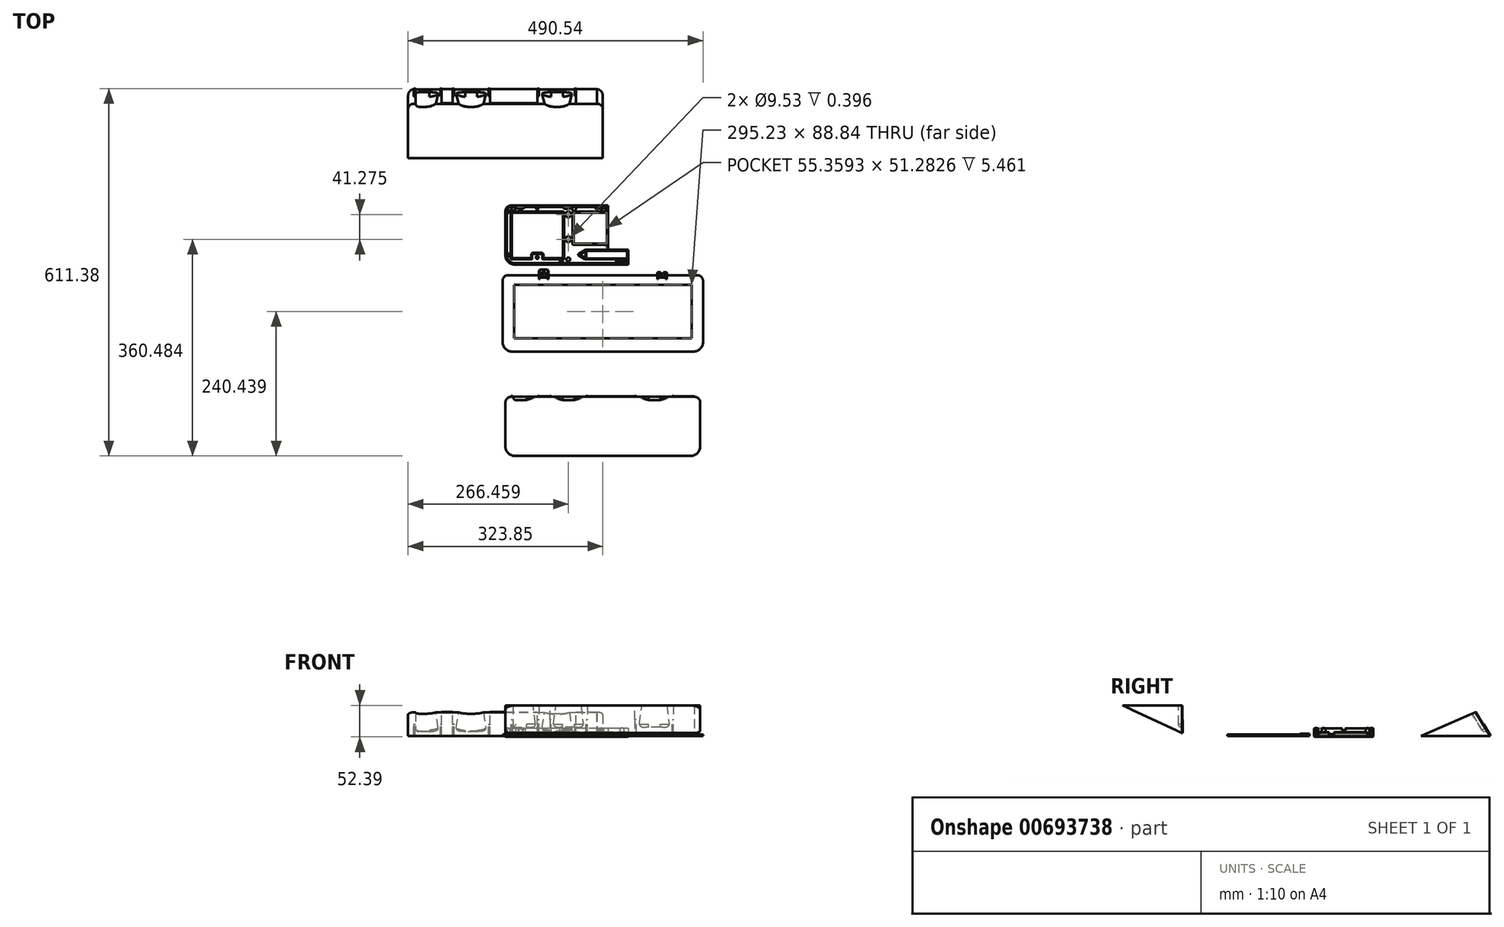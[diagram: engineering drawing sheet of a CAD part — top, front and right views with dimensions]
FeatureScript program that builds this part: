
annotation { "Feature Type Name" : "Feature", "Feature Type Description" : "" }
export const myFeature = defineFeature(function(context is Context, id is Id, definition is map)
    precondition{}
    {
        {
            var Q0;
            Q0=qCreatedBy(makeId("Top.planeOp"),FACE);
            var sketch = newSketch(context, id + "F0", { "sketchPlane" : qUnion([Q0])});
            skLineSegment(sketch, "E0.bottom", {"start": v(161.93, -49.21) * mm, "end": v(-161.93, -49.21) * mm});
            skLineSegment(sketch, "E0.top", {"start": v(161.93, 49.21) * mm, "end": v(-161.93, 49.21) * mm});
            skLineSegment(sketch, "E0.left", {"start": v(161.93, -49.21) * mm, "end": v(161.93, 49.21) * mm});
            skLineSegment(sketch, "E0.right", {"start": v(-161.93, -49.21) * mm, "end": v(-161.93, 49.21) * mm});
            skPoint(sketch, "E0.middle", {"position": v(0, 0) * mm});
            skSolve(sketch);
        }
        {
            var Q0;
            Q0=makeQuery(id+"F0.imprint","IMPRINT",FACE,{"disambiguationData":[TD([[makeQuery(id+"F0.imprint","IMPRINT",EDGE,{"derivedFrom":sQuery(id+"F0.wireOp",EDGE,"E0.bottom")}),-1.0]])]});
            extrude(context, id + "F1", {"entities" : qUnion([Q0]), "depth" : 3.17 * mm, "offsetDistance" : 25.4 * mm});
        }
        {
            var Q0;
            Q0=makeQuery(id+"F1.opExtrude","SWEPT_EDGE",EDGE,{"disambiguationData":[OSD([sQuery(id+"F0.wireOp",EDGE,"E0.bottom"),sQuery(id+"F0.wireOp",EDGE,"E0.right")])]});
            var Q1;
            Q1=makeQuery(id+"F1.opExtrude","SWEPT_EDGE",EDGE,{"disambiguationData":[OSD([sQuery(id+"F0.wireOp",EDGE,"E0.bottom"),sQuery(id+"F0.wireOp",EDGE,"E0.left")])]});
            fillet(context, id + "F2", {"entities" : qUnion([Q0, Q1]), "radius" : 15.88 * mm, "tangentPropagation" : true, "allowEdgeOverflow" : false});
        }
        {
            var Q0;
            Q0=makeQuery(id+"F1.opExtrude","SWEPT_EDGE",EDGE,{"disambiguationData":[OSD([sQuery(id+"F0.wireOp",EDGE,"E0.top"),sQuery(id+"F0.wireOp",EDGE,"E0.right")])]});
            var Q1;
            Q1=makeQuery(id+"F1.opExtrude","SWEPT_EDGE",EDGE,{"disambiguationData":[OSD([sQuery(id+"F0.wireOp",EDGE,"E0.top"),sQuery(id+"F0.wireOp",EDGE,"E0.left")])]});
            fillet(context, id + "F3", {"entities" : qUnion([Q0, Q1]), "radius" : 9.52 * mm, "tangentPropagation" : true, "allowEdgeOverflow" : false});
        }
        {
            var Q0;
            Q0=makeQuery(id+"F1.opExtrude","CAP_FACE",FACE,{"disambiguationData":[OSD([sQuery(id+"F0.wireOp",EDGE,"E0.bottom"),sQuery(id+"F0.wireOp",EDGE,"E0.top"),sQuery(id+"F0.wireOp",EDGE,"E0.left"),sQuery(id+"F0.wireOp",EDGE,"E0.right")])],"isStart":false});
            var sketch = newSketch(context, id + "F4", { "sketchPlane" : qUnion([Q0])});
            skArc(sketch, "E1.0", {"start": v(-152.4, 46.93) * mm, "mid": v(-157.52, 44.8) * mm, "end": v(-159.64, 39.69) * mm});
            skArc(sketch, "E2.0", {"start": v(-159.64, -33.34) * mm, "mid": v(-155.66, -42.95) * mm, "end": v(-146.05, -46.93) * mm});
            skLineSegment(sketch, "E3.0", {"start": v(-159.64, -33.34) * mm, "end": v(-159.64, 39.69) * mm});
            skArc(sketch, "E4.0", {"start": v(146.05, -46.93) * mm, "mid": v(155.66, -42.95) * mm, "end": v(159.64, -33.34) * mm});
            skArc(sketch, "E5.0", {"start": v(159.64, 39.69) * mm, "mid": v(157.52, 44.8) * mm, "end": v(152.4, 46.93) * mm});
            skLineSegment(sketch, "E6.0", {"start": v(159.64, -33.34) * mm, "end": v(159.64, 39.69) * mm});
            skLineSegment(sketch, "E7.0", {"start": v(152.4, 46.93) * mm, "end": v(-152.4, 46.93) * mm});
            skLineSegment(sketch, "E8.0", {"start": v(146.05, -46.93) * mm, "end": v(-146.05, -46.93) * mm});
            skSolve(sketch);
        }
        {
            var Q0;
            Q0=makeQuery(id+"F4.imprint","IMPRINT",FACE,{"disambiguationData":[TD([[makeQuery(id+"F4.imprint","IMPRINT",EDGE,{"derivedFrom":sQuery(id+"F4.wireOp",EDGE,"E1.0")}),-1.0]])]});
            extrude(context, id + "F5", {"entities" : qUnion([Q0]), "operationType" : NewBodyOperationType.ADD, "depth" : 9.52 * mm, "offsetDistance" : 25.4 * mm});
        }
        {
            var Q0;
            Q0=makeQuery(id+"F1.opExtrude","CAP_FACE",FACE,{"disambiguationData":[OSD([sQuery(id+"F0.wireOp",EDGE,"E0.bottom"),sQuery(id+"F0.wireOp",EDGE,"E0.top"),sQuery(id+"F0.wireOp",EDGE,"E0.left"),sQuery(id+"F0.wireOp",EDGE,"E0.right")])],"isStart":false});
            var sketch = newSketch(context, id + "F6", { "sketchPlane" : qUnion([Q0])});
            skCircle(sketch, "E9", {"center": v(-158.52, -33.34) * mm, "radius": 3.18 * mm});
            skLineSegment(sketch, "E10", {"start": v(-158.52, -33.34) * mm, "end": v(-158.52, 39.69) * mm, "construction": true});
            skCircle(sketch, "E11", {"center": v(-158.52, 39.69) * mm, "radius": 3.18 * mm});
            skCircle(sketch, "E12", {"center": v(158.23, 39.4) * mm, "radius": 3.18 * mm});
            skCircle(sketch, "E13", {"center": v(157.67, -33.34) * mm, "radius": 3.18 * mm});
            skCircle(sketch, "E14", {"center": v(70.74, 45.8) * mm, "radius": 3.18 * mm});
            skCircle(sketch, "E15", {"center": v(-2.29, 45.8) * mm, "radius": 3.29 * mm});
            skCircle(sketch, "E16", {"center": v(31.57, -45.8) * mm, "radius": 3.18 * mm});
            skCircle(sketch, "E17", {"center": v(-68.96, -45.8) * mm, "radius": 3.18 * mm});
            skSolve(sketch);
        }
        {
            var Q0;
            {var subQ0=sQuery(id+"F6.wireOp",EDGE,"E9");var subQ1=makeQuery(id+"F5.opExtrude","CAP_EDGE",EDGE,{"disambiguationData":[OSD([sQuery(id+"F4.wireOp",EDGE,"E2.0")])],"isStart":true});var subQ2=makeQuery(id+"F6.imprint","INTERSECT",VERTEX,{"derivedFrom":[subQ1,subQ0]});Q0=makeQuery(id+"F6.imprint","IMPRINT",FACE,{"disambiguationData":[TD([[makeQuery(id+"F6.imprint","IMPRINT",EDGE,{"disambiguationData":[TD([[subQ2,-1.0]])],"derivedFrom":subQ0}),1.0]])]});}
            var Q1;
            {var subQ0=sQuery(id+"F6.wireOp",EDGE,"E11");var subQ1=makeQuery(id+"F5.opExtrude","CAP_EDGE",EDGE,{"disambiguationData":[OSD([sQuery(id+"F4.wireOp",EDGE,"E1.0")])],"isStart":true});var subQ2=makeQuery(id+"F6.imprint","INTERSECT",VERTEX,{"derivedFrom":[subQ1,subQ0]});Q1=makeQuery(id+"F6.imprint","IMPRINT",FACE,{"disambiguationData":[TD([[makeQuery(id+"F6.imprint","IMPRINT",EDGE,{"disambiguationData":[TD([[subQ2,1.0]])],"derivedFrom":subQ0}),1.0]])]});}
            var Q2;
            {var subQ0=sQuery(id+"F6.wireOp",EDGE,"E15");var subQ1=makeQuery(id+"F5.opExtrude","CAP_EDGE",EDGE,{"disambiguationData":[OSD([sQuery(id+"F4.wireOp",EDGE,"E7.0")])],"isStart":true});var subQ2=makeQuery(id+"F6.imprint","INTERSECT",VERTEX,{"disambiguationData":[OD(0.0)],"derivedFrom":[subQ1,subQ0]});Q2=makeQuery(id+"F6.imprint","IMPRINT",FACE,{"disambiguationData":[TD([[makeQuery(id+"F6.imprint","IMPRINT",EDGE,{"disambiguationData":[TD([[subQ2,-1.0]])],"derivedFrom":subQ0}),1.0]])]});}
            var Q3;
            {var subQ0=sQuery(id+"F6.wireOp",EDGE,"E14");var subQ1=makeQuery(id+"F5.opExtrude","CAP_EDGE",EDGE,{"disambiguationData":[OSD([sQuery(id+"F4.wireOp",EDGE,"E7.0")])],"isStart":true});var subQ2=makeQuery(id+"F6.imprint","INTERSECT",VERTEX,{"disambiguationData":[OD(0.0)],"derivedFrom":[subQ1,subQ0]});Q3=makeQuery(id+"F6.imprint","IMPRINT",FACE,{"disambiguationData":[TD([[makeQuery(id+"F6.imprint","IMPRINT",EDGE,{"disambiguationData":[TD([[subQ2,1.0]])],"derivedFrom":subQ0}),1.0]])]});}
            var Q4;
            {var subQ0=sQuery(id+"F6.wireOp",EDGE,"E17");var subQ1=makeQuery(id+"F5.opExtrude","CAP_EDGE",EDGE,{"disambiguationData":[OSD([sQuery(id+"F4.wireOp",EDGE,"E8.0")])],"isStart":true});var subQ2=makeQuery(id+"F6.imprint","INTERSECT",VERTEX,{"disambiguationData":[OD(0.0)],"derivedFrom":[subQ1,subQ0]});Q4=makeQuery(id+"F6.imprint","IMPRINT",FACE,{"disambiguationData":[TD([[makeQuery(id+"F6.imprint","IMPRINT",EDGE,{"disambiguationData":[TD([[subQ2,1.0]])],"derivedFrom":subQ0}),1.0]])]});}
            var Q5;
            {var subQ0=sQuery(id+"F6.wireOp",EDGE,"E16");var subQ1=makeQuery(id+"F5.opExtrude","CAP_EDGE",EDGE,{"disambiguationData":[OSD([sQuery(id+"F4.wireOp",EDGE,"E8.0")])],"isStart":true});var subQ2=makeQuery(id+"F6.imprint","INTERSECT",VERTEX,{"disambiguationData":[OD(0.0)],"derivedFrom":[subQ1,subQ0]});Q5=makeQuery(id+"F6.imprint","IMPRINT",FACE,{"disambiguationData":[TD([[makeQuery(id+"F6.imprint","IMPRINT",EDGE,{"disambiguationData":[TD([[subQ2,-1.0]])],"derivedFrom":subQ0}),1.0]])]});}
            var Q6;
            {var subQ0=sQuery(id+"F6.wireOp",EDGE,"E13");var subQ1=makeQuery(id+"F5.opExtrude","CAP_EDGE",EDGE,{"disambiguationData":[OSD([sQuery(id+"F4.wireOp",EDGE,"E4.0")])],"isStart":true});var subQ2=makeQuery(id+"F6.imprint","INTERSECT",VERTEX,{"derivedFrom":[subQ1,subQ0]});Q6=makeQuery(id+"F6.imprint","IMPRINT",FACE,{"disambiguationData":[TD([[makeQuery(id+"F6.imprint","IMPRINT",EDGE,{"disambiguationData":[TD([[subQ2,1.0]])],"derivedFrom":subQ0}),1.0]])]});}
            var Q7;
            {var subQ0=sQuery(id+"F6.wireOp",EDGE,"E12");var subQ1=makeQuery(id+"F5.opExtrude","CAP_EDGE",EDGE,{"disambiguationData":[OSD([sQuery(id+"F4.wireOp",EDGE,"E5.0")])],"isStart":true});var subQ2=makeQuery(id+"F6.imprint","INTERSECT",VERTEX,{"derivedFrom":[subQ1,subQ0]});Q7=makeQuery(id+"F6.imprint","IMPRINT",FACE,{"disambiguationData":[TD([[makeQuery(id+"F6.imprint","IMPRINT",EDGE,{"disambiguationData":[TD([[subQ2,-1.0]])],"derivedFrom":subQ0}),1.0]])]});}
            extrude(context, id + "F7", {"entities" : qUnion([Q0, Q1, Q2, Q3, Q4, Q5, Q6, Q7]), "operationType" : NewBodyOperationType.ADD, "depth" : 9.52 * mm, "offsetDistance" : 25.4 * mm});
        }
        {
            var Q0;
            {var subQ0=sQuery(id+"F4.wireOp",EDGE,"E8.0");var subQ1=sQuery(id+"F4.wireOp",EDGE,"E7.0");var subQ2=sQuery(id+"F4.wireOp",EDGE,"E6.0");var subQ3=sQuery(id+"F4.wireOp",EDGE,"E4.0");var subQ4=sQuery(id+"F4.wireOp",EDGE,"E5.0");var subQ5=sQuery(id+"F4.wireOp",EDGE,"E3.0");var subQ6=sQuery(id+"F4.wireOp",EDGE,"E1.0");var subQ7=sQuery(id+"F4.wireOp",EDGE,"E2.0");Q0=makeQuery(id+"F7.boolean.opBoolean","MERGE",FACE,{"derivedFrom":[makeQuery(id+"F5.opExtrude","CAP_FACE",FACE,{"disambiguationData":[OSD([sQuery(id+"F0.wireOp",EDGE,"E0.bottom"),sQuery(id+"F0.wireOp",EDGE,"E0.top"),sQuery(id+"F0.wireOp",EDGE,"E0.left"),sQuery(id+"F0.wireOp",EDGE,"E0.right"),subQ6,subQ7,subQ5,subQ3,subQ4,subQ2,subQ1,subQ0])],"isStart":false}),makeQuery(id+"F7.opExtrude","CAP_FACE",FACE,{"disambiguationData":[OSD([subQ7,subQ5,sQuery(id+"F6.wireOp",EDGE,"E9")])],"isStart":false}),makeQuery(id+"F7.opExtrude","CAP_FACE",FACE,{"disambiguationData":[OSD([subQ6,subQ5,sQuery(id+"F6.wireOp",EDGE,"E11")])],"isStart":false}),makeQuery(id+"F7.opExtrude","CAP_FACE",FACE,{"disambiguationData":[OSD([subQ4,subQ2,sQuery(id+"F6.wireOp",EDGE,"E12")])],"isStart":false}),makeQuery(id+"F7.opExtrude","CAP_FACE",FACE,{"disambiguationData":[OSD([subQ3,subQ2,sQuery(id+"F6.wireOp",EDGE,"E13")])],"isStart":false}),makeQuery(id+"F7.opExtrude","CAP_FACE",FACE,{"disambiguationData":[OSD([subQ1,sQuery(id+"F6.wireOp",EDGE,"E14")])],"isStart":false}),makeQuery(id+"F7.opExtrude","CAP_FACE",FACE,{"disambiguationData":[OSD([subQ1,sQuery(id+"F6.wireOp",EDGE,"E15")])],"isStart":false}),makeQuery(id+"F7.opExtrude","CAP_FACE",FACE,{"disambiguationData":[OSD([subQ0,sQuery(id+"F6.wireOp",EDGE,"E16")])],"isStart":false}),makeQuery(id+"F7.opExtrude","CAP_FACE",FACE,{"disambiguationData":[OSD([subQ0,sQuery(id+"F6.wireOp",EDGE,"E17")])],"isStart":false})]});}
            var sketch = newSketch(context, id + "F8", { "sketchPlane" : qUnion([Q0])});
            skCircle(sketch, "E18", {"center": v(-2.29, 45.8) * mm, "radius": 1.03 * mm});
            skCircle(sketch, "E19", {"center": v(70.74, 45.8) * mm, "radius": 1.03 * mm});
            skCircle(sketch, "E20", {"center": v(158.23, 39.4) * mm, "radius": 1.03 * mm});
            skCircle(sketch, "E21", {"center": v(157.67, -33.34) * mm, "radius": 1.03 * mm});
            skCircle(sketch, "E22", {"center": v(31.57, -45.8) * mm, "radius": 1.03 * mm});
            skCircle(sketch, "E23", {"center": v(-68.96, -45.8) * mm, "radius": 1.03 * mm});
            skCircle(sketch, "E24", {"center": v(-158.52, -33.34) * mm, "radius": 1.03 * mm});
            skCircle(sketch, "E25", {"center": v(-158.52, 39.69) * mm, "radius": 1.03 * mm});
            skSolve(sketch);
        }
        {
            var Q0;
            Q0=makeQuery(id+"F8.imprint","IMPRINT",FACE,{"disambiguationData":[TD([[makeQuery(id+"F8.imprint","IMPRINT",EDGE,{"derivedFrom":sQuery(id+"F8.wireOp",EDGE,"E24")}),1.0]])]});
            var Q1;
            Q1=makeQuery(id+"F8.imprint","IMPRINT",FACE,{"disambiguationData":[TD([[makeQuery(id+"F8.imprint","IMPRINT",EDGE,{"derivedFrom":sQuery(id+"F8.wireOp",EDGE,"E23")}),1.0]])]});
            var Q2;
            Q2=makeQuery(id+"F8.imprint","IMPRINT",FACE,{"disambiguationData":[TD([[makeQuery(id+"F8.imprint","IMPRINT",EDGE,{"derivedFrom":sQuery(id+"F8.wireOp",EDGE,"E22")}),1.0]])]});
            var Q3;
            Q3=makeQuery(id+"F8.imprint","IMPRINT",FACE,{"disambiguationData":[TD([[makeQuery(id+"F8.imprint","IMPRINT",EDGE,{"derivedFrom":sQuery(id+"F8.wireOp",EDGE,"E21")}),1.0]])]});
            var Q4;
            Q4=makeQuery(id+"F8.imprint","IMPRINT",FACE,{"disambiguationData":[TD([[makeQuery(id+"F8.imprint","IMPRINT",EDGE,{"derivedFrom":sQuery(id+"F8.wireOp",EDGE,"E20")}),1.0]])]});
            var Q5;
            Q5=makeQuery(id+"F8.imprint","IMPRINT",FACE,{"disambiguationData":[TD([[makeQuery(id+"F8.imprint","IMPRINT",EDGE,{"derivedFrom":sQuery(id+"F8.wireOp",EDGE,"E19")}),1.0]])]});
            var Q6;
            Q6=makeQuery(id+"F8.imprint","IMPRINT",FACE,{"disambiguationData":[TD([[makeQuery(id+"F8.imprint","IMPRINT",EDGE,{"derivedFrom":sQuery(id+"F8.wireOp",EDGE,"E18")}),1.0]])]});
            var Q7;
            Q7=makeQuery(id+"F8.imprint","IMPRINT",FACE,{"disambiguationData":[TD([[makeQuery(id+"F8.imprint","IMPRINT",EDGE,{"derivedFrom":sQuery(id+"F8.wireOp",EDGE,"E25")}),1.0]])]});
            extrude(context, id + "F9", {"entities" : qUnion([Q0, Q1, Q2, Q3, Q4, Q5, Q6, Q7]), "operationType" : NewBodyOperationType.ADD, "depth" : 0.79 * mm, "offsetDistance" : 25.4 * mm});
        }
        {
            var Q0;
            Q0=makeQuery(id+"F1.opExtrude","CAP_FACE",FACE,{"disambiguationData":[OSD([sQuery(id+"F0.wireOp",EDGE,"E0.bottom"),sQuery(id+"F0.wireOp",EDGE,"E0.top"),sQuery(id+"F0.wireOp",EDGE,"E0.left"),sQuery(id+"F0.wireOp",EDGE,"E0.right")])],"isStart":false});
            var sketch = newSketch(context, id + "F10", { "sketchPlane" : qUnion([Q0])});
            skLineSegment(sketch, "E26", {"start": v(80.06, 46.93) * mm, "end": v(83.88, 43.75) * mm});
            skLineSegment(sketch, "E27", {"start": v(83.88, 43.75) * mm, "end": v(92.11, 43.75) * mm});
            skLineSegment(sketch, "E28", {"start": v(92.11, 43.75) * mm, "end": v(95.94, 46.93) * mm});
            skLineSegment(sketch, "E29", {"start": v(95.94, 46.93) * mm, "end": v(80.06, 46.93) * mm});
            skLineSegment(sketch, "E30", {"start": v(88, 46.93) * mm, "end": v(88, 43.23) * mm, "construction": true});
            skLineSegment(sketch, "E31", {"start": v(88, 43.75) * mm, "end": v(88, 44.46) * mm, "construction": true});
            skLineSegment(sketch, "E32", {"start": v(83.88, 45.62) * mm, "end": v(83.88, 43.16) * mm, "construction": true});
            skLineSegment(sketch, "E33", {"start": v(92.11, 45.79) * mm, "end": v(92.11, 43.52) * mm, "construction": true});
            skLineSegment(sketch, "E34", {"start": v(102.29, 46.93) * mm, "end": v(106.04, 43.75) * mm});
            skLineSegment(sketch, "E35", {"start": v(106.04, 43.75) * mm, "end": v(114.27, 43.75) * mm});
            skLineSegment(sketch, "E36", {"start": v(114.27, 43.75) * mm, "end": v(118.03, 46.93) * mm});
            skLineSegment(sketch, "E37", {"start": v(118.03, 46.93) * mm, "end": v(102.29, 46.93) * mm});
            skLineSegment(sketch, "E38", {"start": v(110.16, 46.93) * mm, "end": v(110.16, 43.75) * mm, "construction": true});
            skLineSegment(sketch, "E39", {"start": v(106.04, 45.04) * mm, "end": v(106.04, 42.78) * mm, "construction": true});
            skLineSegment(sketch, "E40", {"start": v(114.27, 44.82) * mm, "end": v(114.27, 43.03) * mm, "construction": true});
            skLineSegment(sketch, "E41", {"start": v(102.29, 47.44) * mm, "end": v(102.29, 46.4) * mm, "construction": true});
            skLineSegment(sketch, "E42", {"start": v(-67.48, 46.93) * mm, "end": v(-63.72, 43.75) * mm});
            skLineSegment(sketch, "E43", {"start": v(-63.72, 43.75) * mm, "end": v(-55.5, 43.75) * mm});
            skLineSegment(sketch, "E44", {"start": v(-55.5, 43.75) * mm, "end": v(-51.73, 46.93) * mm});
            skLineSegment(sketch, "E45", {"start": v(-51.73, 46.93) * mm, "end": v(-67.48, 46.93) * mm});
            skLineSegment(sketch, "E46", {"start": v(-59.6, 46.93) * mm, "end": v(-59.6, 41.87) * mm, "construction": true});
            skPoint(sketch, "E46.startSnap0", {"position": v(-59.6, 43.75) * mm});
            skLineSegment(sketch, "E47", {"start": v(-144.62, 46.93) * mm, "end": v(-140.86, 43.75) * mm});
            skLineSegment(sketch, "E48", {"start": v(-140.86, 43.75) * mm, "end": v(-132.63, 43.75) * mm});
            skLineSegment(sketch, "E49", {"start": v(-132.63, 43.75) * mm, "end": v(-128.87, 46.93) * mm});
            skLineSegment(sketch, "E50", {"start": v(-128.87, 46.93) * mm, "end": v(-144.62, 46.93) * mm});
            skLineSegment(sketch, "E51", {"start": v(-136.74, 46.93) * mm, "end": v(-136.74, 41.02) * mm, "construction": true});
            skSolve(sketch);
        }
        {
            var Q0;
            Q0=makeQuery(id+"F10.imprint","IMPRINT",FACE,{"disambiguationData":[TD([[makeQuery(id+"F10.imprint","IMPRINT",EDGE,{"derivedFrom":sQuery(id+"F10.wireOp",EDGE,"E47")}),1.0]])]});
            var Q1;
            Q1=makeQuery(id+"F10.imprint","IMPRINT",FACE,{"disambiguationData":[TD([[makeQuery(id+"F10.imprint","IMPRINT",EDGE,{"derivedFrom":sQuery(id+"F10.wireOp",EDGE,"E42")}),1.0]])]});
            var Q2;
            Q2=makeQuery(id+"F10.imprint","IMPRINT",FACE,{"disambiguationData":[TD([[makeQuery(id+"F10.imprint","IMPRINT",EDGE,{"derivedFrom":sQuery(id+"F10.wireOp",EDGE,"E26")}),1.0]])]});
            var Q3;
            Q3=makeQuery(id+"F10.imprint","IMPRINT",FACE,{"disambiguationData":[TD([[makeQuery(id+"F10.imprint","IMPRINT",EDGE,{"derivedFrom":sQuery(id+"F10.wireOp",EDGE,"E34")}),1.0]])]});
            extrude(context, id + "F11", {"entities" : qUnion([Q0, Q1, Q2, Q3]), "operationType" : NewBodyOperationType.ADD, "depth" : 9.52 * mm, "offsetDistance" : 25.4 * mm});
        }
        {
            var Q0;
            {var subQ0=sQuery(id+"F4.wireOp",EDGE,"E8.0");var subQ1=makeQuery(id+"F7.opExtrude","CAP_FACE",FACE,{"disambiguationData":[OSD([subQ0,sQuery(id+"F6.wireOp",EDGE,"E17")])],"isStart":false});var subQ2=makeQuery(id+"F7.opExtrude","CAP_FACE",FACE,{"disambiguationData":[OSD([subQ0,sQuery(id+"F6.wireOp",EDGE,"E16")])],"isStart":false});var subQ3=sQuery(id+"F4.wireOp",EDGE,"E7.0");var subQ4=makeQuery(id+"F7.opExtrude","CAP_FACE",FACE,{"disambiguationData":[OSD([subQ3,sQuery(id+"F6.wireOp",EDGE,"E15")])],"isStart":false});var subQ5=sQuery(id+"F6.wireOp",EDGE,"E14");var subQ6=makeQuery(id+"F7.opExtrude","CAP_FACE",FACE,{"disambiguationData":[OSD([subQ3,subQ5])],"isStart":false});var subQ7=sQuery(id+"F4.wireOp",EDGE,"E6.0");var subQ8=sQuery(id+"F4.wireOp",EDGE,"E4.0");var subQ9=makeQuery(id+"F7.opExtrude","CAP_FACE",FACE,{"disambiguationData":[OSD([subQ8,subQ7,sQuery(id+"F6.wireOp",EDGE,"E13")])],"isStart":false});var subQ11=sQuery(id+"F0.wireOp",EDGE,"E0.right");var subQ12=sQuery(id+"F0.wireOp",EDGE,"E0.left");var subQ13=sQuery(id+"F0.wireOp",EDGE,"E0.top");var subQ14=sQuery(id+"F0.wireOp",EDGE,"E0.bottom");var subQ15=makeQuery(id+"F1.opExtrude","CAP_FACE",FACE,{"disambiguationData":[OSD([subQ14,subQ13,subQ12,subQ11])],"isStart":false});var subQ16=sQuery(id+"F4.wireOp",EDGE,"E5.0");var subQ17=makeQuery(id+"F7.opExtrude","CAP_FACE",FACE,{"disambiguationData":[OSD([subQ16,subQ7,sQuery(id+"F6.wireOp",EDGE,"E12")])],"isStart":false});var subQ18=sQuery(id+"F4.wireOp",EDGE,"E3.0");var subQ19=sQuery(id+"F4.wireOp",EDGE,"E2.0");var subQ20=sQuery(id+"F4.wireOp",EDGE,"E1.0");var subQ21=makeQuery(id+"F5.opExtrude","CAP_FACE",FACE,{"disambiguationData":[OSD([subQ14,subQ13,subQ12,subQ11,subQ20,subQ19,subQ18,subQ8,subQ16,subQ7,subQ3,subQ0])],"isStart":false});var subQ22=makeQuery(id+"F7.opExtrude","CAP_FACE",FACE,{"disambiguationData":[OSD([subQ19,subQ18,sQuery(id+"F6.wireOp",EDGE,"E9")])],"isStart":false});var subQ23=makeQuery(id+"F7.opExtrude","CAP_FACE",FACE,{"disambiguationData":[OSD([subQ20,subQ18,sQuery(id+"F6.wireOp",EDGE,"E11")])],"isStart":false});var subQ24=sQuery(id+"F10.wireOp",EDGE,"E28");Q0=makeQuery(id+"F11.boolean.opBoolean","SPLIT",FACE,{"disambiguationData":[TD([makeQuery(id+"F11.opExtrude","SWEPT_FACE",FACE,{"disambiguationData":[OSD([subQ24])]})])],"derivedFrom":makeQuery(id+"F7.boolean.opBoolean","SPLIT",FACE,{"disambiguationData":[TD([subQ15,subQ21,makeQuery(id+"F5.opExtrude","SWEPT_FACE",FACE,{"disambiguationData":[OSD([subQ16])]}),subQ22,subQ23,subQ17,subQ9,makeQuery(id+"F7.opExtrude","SWEPT_FACE",FACE,{"disambiguationData":[OSD([subQ5])]}),subQ6,subQ4,subQ2,subQ1])],"derivedFrom":makeQuery(id+"F5.opExtrude","SWEPT_FACE",FACE,{"disambiguationData":[OSD([subQ3])]})})});}
            var sketch = newSketch(context, id + "F12", { "sketchPlane" : qUnion([Q0])});
            skCircle(sketch, "E52", {"center": v(-148.66, 3.04) * mm, "radius": 3.18 * mm});
            skCircle(sketch, "E53", {"center": v(99.9, 3.18) * mm, "radius": 3.18 * mm});
            skSolve(sketch);
        }
        {
            var Q0;
            Q0=makeQuery(id+"F12.imprint","IMPRINT",FACE,{"disambiguationData":[TD([[makeQuery(id+"F12.imprint","IMPRINT",EDGE,{"derivedFrom":sQuery(id+"F12.wireOp",EDGE,"E52")}),1.0]])]});
            extrude(context, id + "F13", {"entities" : qUnion([Q0]), "operationType" : NewBodyOperationType.ADD, "depth" : 6.35 * mm, "offsetDistance" : 25.4 * mm});
        }
        {
            var Q0;
            {var subQ0=sQuery(id+"F12.wireOp",EDGE,"E52");Q0=makeQuery(id+"F13.boolean.opBoolean","SPLIT",EDGE,{"disambiguationData":[TD([makeQuery(id+"F1.opExtrude","CAP_FACE",FACE,{"disambiguationData":[OSD([sQuery(id+"F0.wireOp",EDGE,"E0.bottom"),sQuery(id+"F0.wireOp",EDGE,"E0.top"),sQuery(id+"F0.wireOp",EDGE,"E0.left"),sQuery(id+"F0.wireOp",EDGE,"E0.right")])],"isStart":false})])],"derivedFrom":makeQuery(id+"F13.opExtrude","CAP_EDGE",EDGE,{"disambiguationData":[OSD([subQ0])],"isStart":false})});}
            fillet(context, id + "F14", {"entities" : qUnion([Q0]), "radius" : 2.54 * mm, "tangentPropagation" : true, "allowEdgeOverflow" : false});
        }
        {
            var Q0;
            {var subQ0=sQuery(id+"F4.wireOp",EDGE,"E8.0");var subQ1=makeQuery(id+"F7.opExtrude","CAP_FACE",FACE,{"disambiguationData":[OSD([subQ0,sQuery(id+"F6.wireOp",EDGE,"E17")])],"isStart":false});var subQ2=makeQuery(id+"F7.opExtrude","CAP_FACE",FACE,{"disambiguationData":[OSD([subQ0,sQuery(id+"F6.wireOp",EDGE,"E16")])],"isStart":false});var subQ3=sQuery(id+"F4.wireOp",EDGE,"E7.0");var subQ4=makeQuery(id+"F7.opExtrude","CAP_FACE",FACE,{"disambiguationData":[OSD([subQ3,sQuery(id+"F6.wireOp",EDGE,"E15")])],"isStart":false});var subQ5=sQuery(id+"F6.wireOp",EDGE,"E14");var subQ6=makeQuery(id+"F7.opExtrude","CAP_FACE",FACE,{"disambiguationData":[OSD([subQ3,subQ5])],"isStart":false});var subQ7=sQuery(id+"F4.wireOp",EDGE,"E6.0");var subQ8=sQuery(id+"F4.wireOp",EDGE,"E4.0");var subQ9=makeQuery(id+"F7.opExtrude","CAP_FACE",FACE,{"disambiguationData":[OSD([subQ8,subQ7,sQuery(id+"F6.wireOp",EDGE,"E13")])],"isStart":false});var subQ11=sQuery(id+"F0.wireOp",EDGE,"E0.right");var subQ12=sQuery(id+"F0.wireOp",EDGE,"E0.left");var subQ13=sQuery(id+"F0.wireOp",EDGE,"E0.top");var subQ14=sQuery(id+"F0.wireOp",EDGE,"E0.bottom");var subQ15=makeQuery(id+"F1.opExtrude","CAP_FACE",FACE,{"disambiguationData":[OSD([subQ14,subQ13,subQ12,subQ11])],"isStart":false});var subQ16=sQuery(id+"F4.wireOp",EDGE,"E5.0");var subQ17=makeQuery(id+"F7.opExtrude","CAP_FACE",FACE,{"disambiguationData":[OSD([subQ16,subQ7,sQuery(id+"F6.wireOp",EDGE,"E12")])],"isStart":false});var subQ18=sQuery(id+"F4.wireOp",EDGE,"E3.0");var subQ19=sQuery(id+"F4.wireOp",EDGE,"E2.0");var subQ20=sQuery(id+"F4.wireOp",EDGE,"E1.0");var subQ21=makeQuery(id+"F5.opExtrude","CAP_FACE",FACE,{"disambiguationData":[OSD([subQ14,subQ13,subQ12,subQ11,subQ20,subQ19,subQ18,subQ8,subQ16,subQ7,subQ3,subQ0])],"isStart":false});var subQ22=makeQuery(id+"F7.opExtrude","CAP_FACE",FACE,{"disambiguationData":[OSD([subQ19,subQ18,sQuery(id+"F6.wireOp",EDGE,"E9")])],"isStart":false});var subQ23=makeQuery(id+"F7.opExtrude","CAP_FACE",FACE,{"disambiguationData":[OSD([subQ20,subQ18,sQuery(id+"F6.wireOp",EDGE,"E11")])],"isStart":false});var subQ24=sQuery(id+"F10.wireOp",EDGE,"E28");Q0=makeQuery(id+"F11.boolean.opBoolean","SPLIT",FACE,{"disambiguationData":[TD([makeQuery(id+"F11.opExtrude","SWEPT_FACE",FACE,{"disambiguationData":[OSD([subQ24])]})])],"derivedFrom":makeQuery(id+"F7.boolean.opBoolean","SPLIT",FACE,{"disambiguationData":[TD([subQ15,subQ21,makeQuery(id+"F5.opExtrude","SWEPT_FACE",FACE,{"disambiguationData":[OSD([subQ16])]}),subQ22,subQ23,subQ17,subQ9,makeQuery(id+"F7.opExtrude","SWEPT_FACE",FACE,{"disambiguationData":[OSD([subQ5])]}),subQ6,subQ4,subQ2,subQ1])],"derivedFrom":makeQuery(id+"F5.opExtrude","SWEPT_FACE",FACE,{"disambiguationData":[OSD([subQ3])]})})});}
            var sketch = newSketch(context, id + "F15", { "sketchPlane" : qUnion([Q0])});
            skCircle(sketch, "E54", {"center": v(99.11, 3.18) * mm, "radius": 2.92 * mm});
            skSolve(sketch);
        }
        {
            var Q0;
            {var subQ0=sQuery(id+"F15.wireOp",EDGE,"E54");var subQ1=makeQuery(id+"F1.opExtrude","CAP_FACE",FACE,{"disambiguationData":[OSD([sQuery(id+"F0.wireOp",EDGE,"E0.bottom"),sQuery(id+"F0.wireOp",EDGE,"E0.top"),sQuery(id+"F0.wireOp",EDGE,"E0.left"),sQuery(id+"F0.wireOp",EDGE,"E0.right")])],"isStart":false});var subQ2=sQuery(id+"F4.wireOp",EDGE,"E7.0");var subQ3=makeQuery(id+"F5.opExtrude","SWEPT_FACE",FACE,{"disambiguationData":[OSD([subQ2])]});var subQ4=makeQuery(id+"F11.boolean.opBoolean","SPLIT",EDGE,{"disambiguationData":[TD([makeQuery(id+"F11.opExtrude","SWEPT_FACE",FACE,{"disambiguationData":[OSD([sQuery(id+"F10.wireOp",EDGE,"E28")])]})])],"derivedFrom":makeQuery(id+"F7.boolean.opBoolean","SPLIT",EDGE,{"disambiguationData":[TD([subQ1,makeQuery(id+"F5.opExtrude","SWEPT_FACE",FACE,{"disambiguationData":[OSD([sQuery(id+"F4.wireOp",EDGE,"E5.0")])]}),subQ3,makeQuery(id+"F7.opExtrude","SWEPT_FACE",FACE,{"disambiguationData":[OSD([sQuery(id+"F6.wireOp",EDGE,"E14")])]})])],"derivedFrom":makeQuery(id+"F5.opExtrude","CAP_EDGE",EDGE,{"disambiguationData":[OSD([subQ2])],"isStart":true})})});var subQ5=makeQuery(id+"F15.imprint","INTERSECT",VERTEX,{"disambiguationData":[OD(0.0)],"derivedFrom":[subQ4,subQ0]});Q0=makeQuery(id+"F15.imprint","IMPRINT",FACE,{"disambiguationData":[TD([[makeQuery(id+"F15.imprint","IMPRINT",EDGE,{"disambiguationData":[TD([[subQ5,1.0]])],"derivedFrom":subQ0}),1.0]])]});}
            var Q1;
            Q1=sQuery(id+"F15.wireOp",EDGE,"E54");
            extrude(context, id + "F16", {"entities" : qUnion([Q0]), "operationType" : NewBodyOperationType.ADD, "surfaceEntities" : qUnion([Q1]), "depth" : 6.35 * mm, "offsetDistance" : 25.4 * mm});
        }
        {
            var Q0;
            Q0=makeQuery(id+"F16.opExtrude","CAP_EDGE",EDGE,{"disambiguationData":[OSD([sQuery(id+"F15.wireOp",EDGE,"E54")])],"isStart":false});
            fillet(context, id + "F17", {"entities" : qUnion([Q0]), "radius" : 2.54 * mm, "tangentPropagation" : true, "allowEdgeOverflow" : false});
        }
        {
            var Q0;
            {var subQ0=sQuery(id+"F4.wireOp",EDGE,"E8.0");var subQ1=makeQuery(id+"F7.opExtrude","CAP_FACE",FACE,{"disambiguationData":[OSD([subQ0,sQuery(id+"F6.wireOp",EDGE,"E16")])],"isStart":false});var subQ2=sQuery(id+"F6.wireOp",EDGE,"E15");var subQ3=sQuery(id+"F4.wireOp",EDGE,"E7.0");var subQ4=makeQuery(id+"F7.opExtrude","CAP_FACE",FACE,{"disambiguationData":[OSD([subQ3,subQ2])],"isStart":false});var subQ6=makeQuery(id+"F7.opExtrude","SWEPT_FACE",FACE,{"disambiguationData":[OSD([subQ2])]});var subQ7=makeQuery(id+"F7.opExtrude","CAP_FACE",FACE,{"disambiguationData":[OSD([subQ3,sQuery(id+"F6.wireOp",EDGE,"E14")])],"isStart":false});var subQ8=sQuery(id+"F4.wireOp",EDGE,"E6.0");var subQ9=sQuery(id+"F4.wireOp",EDGE,"E4.0");var subQ10=makeQuery(id+"F7.opExtrude","CAP_FACE",FACE,{"disambiguationData":[OSD([subQ9,subQ8,sQuery(id+"F6.wireOp",EDGE,"E13")])],"isStart":false});var subQ11=sQuery(id+"F0.wireOp",EDGE,"E0.right");var subQ12=sQuery(id+"F0.wireOp",EDGE,"E0.left");var subQ13=sQuery(id+"F0.wireOp",EDGE,"E0.top");var subQ14=sQuery(id+"F0.wireOp",EDGE,"E0.bottom");var subQ15=makeQuery(id+"F1.opExtrude","CAP_FACE",FACE,{"disambiguationData":[OSD([subQ14,subQ13,subQ12,subQ11])],"isStart":false});var subQ16=sQuery(id+"F4.wireOp",EDGE,"E5.0");var subQ17=makeQuery(id+"F7.opExtrude","CAP_FACE",FACE,{"disambiguationData":[OSD([subQ16,subQ8,sQuery(id+"F6.wireOp",EDGE,"E12")])],"isStart":false});var subQ18=sQuery(id+"F4.wireOp",EDGE,"E3.0");var subQ19=sQuery(id+"F4.wireOp",EDGE,"E2.0");var subQ20=sQuery(id+"F4.wireOp",EDGE,"E1.0");var subQ21=makeQuery(id+"F5.opExtrude","CAP_FACE",FACE,{"disambiguationData":[OSD([subQ14,subQ13,subQ12,subQ11,subQ20,subQ19,subQ18,subQ9,subQ16,subQ8,subQ3,subQ0])],"isStart":false});var subQ22=makeQuery(id+"F7.opExtrude","CAP_FACE",FACE,{"disambiguationData":[OSD([subQ19,subQ18,sQuery(id+"F6.wireOp",EDGE,"E9")])],"isStart":false});var subQ23=makeQuery(id+"F7.opExtrude","CAP_FACE",FACE,{"disambiguationData":[OSD([subQ20,subQ18,sQuery(id+"F6.wireOp",EDGE,"E11")])],"isStart":false});var subQ24=makeQuery(id+"F7.opExtrude","CAP_FACE",FACE,{"disambiguationData":[OSD([subQ0,sQuery(id+"F6.wireOp",EDGE,"E17")])],"isStart":false});Q0=makeQuery(id+"F11.boolean.opBoolean","SPLIT",FACE,{"disambiguationData":[TD([subQ6])],"derivedFrom":makeQuery(id+"F7.boolean.opBoolean","SPLIT",FACE,{"disambiguationData":[TD([subQ15,makeQuery(id+"F5.opExtrude","SWEPT_FACE",FACE,{"disambiguationData":[OSD([subQ20])]}),subQ21,subQ22,subQ23,subQ17,subQ10,subQ7,subQ6,subQ4,subQ1,subQ24])],"derivedFrom":makeQuery(id+"F5.opExtrude","SWEPT_FACE",FACE,{"disambiguationData":[OSD([subQ3])]})})});}
            var sketch = newSketch(context, id + "F18", { "sketchPlane" : qUnion([Q0])});
            skCircle(sketch, "E55", {"center": v(-47.86, 3.18) * mm, "radius": 3.18 * mm});
            skSolve(sketch);
        }
        {
            var Q0;
            {var subQ0=sQuery(id+"F18.wireOp",EDGE,"E55");var subQ1=makeQuery(id+"F1.opExtrude","CAP_FACE",FACE,{"disambiguationData":[OSD([sQuery(id+"F0.wireOp",EDGE,"E0.bottom"),sQuery(id+"F0.wireOp",EDGE,"E0.top"),sQuery(id+"F0.wireOp",EDGE,"E0.left"),sQuery(id+"F0.wireOp",EDGE,"E0.right")])],"isStart":false});var subQ2=sQuery(id+"F4.wireOp",EDGE,"E7.0");var subQ3=makeQuery(id+"F5.opExtrude","SWEPT_FACE",FACE,{"disambiguationData":[OSD([subQ2])]});var subQ4=makeQuery(id+"F7.opExtrude","SWEPT_FACE",FACE,{"disambiguationData":[OSD([sQuery(id+"F6.wireOp",EDGE,"E15")])]});var subQ5=makeQuery(id+"F11.boolean.opBoolean","SPLIT",EDGE,{"disambiguationData":[TD([subQ4])],"derivedFrom":makeQuery(id+"F7.boolean.opBoolean","SPLIT",EDGE,{"disambiguationData":[TD([subQ1,makeQuery(id+"F5.opExtrude","SWEPT_FACE",FACE,{"disambiguationData":[OSD([sQuery(id+"F4.wireOp",EDGE,"E1.0")])]}),subQ3,subQ4])],"derivedFrom":makeQuery(id+"F5.opExtrude","CAP_EDGE",EDGE,{"disambiguationData":[OSD([subQ2])],"isStart":true})})});var subQ6=makeQuery(id+"F18.imprint","INTERSECT",VERTEX,{"disambiguationData":[OD(0.0)],"derivedFrom":[subQ5,subQ0]});Q0=makeQuery(id+"F18.imprint","IMPRINT",FACE,{"disambiguationData":[TD([[makeQuery(id+"F18.imprint","IMPRINT",EDGE,{"disambiguationData":[TD([[subQ6,-1.0]])],"derivedFrom":subQ0}),1.0]])]});}
            extrude(context, id + "F19", {"entities" : qUnion([Q0]), "operationType" : NewBodyOperationType.ADD, "depth" : 6.35 * mm, "offsetDistance" : 25.4 * mm});
        }
        {
            var Q0;
            Q0=makeQuery(id+"F19.opExtrude","CAP_EDGE",EDGE,{"disambiguationData":[OSD([sQuery(id+"F18.wireOp",EDGE,"E55")])],"isStart":false});
            fillet(context, id + "F20", {"entities" : qUnion([Q0]), "radius" : 2.54 * mm, "tangentPropagation" : true, "allowEdgeOverflow" : false});
        }
        {
            var Q0;
            Q0=makeQuery(id+"F1.opExtrude","CAP_FACE",FACE,{"disambiguationData":[OSD([sQuery(id+"F0.wireOp",EDGE,"E0.bottom"),sQuery(id+"F0.wireOp",EDGE,"E0.top"),sQuery(id+"F0.wireOp",EDGE,"E0.left"),sQuery(id+"F0.wireOp",EDGE,"E0.right")])],"isStart":false});
            var sketch = newSketch(context, id + "F21", { "sketchPlane" : qUnion([Q0])});
            skLineSegment(sketch, "E56.bottom", {"start": v(154.86, 38.99) * mm, "end": v(95.94, 38.99) * mm});
            skLineSegment(sketch, "E56.top", {"start": v(154.86, 1.83) * mm, "end": v(95.94, 1.83) * mm});
            skLineSegment(sketch, "E56.left", {"start": v(154.86, 38.99) * mm, "end": v(154.86, 1.83) * mm});
            skLineSegment(sketch, "E56.right", {"start": v(95.94, 38.99) * mm, "end": v(95.94, 1.83) * mm});
            skPoint(sketch, "E57.MirrorCS.start.orphan", {"position": v(95.94, 38.99) * mm});
            skPoint(sketch, "E58.MirrorCS.start.orphan", {"position": v(154.86, 38.99) * mm});
            skSolve(sketch);
        }
        {
            var Q0;
            Q0=makeQuery(id+"F21.imprint","IMPRINT",FACE,{"disambiguationData":[TD([[makeQuery(id+"F21.imprint","IMPRINT",EDGE,{"derivedFrom":sQuery(id+"F21.wireOp",EDGE,"E56.bottom")}),1.0]])]});
            extrude(context, id + "F22", {"entities" : qUnion([Q0]), "operationType" : NewBodyOperationType.ADD, "depth" : 2.83 * mm, "offsetDistance" : 25.4 * mm});
        }
        {
            var Q0;
            Q0=makeQuery(id+"F22.opExtrude","SWEPT_EDGE",EDGE,{"disambiguationData":[OSD([sQuery(id+"F21.wireOp",EDGE,"E56.top"),sQuery(id+"F21.wireOp",EDGE,"E56.right")])]});
            var Q1;
            Q1=makeQuery(id+"F22.opExtrude","SWEPT_EDGE",EDGE,{"disambiguationData":[OSD([sQuery(id+"F21.wireOp",EDGE,"E56.bottom"),sQuery(id+"F21.wireOp",EDGE,"E56.right")])]});
            var Q2;
            Q2=makeQuery(id+"F22.opExtrude","SWEPT_EDGE",EDGE,{"disambiguationData":[OSD([sQuery(id+"F21.wireOp",EDGE,"E56.bottom"),sQuery(id+"F21.wireOp",EDGE,"E56.left")])]});
            var Q3;
            Q3=makeQuery(id+"F22.opExtrude","SWEPT_EDGE",EDGE,{"disambiguationData":[OSD([sQuery(id+"F21.wireOp",EDGE,"E56.top"),sQuery(id+"F21.wireOp",EDGE,"E56.left")])]});
            fillet(context, id + "F23", {"entities" : qUnion([Q0, Q1, Q2, Q3]), "radius" : 1.27 * mm, "tangentPropagation" : true, "allowEdgeOverflow" : false});
        }
        {
            var Q0;
            Q0=makeQuery(id+"F22.opExtrude","CAP_FACE",FACE,{"disambiguationData":[OSD([sQuery(id+"F21.wireOp",EDGE,"E56.bottom"),sQuery(id+"F21.wireOp",EDGE,"E56.top"),sQuery(id+"F21.wireOp",EDGE,"E56.left"),sQuery(id+"F21.wireOp",EDGE,"E56.right")])],"isStart":false});
            var sketch = newSketch(context, id + "F24", { "sketchPlane" : qUnion([Q0])});
            skLineSegment(sketch, "E59.0", {"start": v(97.79, 3.68) * mm, "end": v(153, 3.68) * mm});
            skLineSegment(sketch, "E59.1", {"start": v(97.79, 37.13) * mm, "end": v(97.79, 3.68) * mm});
            skLineSegment(sketch, "E59.2", {"start": v(153, 37.13) * mm, "end": v(97.79, 37.13) * mm});
            skLineSegment(sketch, "E59.3", {"start": v(153, 3.68) * mm, "end": v(153, 37.13) * mm});
            skSolve(sketch);
        }
        {
            var Q0;
            Q0=makeQuery(id+"F24.imprint","IMPRINT",FACE,{"disambiguationData":[TD([[makeQuery(id+"F24.imprint","IMPRINT",EDGE,{"derivedFrom":sQuery(id+"F24.wireOp",EDGE,"E59.0")}),1.0]])]});
            extrude(context, id + "F25", {"entities" : qUnion([Q0]), "operationType" : NewBodyOperationType.REMOVE, "oppositeDirection" : true, "depth" : 5.7 * mm, "offsetDistance" : 25.4 * mm});
        }
        {
            var Q0;
            Q0=makeQuery(id+"F1.opExtrude","CAP_FACE",FACE,{"disambiguationData":[OSD([sQuery(id+"F0.wireOp",EDGE,"E0.bottom"),sQuery(id+"F0.wireOp",EDGE,"E0.top"),sQuery(id+"F0.wireOp",EDGE,"E0.left"),sQuery(id+"F0.wireOp",EDGE,"E0.right")])],"isStart":false});
            var sketch = newSketch(context, id + "F26", { "sketchPlane" : qUnion([Q0])});
            skLineSegment(sketch, "E60.bottom", {"start": v(81.65, 38.98) * mm, "end": v(22.72, 38.98) * mm});
            skLineSegment(sketch, "E60.top", {"start": v(81.65, 1.82) * mm, "end": v(22.72, 1.82) * mm});
            skLineSegment(sketch, "E60.left", {"start": v(81.65, 38.98) * mm, "end": v(81.65, 1.82) * mm});
            skLineSegment(sketch, "E60.right", {"start": v(22.72, 38.98) * mm, "end": v(22.72, 1.82) * mm});
            skSolve(sketch);
        }
        {
            var Q0;
            Q0=makeQuery(id+"F26.imprint","IMPRINT",FACE,{"disambiguationData":[TD([[makeQuery(id+"F26.imprint","IMPRINT",EDGE,{"derivedFrom":sQuery(id+"F26.wireOp",EDGE,"E60.bottom")}),1.0]])]});
            extrude(context, id + "F27", {"entities" : qUnion([Q0]), "operationType" : NewBodyOperationType.ADD, "depth" : 2.84 * mm, "offsetDistance" : 25.4 * mm});
        }
        {
            var Q0;
            Q0=makeQuery(id+"F27.opExtrude","SWEPT_EDGE",EDGE,{"disambiguationData":[OSD([sQuery(id+"F26.wireOp",EDGE,"E60.top"),sQuery(id+"F26.wireOp",EDGE,"E60.right")])]});
            var Q1;
            Q1=makeQuery(id+"F27.opExtrude","SWEPT_EDGE",EDGE,{"disambiguationData":[OSD([sQuery(id+"F26.wireOp",EDGE,"E60.top"),sQuery(id+"F26.wireOp",EDGE,"E60.left")])]});
            var Q2;
            Q2=makeQuery(id+"F27.opExtrude","SWEPT_EDGE",EDGE,{"disambiguationData":[OSD([sQuery(id+"F26.wireOp",EDGE,"E60.bottom"),sQuery(id+"F26.wireOp",EDGE,"E60.left")])]});
            var Q3;
            Q3=makeQuery(id+"F27.opExtrude","SWEPT_EDGE",EDGE,{"disambiguationData":[OSD([sQuery(id+"F26.wireOp",EDGE,"E60.bottom"),sQuery(id+"F26.wireOp",EDGE,"E60.right")])]});
            fillet(context, id + "F28", {"entities" : qUnion([Q0, Q1, Q2, Q3]), "radius" : 1.27 * mm, "tangentPropagation" : true, "allowEdgeOverflow" : false});
        }
        {
            var Q0;
            Q0=makeQuery(id+"F27.opExtrude","CAP_FACE",FACE,{"disambiguationData":[OSD([sQuery(id+"F26.wireOp",EDGE,"E60.bottom"),sQuery(id+"F26.wireOp",EDGE,"E60.top"),sQuery(id+"F26.wireOp",EDGE,"E60.left"),sQuery(id+"F26.wireOp",EDGE,"E60.right")])],"isStart":false});
            var sketch = newSketch(context, id + "F29", { "sketchPlane" : qUnion([Q0])});
            skLineSegment(sketch, "E61.0", {"start": v(24.57, 3.67) * mm, "end": v(79.8, 3.67) * mm});
            skLineSegment(sketch, "E61.1", {"start": v(24.57, 37.12) * mm, "end": v(24.57, 3.67) * mm});
            skLineSegment(sketch, "E61.2", {"start": v(79.8, 37.12) * mm, "end": v(24.57, 37.12) * mm});
            skLineSegment(sketch, "E61.3", {"start": v(79.8, 3.67) * mm, "end": v(79.8, 37.12) * mm});
            skSolve(sketch);
        }
        {
            var Q0;
            Q0=makeQuery(id+"F29.imprint","IMPRINT",FACE,{"disambiguationData":[TD([[makeQuery(id+"F29.imprint","IMPRINT",EDGE,{"derivedFrom":sQuery(id+"F29.wireOp",EDGE,"E61.0")}),1.0]])]});
            extrude(context, id + "F30", {"entities" : qUnion([Q0]), "operationType" : NewBodyOperationType.REMOVE, "oppositeDirection" : true, "depth" : 5.7 * mm, "offsetDistance" : 25.4 * mm});
        }
        {
            var Q0;
            Q0=makeQuery(id+"F22.opExtrude","SWEPT_FACE",FACE,{"disambiguationData":[OSD([sQuery(id+"F21.wireOp",EDGE,"E56.top")])]});
            var sketch = newSketch(context, id + "F31", { "sketchPlane" : qUnion([Q0])});
            skLineSegment(sketch, "E62.bottom", {"start": v(103.17, 3.18) * mm, "end": v(147.62, 3.18) * mm});
            skLineSegment(sketch, "E62.top", {"start": v(103.17, 17.48) * mm, "end": v(147.62, 17.48) * mm});
            skLineSegment(sketch, "E62.left", {"start": v(103.17, 3.17) * mm, "end": v(103.17, 17.48) * mm});
            skLineSegment(sketch, "E62.right", {"start": v(147.62, 3.18) * mm, "end": v(147.62, 17.48) * mm});
            skLineSegment(sketch, "E63", {"start": v(125.4, 6) * mm, "end": v(124.34, 16.54) * mm, "construction": true});
            skLineSegment(sketch, "E64", {"start": v(125.4, 17.48) * mm, "end": v(125.4, 3.18) * mm, "construction": true});
            skSolve(sketch);
        }
        {
            var Q0;
            Q0=makeQuery(id+"F27.opExtrude","SWEPT_FACE",FACE,{"disambiguationData":[OSD([sQuery(id+"F26.wireOp",EDGE,"E60.top")])]});
            var sketch = newSketch(context, id + "F32", { "sketchPlane" : qUnion([Q0])});
            skLineSegment(sketch, "E65.bottom", {"start": v(29.96, 3.18) * mm, "end": v(74.4, 3.18) * mm});
            skLineSegment(sketch, "E65.top", {"start": v(29.96, 17.48) * mm, "end": v(74.4, 17.48) * mm});
            skLineSegment(sketch, "E65.left", {"start": v(29.96, 3.17) * mm, "end": v(29.96, 17.48) * mm});
            skLineSegment(sketch, "E65.right", {"start": v(74.4, 3.18) * mm, "end": v(74.4, 17.48) * mm});
            skPoint(sketch, "E66.orphan", {"position": v(52.18, 17.48) * mm});
            skPoint(sketch, "E67.start.orphan", {"position": v(52.18, 3.18) * mm});
            skSolve(sketch);
        }
        {
            var Q0;
            {var subQ0=sQuery(id+"F31.wireOp",EDGE,"E62.top");Q0=makeQuery(id+"F31.imprint","IMPRINT",FACE,{"disambiguationData":[TD([[makeQuery(id+"F31.imprint","IMPRINT",EDGE,{"derivedFrom":subQ0}),-1.0]])]});}
            var Q1;
            {var subQ0=sQuery(id+"F32.wireOp",EDGE,"E65.top");Q1=makeQuery(id+"F32.imprint","IMPRINT",FACE,{"disambiguationData":[TD([[makeQuery(id+"F32.imprint","IMPRINT",EDGE,{"derivedFrom":subQ0}),-1.0]])]});}
            extrude(context, id + "F33", {"entities" : qUnion([Q0, Q1]), "operationType" : NewBodyOperationType.ADD, "oppositeDirection" : true, "depth" : 2.3 * mm, "offsetDistance" : 25.4 * mm});
        }
        {
            var Q0;
            {var subQ0=sQuery(id+"F21.wireOp",EDGE,"E56.top");Q0=makeQuery(id+"F33.boolean.opBoolean","MERGE",FACE,{"derivedFrom":[makeQuery(id+"F22.opExtrude","SWEPT_FACE",FACE,{"disambiguationData":[OSD([subQ0])]}),makeQuery(id+"F33.opExtrude","CAP_FACE",FACE,{"disambiguationData":[OSD([subQ0,sQuery(id+"F31.wireOp",EDGE,"E62.top"),sQuery(id+"F31.wireOp",EDGE,"E62.left"),sQuery(id+"F31.wireOp",EDGE,"E62.right")])],"isStart":true})]});}
            var sketch = newSketch(context, id + "F34", { "sketchPlane" : qUnion([Q0])});
            skArc(sketch, "E68", {"start": v(103.17, 6) * mm, "mid": v(105.54, 3.9) * mm, "end": v(108.64, 3.17) * mm});
            skArc(sketch, "E69", {"start": v(142.16, 3.18) * mm, "mid": v(145.26, 3.9) * mm, "end": v(147.62, 6) * mm});
            skLineSegment(sketch, "E70", {"start": v(108.64, 3.17) * mm, "end": v(142.16, 3.18) * mm});
            skLineSegment(sketch, "E71", {"start": v(147.62, 6) * mm, "end": v(147.62, 17.48) * mm});
            skLineSegment(sketch, "E72", {"start": v(147.62, 17.48) * mm, "end": v(103.17, 17.48) * mm});
            skLineSegment(sketch, "E73", {"start": v(103.17, 17.48) * mm, "end": v(103.17, 6) * mm});
            skSolve(sketch);
        }
        {
            var Q0;
            {var subQ0=sQuery(id+"F26.wireOp",EDGE,"E60.top");Q0=makeQuery(id+"F33.boolean.opBoolean","MERGE",FACE,{"derivedFrom":[makeQuery(id+"F27.opExtrude","SWEPT_FACE",FACE,{"disambiguationData":[OSD([subQ0])]}),makeQuery(id+"F33.opExtrude","CAP_FACE",FACE,{"disambiguationData":[OSD([subQ0,sQuery(id+"F32.wireOp",EDGE,"E65.top"),sQuery(id+"F32.wireOp",EDGE,"E65.left"),sQuery(id+"F32.wireOp",EDGE,"E65.right")])],"isStart":true})]});}
            var sketch = newSketch(context, id + "F35", { "sketchPlane" : qUnion([Q0])});
            skPoint(sketch, "E74.end.orphan", {"position": v(35.42, 3.18) * mm});
            skArc(sketch, "E75", {"start": v(29.96, 6.02) * mm, "mid": v(32.33, 3.9) * mm, "end": v(35.42, 3.17) * mm});
            skPoint(sketch, "E76.start.orphan", {"position": v(68.95, 3.18) * mm});
            skArc(sketch, "E77", {"start": v(68.95, 3.18) * mm, "mid": v(72.04, 3.9) * mm, "end": v(74.4, 6.02) * mm});
            skLineSegment(sketch, "E78", {"start": v(35.42, 3.18) * mm, "end": v(68.95, 3.18) * mm});
            skLineSegment(sketch, "E79", {"start": v(74.4, 6.02) * mm, "end": v(74.4, 17.48) * mm});
            skLineSegment(sketch, "E80", {"start": v(74.4, 17.48) * mm, "end": v(29.96, 17.48) * mm});
            skLineSegment(sketch, "E81", {"start": v(29.96, 17.48) * mm, "end": v(29.96, 6.02) * mm});
            skSolve(sketch);
        }
        {
            var Q0;
            {var subQ0=sQuery(id+"F35.wireOp",EDGE,"E78");Q0=makeQuery(id+"F35.imprint","IMPRINT",FACE,{"disambiguationData":[TD([[makeQuery(id+"F35.imprint","IMPRINT",EDGE,{"derivedFrom":subQ0}),-1.0]])]});}
            extrude(context, id + "F36", {"entities" : qUnion([Q0]), "operationType" : NewBodyOperationType.REMOVE, "oppositeDirection" : true, "depth" : 2.54 * mm, "offsetDistance" : 25.4 * mm});
        }
        {
            var Q0;
            {var subQ0=sQuery(id+"F34.wireOp",EDGE,"E70");Q0=makeQuery(id+"F34.imprint","IMPRINT",FACE,{"disambiguationData":[TD([[makeQuery(id+"F34.imprint","IMPRINT",EDGE,{"derivedFrom":subQ0}),-1.0]])]});}
            extrude(context, id + "F37", {"entities" : qUnion([Q0]), "operationType" : NewBodyOperationType.REMOVE, "oppositeDirection" : true, "depth" : 2.54 * mm, "offsetDistance" : 25.4 * mm});
        }
        {
            var Q0;
            Q0=makeQuery(id+"F37.boolean.opBoolean","MERGE",FACE,{"derivedFrom":[makeQuery(id+"F36.boolean.opBoolean","MERGE",FACE,{"derivedFrom":[makeQuery(id+"F1.opExtrude","CAP_FACE",FACE,{"disambiguationData":[OSD([sQuery(id+"F0.wireOp",EDGE,"E0.bottom"),sQuery(id+"F0.wireOp",EDGE,"E0.top"),sQuery(id+"F0.wireOp",EDGE,"E0.left"),sQuery(id+"F0.wireOp",EDGE,"E0.right")])],"isStart":false}),makeQuery(id+"F36.opExtrude","SWEPT_FACE",FACE,{"disambiguationData":[OSD([sQuery(id+"F26.wireOp",EDGE,"E60.top"),sQuery(id+"F35.wireOp",EDGE,"E78")])]})]}),makeQuery(id+"F37.opExtrude","SWEPT_FACE",FACE,{"disambiguationData":[OSD([sQuery(id+"F21.wireOp",EDGE,"E56.top"),sQuery(id+"F34.wireOp",EDGE,"E70")])]})]});
            var sketch = newSketch(context, id + "F38", { "sketchPlane" : qUnion([Q0])});
            skLineSegment(sketch, "E82.bottom", {"start": v(8.62, 38.98) * mm, "end": v(-50.44, 38.98) * mm});
            skLineSegment(sketch, "E82.top", {"start": v(8.62, -16.01) * mm, "end": v(-50.44, -16.01) * mm});
            skLineSegment(sketch, "E82.left", {"start": v(8.62, 38.98) * mm, "end": v(8.62, -16.01) * mm});
            skLineSegment(sketch, "E82.right", {"start": v(-50.44, 38.98) * mm, "end": v(-50.44, -16.01) * mm});
            skSolve(sketch);
        }
        {
            var Q0;
            Q0=makeQuery(id+"F38.imprint","IMPRINT",FACE,{"disambiguationData":[TD([[makeQuery(id+"F38.imprint","IMPRINT",EDGE,{"derivedFrom":sQuery(id+"F38.wireOp",EDGE,"E82.bottom")}),1.0]])]});
            extrude(context, id + "F39", {"entities" : qUnion([Q0]), "operationType" : NewBodyOperationType.ADD, "depth" : 2.84 * mm, "offsetDistance" : 25.4 * mm});
        }
        {
            var Q0;
            Q0=makeQuery(id+"F39.opExtrude","SWEPT_EDGE",EDGE,{"disambiguationData":[OSD([sQuery(id+"F38.wireOp",EDGE,"E82.top"),sQuery(id+"F38.wireOp",EDGE,"E82.left")])]});
            var Q1;
            Q1=makeQuery(id+"F39.opExtrude","SWEPT_EDGE",EDGE,{"disambiguationData":[OSD([sQuery(id+"F38.wireOp",EDGE,"E82.top"),sQuery(id+"F38.wireOp",EDGE,"E82.right")])]});
            var Q2;
            Q2=makeQuery(id+"F39.opExtrude","SWEPT_EDGE",EDGE,{"disambiguationData":[OSD([sQuery(id+"F38.wireOp",EDGE,"E82.bottom"),sQuery(id+"F38.wireOp",EDGE,"E82.left")])]});
            var Q3;
            Q3=makeQuery(id+"F39.opExtrude","SWEPT_EDGE",EDGE,{"disambiguationData":[OSD([sQuery(id+"F38.wireOp",EDGE,"E82.bottom"),sQuery(id+"F38.wireOp",EDGE,"E82.right")])]});
            fillet(context, id + "F40", {"entities" : qUnion([Q0, Q1, Q2, Q3]), "radius" : 1.27 * mm, "tangentPropagation" : true, "allowEdgeOverflow" : false});
        }
        {
            var Q0;
            Q0=makeQuery(id+"F39.opExtrude","CAP_FACE",FACE,{"disambiguationData":[OSD([sQuery(id+"F38.wireOp",EDGE,"E82.bottom"),sQuery(id+"F38.wireOp",EDGE,"E82.top"),sQuery(id+"F38.wireOp",EDGE,"E82.left"),sQuery(id+"F38.wireOp",EDGE,"E82.right")])],"isStart":false});
            var sketch = newSketch(context, id + "F41", { "sketchPlane" : qUnion([Q0])});
            skLineSegment(sketch, "E83.bottom", {"start": v(-48.6, 37.12) * mm, "end": v(6.77, 37.12) * mm});
            skLineSegment(sketch, "E83.top", {"start": v(-48.6, -14.16) * mm, "end": v(6.77, -14.16) * mm});
            skLineSegment(sketch, "E83.left", {"start": v(-48.6, 37.12) * mm, "end": v(-48.6, -14.16) * mm});
            skLineSegment(sketch, "E83.right", {"start": v(6.77, 37.12) * mm, "end": v(6.77, -14.16) * mm});
            skSolve(sketch);
        }
        {
            var Q0;
            Q0=makeQuery(id+"F41.imprint","IMPRINT",FACE,{"disambiguationData":[TD([[makeQuery(id+"F41.imprint","IMPRINT",EDGE,{"derivedFrom":sQuery(id+"F41.wireOp",EDGE,"E83.bottom")}),-1.0]])]});
            extrude(context, id + "F42", {"entities" : qUnion([Q0]), "operationType" : NewBodyOperationType.REMOVE, "oppositeDirection" : true, "depth" : 5.7 * mm, "offsetDistance" : 25.4 * mm});
        }
        {
            var Q0;
            Q0=makeQuery(id+"F37.boolean.opBoolean","MERGE",FACE,{"derivedFrom":[makeQuery(id+"F36.boolean.opBoolean","MERGE",FACE,{"derivedFrom":[makeQuery(id+"F1.opExtrude","CAP_FACE",FACE,{"disambiguationData":[OSD([sQuery(id+"F0.wireOp",EDGE,"E0.bottom"),sQuery(id+"F0.wireOp",EDGE,"E0.top"),sQuery(id+"F0.wireOp",EDGE,"E0.left"),sQuery(id+"F0.wireOp",EDGE,"E0.right")])],"isStart":false}),makeQuery(id+"F36.opExtrude","SWEPT_FACE",FACE,{"disambiguationData":[OSD([sQuery(id+"F26.wireOp",EDGE,"E60.top"),sQuery(id+"F35.wireOp",EDGE,"E78")])]})]}),makeQuery(id+"F37.opExtrude","SWEPT_FACE",FACE,{"disambiguationData":[OSD([sQuery(id+"F21.wireOp",EDGE,"E56.top"),sQuery(id+"F34.wireOp",EDGE,"E70")])]})]});
            var sketch = newSketch(context, id + "F43", { "sketchPlane" : qUnion([Q0])});
            skLineSegment(sketch, "E84.bottom", {"start": v(-64.54, 38.98) * mm, "end": v(-153.44, 38.98) * mm});
            skLineSegment(sketch, "E84.top", {"start": v(-64.54, -40.4) * mm, "end": v(-100.58, -40.4) * mm});
            skLineSegment(sketch, "E84.left", {"start": v(-64.54, 38.98) * mm, "end": v(-64.54, -40.4) * mm});
            skLineSegment(sketch, "E84.right", {"start": v(-153.44, 38.98) * mm, "end": v(-153.44, -40.4) * mm});
            skLineSegment(sketch, "E85.top", {"start": v(-117.37, -31.61) * mm, "end": v(-100.58, -31.61) * mm});
            skLineSegment(sketch, "E85.left", {"start": v(-117.37, -40.4) * mm, "end": v(-117.37, -31.61) * mm});
            skLineSegment(sketch, "E85.right", {"start": v(-100.58, -40.4) * mm, "end": v(-100.58, -31.61) * mm});
            skLineSegment(sketch, "E86.trimOffspring", {"start": v(-117.37, -40.4) * mm, "end": v(-153.44, -40.4) * mm});
            skSolve(sketch);
        }
        {
            var Q0;
            Q0=makeQuery(id+"F43.imprint","IMPRINT",FACE,{"disambiguationData":[TD([[makeQuery(id+"F43.imprint","IMPRINT",EDGE,{"derivedFrom":sQuery(id+"F43.wireOp",EDGE,"E84.bottom")}),1.0]])]});
            extrude(context, id + "F44", {"entities" : qUnion([Q0]), "operationType" : NewBodyOperationType.ADD, "depth" : 2.84 * mm, "offsetDistance" : 25.4 * mm});
        }
        {
            var Q0;
            Q0=makeQuery(id+"F44.opExtrude","SWEPT_EDGE",EDGE,{"disambiguationData":[OSD([sQuery(id+"F43.wireOp",EDGE,"E84.top"),sQuery(id+"F43.wireOp",EDGE,"E84.left")])]});
            var Q1;
            Q1=makeQuery(id+"F44.opExtrude","SWEPT_EDGE",EDGE,{"disambiguationData":[OSD([sQuery(id+"F43.wireOp",EDGE,"E84.top"),sQuery(id+"F43.wireOp",EDGE,"E85.right")])]});
            var Q2;
            Q2=makeQuery(id+"F44.opExtrude","SWEPT_EDGE",EDGE,{"disambiguationData":[OSD([sQuery(id+"F43.wireOp",EDGE,"E85.top"),sQuery(id+"F43.wireOp",EDGE,"E85.right")])]});
            var Q3;
            Q3=makeQuery(id+"F44.opExtrude","SWEPT_EDGE",EDGE,{"disambiguationData":[OSD([sQuery(id+"F43.wireOp",EDGE,"E85.top"),sQuery(id+"F43.wireOp",EDGE,"E85.left")])]});
            var Q4;
            Q4=makeQuery(id+"F44.opExtrude","SWEPT_EDGE",EDGE,{"disambiguationData":[OSD([sQuery(id+"F43.wireOp",EDGE,"E85.left"),sQuery(id+"F43.wireOp",EDGE,"E86.trimOffspring")])]});
            var Q5;
            Q5=makeQuery(id+"F44.opExtrude","SWEPT_EDGE",EDGE,{"disambiguationData":[OSD([sQuery(id+"F43.wireOp",EDGE,"E84.right"),sQuery(id+"F43.wireOp",EDGE,"E86.trimOffspring")])]});
            var Q6;
            Q6=makeQuery(id+"F44.opExtrude","SWEPT_EDGE",EDGE,{"disambiguationData":[OSD([sQuery(id+"F43.wireOp",EDGE,"E84.bottom"),sQuery(id+"F43.wireOp",EDGE,"E84.left")])]});
            var Q7;
            Q7=makeQuery(id+"F44.opExtrude","SWEPT_EDGE",EDGE,{"disambiguationData":[OSD([sQuery(id+"F43.wireOp",EDGE,"E84.bottom"),sQuery(id+"F43.wireOp",EDGE,"E84.right")])]});
            fillet(context, id + "F45", {"entities" : qUnion([Q0, Q1, Q2, Q3, Q4, Q5, Q6, Q7]), "radius" : 1.27 * mm, "tangentPropagation" : true, "allowEdgeOverflow" : false});
        }
        {
            var Q0;
            Q0=makeQuery(id+"F44.opExtrude","CAP_FACE",FACE,{"disambiguationData":[OSD([sQuery(id+"F43.wireOp",EDGE,"E84.bottom"),sQuery(id+"F43.wireOp",EDGE,"E84.top"),sQuery(id+"F43.wireOp",EDGE,"E84.left"),sQuery(id+"F43.wireOp",EDGE,"E84.right"),sQuery(id+"F43.wireOp",EDGE,"E85.top"),sQuery(id+"F43.wireOp",EDGE,"E85.left"),sQuery(id+"F43.wireOp",EDGE,"E85.right"),sQuery(id+"F43.wireOp",EDGE,"E86.trimOffspring")])],"isStart":false});
            var sketch = newSketch(context, id + "F46", { "sketchPlane" : qUnion([Q0])});
            skArc(sketch, "E87.0", {"start": v(-101.85, -29.76) * mm, "mid": v(-99.64, -30.67) * mm, "end": v(-98.73, -32.88) * mm});
            skLineSegment(sketch, "E87.1", {"start": v(-116.1, -29.76) * mm, "end": v(-101.85, -29.76) * mm});
            skLineSegment(sketch, "E87.2", {"start": v(-98.73, -32.88) * mm, "end": v(-98.73, -38.54) * mm});
            skArc(sketch, "E87.3", {"start": v(-119.23, -32.88) * mm, "mid": v(-118.31, -30.67) * mm, "end": v(-116.1, -29.76) * mm});
            skLineSegment(sketch, "E87.4", {"start": v(-119.23, -38.54) * mm, "end": v(-119.23, -32.88) * mm});
            skLineSegment(sketch, "E87.5", {"start": v(-151.59, -38.54) * mm, "end": v(-119.23, -38.54) * mm});
            skLineSegment(sketch, "E87.6", {"start": v(-98.73, -38.54) * mm, "end": v(-66.4, -38.54) * mm});
            skLineSegment(sketch, "E87.7", {"start": v(-66.4, -38.54) * mm, "end": v(-66.4, 37.12) * mm});
            skLineSegment(sketch, "E87.8", {"start": v(-66.4, 37.12) * mm, "end": v(-151.59, 37.12) * mm});
            skLineSegment(sketch, "E87.9", {"start": v(-151.59, 37.12) * mm, "end": v(-151.59, -38.54) * mm});
            skSolve(sketch);
        }
        {
            var Q0;
            Q0=makeQuery(id+"F46.imprint","IMPRINT",FACE,{"disambiguationData":[TD([[makeQuery(id+"F46.imprint","IMPRINT",EDGE,{"derivedFrom":sQuery(id+"F46.wireOp",EDGE,"E87.0")}),1.0]])]});
            extrude(context, id + "F47", {"entities" : qUnion([Q0]), "operationType" : NewBodyOperationType.REMOVE, "oppositeDirection" : true, "depth" : 5.7 * mm, "offsetDistance" : 25.4 * mm});
        }
        {
            var Q0;
            Q0=makeQuery(id+"F37.boolean.opBoolean","MERGE",FACE,{"derivedFrom":[makeQuery(id+"F36.boolean.opBoolean","MERGE",FACE,{"derivedFrom":[makeQuery(id+"F1.opExtrude","CAP_FACE",FACE,{"disambiguationData":[OSD([sQuery(id+"F0.wireOp",EDGE,"E0.bottom"),sQuery(id+"F0.wireOp",EDGE,"E0.top"),sQuery(id+"F0.wireOp",EDGE,"E0.left"),sQuery(id+"F0.wireOp",EDGE,"E0.right")])],"isStart":false}),makeQuery(id+"F36.opExtrude","SWEPT_FACE",FACE,{"disambiguationData":[OSD([sQuery(id+"F26.wireOp",EDGE,"E60.top"),sQuery(id+"F35.wireOp",EDGE,"E78")])]})]}),makeQuery(id+"F37.opExtrude","SWEPT_FACE",FACE,{"disambiguationData":[OSD([sQuery(id+"F21.wireOp",EDGE,"E56.top"),sQuery(id+"F34.wireOp",EDGE,"E70")])]})]});
            var sketch = newSketch(context, id + "F48", { "sketchPlane" : qUnion([Q0])});
            skLineSegment(sketch, "E88", {"start": v(63.1, 3.67) * mm, "end": v(52.18, -9.03) * mm});
            skPoint(sketch, "E88.endSnap0", {"position": v(52.18, 3.67) * mm});
            skLineSegment(sketch, "E89", {"start": v(52.18, -9.03) * mm, "end": v(41.26, 3.67) * mm});
            skLineSegment(sketch, "E90", {"start": v(41.26, 3.67) * mm, "end": v(63.1, 3.67) * mm});
            skLineSegment(sketch, "E91", {"start": v(136.33, 3.68) * mm, "end": v(125.4, -9.02) * mm});
            skLineSegment(sketch, "E92", {"start": v(125.4, -9.02) * mm, "end": v(114.48, 3.68) * mm});
            skSolve(sketch);
        }
        {
            var Q0;
            Q0=makeQuery(id+"F48.imprint","IMPRINT",FACE,{"disambiguationData":[TD([[makeQuery(id+"F48.imprint","IMPRINT",EDGE,{"derivedFrom":sQuery(id+"F48.wireOp",EDGE,"E88")}),-1.0]])]});
            var Q1;
            {var subQ0=sQuery(id+"F48.wireOp",EDGE,"E91");Q1=makeQuery(id+"F48.imprint","IMPRINT",FACE,{"disambiguationData":[TD([[makeQuery(id+"F48.imprint","IMPRINT",EDGE,{"derivedFrom":subQ0}),-1.0]])]});}
            extrude(context, id + "F49", {"entities" : qUnion([Q0, Q1]), "operationType" : NewBodyOperationType.REMOVE, "oppositeDirection" : true, "depth" : 0.4 * mm, "offsetDistance" : 25.4 * mm});
        }
        {
            var Q0;
            Q0=makeQuery(id+"F49.boolean.opBoolean","COPY",EDGE,{"derivedFrom":makeQuery(id+"F49.opExtrude","SWEPT_EDGE",EDGE,{"disambiguationData":[OSD([sQuery(id+"F48.wireOp",EDGE,"E91"),sQuery(id+"F48.wireOp",EDGE,"E92")])]})});
            var Q1;
            Q1=makeQuery(id+"F49.boolean.opBoolean","COPY",EDGE,{"derivedFrom":makeQuery(id+"F49.opExtrude","SWEPT_EDGE",EDGE,{"disambiguationData":[OSD([sQuery(id+"F48.wireOp",EDGE,"E88"),sQuery(id+"F48.wireOp",EDGE,"E89")])]})});
            fillet(context, id + "F50", {"entities" : qUnion([Q0, Q1]), "radius" : 6.35 * mm, "tangentPropagation" : true, "allowEdgeOverflow" : false});
        }
        {
            var Q0;
            Q0=makeQuery(id+"F37.boolean.opBoolean","MERGE",FACE,{"derivedFrom":[makeQuery(id+"F36.boolean.opBoolean","MERGE",FACE,{"derivedFrom":[makeQuery(id+"F1.opExtrude","CAP_FACE",FACE,{"disambiguationData":[OSD([sQuery(id+"F0.wireOp",EDGE,"E0.bottom"),sQuery(id+"F0.wireOp",EDGE,"E0.top"),sQuery(id+"F0.wireOp",EDGE,"E0.left"),sQuery(id+"F0.wireOp",EDGE,"E0.right")])],"isStart":false}),makeQuery(id+"F36.opExtrude","SWEPT_FACE",FACE,{"disambiguationData":[OSD([sQuery(id+"F26.wireOp",EDGE,"E60.top"),sQuery(id+"F35.wireOp",EDGE,"E78")])]})]}),makeQuery(id+"F37.opExtrude","SWEPT_FACE",FACE,{"disambiguationData":[OSD([sQuery(id+"F21.wireOp",EDGE,"E56.top"),sQuery(id+"F34.wireOp",EDGE,"E70")])]})]});
            var sketch = newSketch(context, id + "F51", { "sketchPlane" : qUnion([Q0])});
            skCircle(sketch, "E93", {"center": v(-57.4, 34.24) * mm, "radius": 4.76 * mm});
            skCircle(sketch, "E94", {"center": v(-57.4, -7.04) * mm, "radius": 4.76 * mm});
            skCircle(sketch, "E95", {"center": v(15.77, -7.05) * mm, "radius": 4.76 * mm});
            skCircle(sketch, "E96", {"center": v(15.77, 34.23) * mm, "radius": 4.76 * mm});
            skCircle(sketch, "E97", {"center": v(88.8, 34.24) * mm, "radius": 4.76 * mm});
            skCircle(sketch, "E98", {"center": v(88.8, -7.04) * mm, "radius": 4.76 * mm});
            skCircle(sketch, "E99", {"center": v(147.71, -7.13) * mm, "radius": 4.76 * mm});
            skLineSegment(sketch, "E100", {"start": v(16.63, -2.36) * mm, "end": v(152.77, -2.36) * mm, "construction": true});
            skSolve(sketch);
        }
        {
            var Q0;
            Q0=makeQuery(id+"F51.imprint","IMPRINT",FACE,{"disambiguationData":[TD([[makeQuery(id+"F51.imprint","IMPRINT",EDGE,{"derivedFrom":sQuery(id+"F51.wireOp",EDGE,"E93")}),1.0]])]});
            var Q1;
            Q1=makeQuery(id+"F51.imprint","IMPRINT",FACE,{"disambiguationData":[TD([[makeQuery(id+"F51.imprint","IMPRINT",EDGE,{"derivedFrom":sQuery(id+"F51.wireOp",EDGE,"E94")}),1.0]])]});
            var Q2;
            Q2=makeQuery(id+"F51.imprint","IMPRINT",FACE,{"disambiguationData":[TD([[makeQuery(id+"F51.imprint","IMPRINT",EDGE,{"derivedFrom":sQuery(id+"F51.wireOp",EDGE,"E96")}),1.0]])]});
            var Q3;
            Q3=makeQuery(id+"F51.imprint","IMPRINT",FACE,{"disambiguationData":[TD([[makeQuery(id+"F51.imprint","IMPRINT",EDGE,{"derivedFrom":sQuery(id+"F51.wireOp",EDGE,"E95")}),1.0]])]});
            var Q4;
            Q4=makeQuery(id+"F51.imprint","IMPRINT",FACE,{"disambiguationData":[TD([[makeQuery(id+"F51.imprint","IMPRINT",EDGE,{"derivedFrom":sQuery(id+"F51.wireOp",EDGE,"E98")}),1.0]])]});
            var Q5;
            Q5=makeQuery(id+"F51.imprint","IMPRINT",FACE,{"disambiguationData":[TD([[makeQuery(id+"F51.imprint","IMPRINT",EDGE,{"derivedFrom":sQuery(id+"F51.wireOp",EDGE,"E97")}),1.0]])]});
            var Q6;
            Q6=makeQuery(id+"F51.imprint","IMPRINT",FACE,{"disambiguationData":[TD([[makeQuery(id+"F51.imprint","IMPRINT",EDGE,{"derivedFrom":sQuery(id+"F51.wireOp",EDGE,"E99")}),1.0]])]});
            extrude(context, id + "F52", {"entities" : qUnion([Q0, Q1, Q2, Q3, Q4, Q5, Q6]), "operationType" : NewBodyOperationType.REMOVE, "oppositeDirection" : true, "depth" : 0.4 * mm, "offsetDistance" : 25.4 * mm});
        }
        {
            var Q0;
            Q0=makeQuery(id+"F37.boolean.opBoolean","MERGE",FACE,{"derivedFrom":[makeQuery(id+"F36.boolean.opBoolean","MERGE",FACE,{"derivedFrom":[makeQuery(id+"F1.opExtrude","CAP_FACE",FACE,{"disambiguationData":[OSD([sQuery(id+"F0.wireOp",EDGE,"E0.bottom"),sQuery(id+"F0.wireOp",EDGE,"E0.top"),sQuery(id+"F0.wireOp",EDGE,"E0.left"),sQuery(id+"F0.wireOp",EDGE,"E0.right")])],"isStart":false}),makeQuery(id+"F36.opExtrude","SWEPT_FACE",FACE,{"disambiguationData":[OSD([sQuery(id+"F26.wireOp",EDGE,"E60.top"),sQuery(id+"F35.wireOp",EDGE,"E78")])]})]}),makeQuery(id+"F37.opExtrude","SWEPT_FACE",FACE,{"disambiguationData":[OSD([sQuery(id+"F21.wireOp",EDGE,"E56.top"),sQuery(id+"F34.wireOp",EDGE,"E70")])]})]});
            var sketch = newSketch(context, id + "F53", { "sketchPlane" : qUnion([Q0])});
            skCircle(sketch, "E101", {"center": v(-108.98, -37.17) * mm, "radius": 2.39 * mm});
            skPoint(sketch, "E101.centerSnap0", {"position": v(-108.98, -31.61) * mm});
            skSolve(sketch);
        }
        {
            var Q0;
            Q0=makeQuery(id+"F53.imprint","IMPRINT",FACE,{"disambiguationData":[TD([[makeQuery(id+"F53.imprint","IMPRINT",EDGE,{"derivedFrom":sQuery(id+"F53.wireOp",EDGE,"E101")}),1.0]])]});
            extrude(context, id + "F54", {"entities" : qUnion([Q0]), "operationType" : NewBodyOperationType.REMOVE, "oppositeDirection" : true, "depth" : 2.54 * mm, "offsetDistance" : 25.4 * mm});
        }
        {
            var Q0;
            Q0=makeQuery(id+"F37.boolean.opBoolean","MERGE",FACE,{"derivedFrom":[makeQuery(id+"F36.boolean.opBoolean","MERGE",FACE,{"derivedFrom":[makeQuery(id+"F1.opExtrude","CAP_FACE",FACE,{"disambiguationData":[OSD([sQuery(id+"F0.wireOp",EDGE,"E0.bottom"),sQuery(id+"F0.wireOp",EDGE,"E0.top"),sQuery(id+"F0.wireOp",EDGE,"E0.left"),sQuery(id+"F0.wireOp",EDGE,"E0.right")])],"isStart":false}),makeQuery(id+"F36.opExtrude","SWEPT_FACE",FACE,{"disambiguationData":[OSD([sQuery(id+"F26.wireOp",EDGE,"E60.top"),sQuery(id+"F35.wireOp",EDGE,"E78")])]})]}),makeQuery(id+"F37.opExtrude","SWEPT_FACE",FACE,{"disambiguationData":[OSD([sQuery(id+"F21.wireOp",EDGE,"E56.top"),sQuery(id+"F34.wireOp",EDGE,"E70")])]})]});
            var sketch = newSketch(context, id + "F55", { "sketchPlane" : qUnion([Q0])});
            skLineSegment(sketch, "E102.bottom", {"start": v(-29.34, -24.7) * mm, "end": v(138.93, -24.7) * mm});
            skLineSegment(sketch, "E102.top", {"start": v(-29.34, -40.58) * mm, "end": v(138.93, -40.58) * mm});
            skLineSegment(sketch, "E103", {"start": v(-29.34, -40.58) * mm, "end": v(-42.04, -32.64) * mm});
            skPoint(sketch, "E103.endSnap0", {"position": v(-29.34, -32.64) * mm});
            skLineSegment(sketch, "E104", {"start": v(-42.04, -32.64) * mm, "end": v(-29.34, -24.7) * mm});
            skLineSegment(sketch, "E105", {"start": v(138.93, -40.58) * mm, "end": v(151.63, -32.64) * mm});
            skPoint(sketch, "E105.endSnap0", {"position": v(138.93, -32.64) * mm});
            skLineSegment(sketch, "E106", {"start": v(151.63, -32.64) * mm, "end": v(138.93, -24.7) * mm});
            skSolve(sketch);
        }
        {
            var Q0;
            Q0=makeQuery(id+"F55.imprint","IMPRINT",FACE,{"disambiguationData":[TD([[makeQuery(id+"F55.imprint","IMPRINT",EDGE,{"derivedFrom":sQuery(id+"F55.wireOp",EDGE,"E102.bottom")}),-1.0]])]});
            extrude(context, id + "F56", {"entities" : qUnion([Q0]), "operationType" : NewBodyOperationType.ADD, "depth" : 2.84 * mm, "offsetDistance" : 25.4 * mm});
        }
        {
            var Q0;
            Q0=makeQuery(id+"F56.opExtrude","SWEPT_EDGE",EDGE,{"disambiguationData":[OSD([sQuery(id+"F55.wireOp",EDGE,"E103"),sQuery(id+"F55.wireOp",EDGE,"E104")])]});
            var Q1;
            Q1=makeQuery(id+"F56.opExtrude","SWEPT_EDGE",EDGE,{"disambiguationData":[OSD([sQuery(id+"F55.wireOp",EDGE,"E102.top"),sQuery(id+"F55.wireOp",EDGE,"E103")])]});
            var Q2;
            Q2=makeQuery(id+"F56.opExtrude","SWEPT_EDGE",EDGE,{"disambiguationData":[OSD([sQuery(id+"F55.wireOp",EDGE,"E102.bottom"),sQuery(id+"F55.wireOp",EDGE,"E104")])]});
            var Q3;
            Q3=makeQuery(id+"F56.opExtrude","SWEPT_EDGE",EDGE,{"disambiguationData":[OSD([sQuery(id+"F55.wireOp",EDGE,"E105"),sQuery(id+"F55.wireOp",EDGE,"E106")])]});
            var Q4;
            Q4=makeQuery(id+"F56.opExtrude","SWEPT_EDGE",EDGE,{"disambiguationData":[OSD([sQuery(id+"F55.wireOp",EDGE,"E102.top"),sQuery(id+"F55.wireOp",EDGE,"E105")])]});
            var Q5;
            Q5=makeQuery(id+"F56.opExtrude","SWEPT_EDGE",EDGE,{"disambiguationData":[OSD([sQuery(id+"F55.wireOp",EDGE,"E102.bottom"),sQuery(id+"F55.wireOp",EDGE,"E106")])]});
            fillet(context, id + "F57", {"entities" : qUnion([Q0, Q1, Q2, Q3, Q4, Q5]), "radius" : 1.27 * mm, "tangentPropagation" : true, "allowEdgeOverflow" : false});
        }
        {
            var Q0;
            Q0=makeQuery(id+"F56.opExtrude","CAP_FACE",FACE,{"disambiguationData":[OSD([sQuery(id+"F55.wireOp",EDGE,"E102.bottom"),sQuery(id+"F55.wireOp",EDGE,"E102.top"),sQuery(id+"F55.wireOp",EDGE,"E103"),sQuery(id+"F55.wireOp",EDGE,"E104"),sQuery(id+"F55.wireOp",EDGE,"E105"),sQuery(id+"F55.wireOp",EDGE,"E106")])],"isStart":false});
            var sketch = newSketch(context, id + "F58", { "sketchPlane" : qUnion([Q0])});
            skLineSegment(sketch, "E107", {"start": v(54.8, -24.7) * mm, "end": v(54.8, -40.58) * mm, "construction": true});
            skLineSegment(sketch, "E108.bottom", {"start": v(67.5, -26.56) * mm, "end": v(42.1, -26.56) * mm});
            skLineSegment(sketch, "E108.top", {"start": v(67.5, -38.72) * mm, "end": v(42.1, -38.72) * mm});
            skLineSegment(sketch, "E108.left", {"start": v(67.5, -26.56) * mm, "end": v(67.5, -38.72) * mm});
            skLineSegment(sketch, "E108.right", {"start": v(42.1, -26.56) * mm, "end": v(42.1, -38.72) * mm});
            skPoint(sketch, "E108.middle", {"position": v(54.8, -32.64) * mm});
            skLineSegment(sketch, "E109.bottom", {"start": v(69.35, -26.56) * mm, "end": v(136.56, -26.56) * mm});
            skLineSegment(sketch, "E109.top", {"start": v(69.35, -38.72) * mm, "end": v(136.56, -38.72) * mm});
            skLineSegment(sketch, "E109.left", {"start": v(69.35, -26.56) * mm, "end": v(69.35, -38.72) * mm});
            skLineSegment(sketch, "E109.right", {"start": v(136.56, -26.56) * mm, "end": v(136.56, -38.72) * mm});
            skLineSegment(sketch, "E110.bottom", {"start": v(40.24, -26.56) * mm, "end": v(-27.12, -26.56) * mm});
            skLineSegment(sketch, "E110.top", {"start": v(40.24, -38.72) * mm, "end": v(-27.12, -38.72) * mm});
            skLineSegment(sketch, "E110.left", {"start": v(40.24, -26.56) * mm, "end": v(40.24, -38.72) * mm});
            skLineSegment(sketch, "E110.right", {"start": v(-27.12, -26.56) * mm, "end": v(-27.12, -38.72) * mm});
            skLineSegment(sketch, "E111", {"start": v(138.42, -38.72) * mm, "end": v(138.42, -26.56) * mm});
            skLineSegment(sketch, "E112", {"start": v(138.42, -26.56) * mm, "end": v(148.12, -32.64) * mm});
            skPoint(sketch, "E112.endSnap0", {"position": v(138.42, -32.64) * mm});
            skLineSegment(sketch, "E113", {"start": v(148.12, -32.64) * mm, "end": v(138.42, -38.72) * mm});
            skLineSegment(sketch, "E114", {"start": v(-28.98, -38.72) * mm, "end": v(-28.98, -26.56) * mm});
            skLineSegment(sketch, "E115", {"start": v(-28.98, -26.56) * mm, "end": v(-38.4, -32.64) * mm});
            skPoint(sketch, "E115.endSnap0", {"position": v(-27.12, -32.64) * mm});
            skLineSegment(sketch, "E116", {"start": v(-38.4, -32.64) * mm, "end": v(-28.98, -38.72) * mm});
            skSolve(sketch);
        }
        {
            var Q0;
            Q0=makeQuery(id+"F58.imprint","IMPRINT",FACE,{"disambiguationData":[TD([[makeQuery(id+"F58.imprint","IMPRINT",EDGE,{"derivedFrom":sQuery(id+"F58.wireOp",EDGE,"E114")}),1.0]])]});
            var Q1;
            Q1=makeQuery(id+"F58.imprint","IMPRINT",FACE,{"disambiguationData":[TD([[makeQuery(id+"F58.imprint","IMPRINT",EDGE,{"derivedFrom":sQuery(id+"F58.wireOp",EDGE,"E110.bottom")}),1.0]])]});
            var Q2;
            Q2=makeQuery(id+"F58.imprint","IMPRINT",FACE,{"disambiguationData":[TD([[makeQuery(id+"F58.imprint","IMPRINT",EDGE,{"derivedFrom":sQuery(id+"F58.wireOp",EDGE,"E108.bottom")}),1.0]])]});
            var Q3;
            Q3=makeQuery(id+"F58.imprint","IMPRINT",FACE,{"disambiguationData":[TD([[makeQuery(id+"F58.imprint","IMPRINT",EDGE,{"derivedFrom":sQuery(id+"F58.wireOp",EDGE,"E109.bottom")}),-1.0]])]});
            var Q4;
            Q4=makeQuery(id+"F58.imprint","IMPRINT",FACE,{"disambiguationData":[TD([[makeQuery(id+"F58.imprint","IMPRINT",EDGE,{"derivedFrom":sQuery(id+"F58.wireOp",EDGE,"E111")}),-1.0]])]});
            extrude(context, id + "F59", {"entities" : qUnion([Q0, Q1, Q2, Q3, Q4]), "operationType" : NewBodyOperationType.REMOVE, "oppositeDirection" : true, "depth" : 5.7 * mm, "offsetDistance" : 25.4 * mm});
        }
        {
            var Q0;
            Q0=makeQuery(id+"F59.boolean.opBoolean","COPY",EDGE,{"derivedFrom":makeQuery(id+"F59.opExtrude","SWEPT_EDGE",EDGE,{"disambiguationData":[OSD([sQuery(id+"F58.wireOp",EDGE,"E115"),sQuery(id+"F58.wireOp",EDGE,"E116")])]})});
            var Q1;
            Q1=makeQuery(id+"F59.boolean.opBoolean","COPY",EDGE,{"derivedFrom":makeQuery(id+"F59.opExtrude","SWEPT_EDGE",EDGE,{"disambiguationData":[OSD([sQuery(id+"F58.wireOp",EDGE,"E114"),sQuery(id+"F58.wireOp",EDGE,"E116")])]})});
            var Q2;
            Q2=makeQuery(id+"F59.boolean.opBoolean","COPY",EDGE,{"derivedFrom":makeQuery(id+"F59.opExtrude","SWEPT_EDGE",EDGE,{"disambiguationData":[OSD([sQuery(id+"F58.wireOp",EDGE,"E114"),sQuery(id+"F58.wireOp",EDGE,"E115")])]})});
            var Q3;
            Q3=makeQuery(id+"F59.boolean.opBoolean","COPY",EDGE,{"derivedFrom":makeQuery(id+"F59.opExtrude","SWEPT_EDGE",EDGE,{"disambiguationData":[OSD([sQuery(id+"F58.wireOp",EDGE,"E110.bottom"),sQuery(id+"F58.wireOp",EDGE,"E110.right")])]})});
            var Q4;
            Q4=makeQuery(id+"F59.boolean.opBoolean","COPY",EDGE,{"derivedFrom":makeQuery(id+"F59.opExtrude","SWEPT_EDGE",EDGE,{"disambiguationData":[OSD([sQuery(id+"F58.wireOp",EDGE,"E110.top"),sQuery(id+"F58.wireOp",EDGE,"E110.right")])]})});
            var Q5;
            Q5=makeQuery(id+"F59.boolean.opBoolean","COPY",EDGE,{"derivedFrom":makeQuery(id+"F59.opExtrude","SWEPT_EDGE",EDGE,{"disambiguationData":[OSD([sQuery(id+"F58.wireOp",EDGE,"E109.top"),sQuery(id+"F58.wireOp",EDGE,"E109.left")])]})});
            var Q6;
            Q6=makeQuery(id+"F59.boolean.opBoolean","COPY",EDGE,{"derivedFrom":makeQuery(id+"F59.opExtrude","SWEPT_EDGE",EDGE,{"disambiguationData":[OSD([sQuery(id+"F58.wireOp",EDGE,"E108.top"),sQuery(id+"F58.wireOp",EDGE,"E108.right")])]})});
            var Q7;
            Q7=makeQuery(id+"F59.boolean.opBoolean","COPY",EDGE,{"derivedFrom":makeQuery(id+"F59.opExtrude","SWEPT_EDGE",EDGE,{"disambiguationData":[OSD([sQuery(id+"F58.wireOp",EDGE,"E108.bottom"),sQuery(id+"F58.wireOp",EDGE,"E108.right")])]})});
            var Q8;
            Q8=makeQuery(id+"F59.boolean.opBoolean","COPY",EDGE,{"derivedFrom":makeQuery(id+"F59.opExtrude","SWEPT_EDGE",EDGE,{"disambiguationData":[OSD([sQuery(id+"F58.wireOp",EDGE,"E109.bottom"),sQuery(id+"F58.wireOp",EDGE,"E109.left")])]})});
            var Q9;
            Q9=makeQuery(id+"F59.boolean.opBoolean","COPY",EDGE,{"derivedFrom":makeQuery(id+"F59.opExtrude","SWEPT_EDGE",EDGE,{"disambiguationData":[OSD([sQuery(id+"F58.wireOp",EDGE,"E108.bottom"),sQuery(id+"F58.wireOp",EDGE,"E108.left")])]})});
            var Q10;
            Q10=makeQuery(id+"F59.boolean.opBoolean","COPY",EDGE,{"derivedFrom":makeQuery(id+"F59.opExtrude","SWEPT_EDGE",EDGE,{"disambiguationData":[OSD([sQuery(id+"F58.wireOp",EDGE,"E110.bottom"),sQuery(id+"F58.wireOp",EDGE,"E110.left")])]})});
            var Q11;
            Q11=makeQuery(id+"F59.boolean.opBoolean","COPY",EDGE,{"derivedFrom":makeQuery(id+"F59.opExtrude","SWEPT_EDGE",EDGE,{"disambiguationData":[OSD([sQuery(id+"F58.wireOp",EDGE,"E110.top"),sQuery(id+"F58.wireOp",EDGE,"E110.left")])]})});
            var Q12;
            Q12=makeQuery(id+"F59.boolean.opBoolean","COPY",EDGE,{"derivedFrom":makeQuery(id+"F59.opExtrude","SWEPT_EDGE",EDGE,{"disambiguationData":[OSD([sQuery(id+"F58.wireOp",EDGE,"E108.top"),sQuery(id+"F58.wireOp",EDGE,"E108.left")])]})});
            var Q13;
            Q13=makeQuery(id+"F59.boolean.opBoolean","COPY",EDGE,{"derivedFrom":makeQuery(id+"F59.opExtrude","SWEPT_EDGE",EDGE,{"disambiguationData":[OSD([sQuery(id+"F58.wireOp",EDGE,"E109.top"),sQuery(id+"F58.wireOp",EDGE,"E109.right")])]})});
            var Q14;
            Q14=makeQuery(id+"F59.boolean.opBoolean","COPY",EDGE,{"derivedFrom":makeQuery(id+"F59.opExtrude","SWEPT_EDGE",EDGE,{"disambiguationData":[OSD([sQuery(id+"F58.wireOp",EDGE,"E109.bottom"),sQuery(id+"F58.wireOp",EDGE,"E109.right")])]})});
            var Q15;
            Q15=makeQuery(id+"F59.boolean.opBoolean","COPY",EDGE,{"derivedFrom":makeQuery(id+"F59.opExtrude","SWEPT_EDGE",EDGE,{"disambiguationData":[OSD([sQuery(id+"F58.wireOp",EDGE,"E112"),sQuery(id+"F58.wireOp",EDGE,"E113")])]})});
            var Q16;
            Q16=makeQuery(id+"F59.boolean.opBoolean","COPY",EDGE,{"derivedFrom":makeQuery(id+"F59.opExtrude","SWEPT_EDGE",EDGE,{"disambiguationData":[OSD([sQuery(id+"F58.wireOp",EDGE,"E111"),sQuery(id+"F58.wireOp",EDGE,"E112")])]})});
            var Q17;
            Q17=makeQuery(id+"F59.boolean.opBoolean","COPY",EDGE,{"derivedFrom":makeQuery(id+"F59.opExtrude","SWEPT_EDGE",EDGE,{"disambiguationData":[OSD([sQuery(id+"F58.wireOp",EDGE,"E111"),sQuery(id+"F58.wireOp",EDGE,"E113")])]})});
            fillet(context, id + "F60", {"entities" : qUnion([Q0, Q1, Q2, Q3, Q4, Q5, Q6, Q7, Q8, Q9, Q10, Q11, Q12, Q13, Q14, Q15, Q16, Q17]), "radius" : 0.25 * mm, "tangentPropagation" : true, "allowEdgeOverflow" : false});
        }
        {
            var Q0;
            Q0=makeQuery(id+"F37.boolean.opBoolean","MERGE",FACE,{"derivedFrom":[makeQuery(id+"F36.boolean.opBoolean","MERGE",FACE,{"derivedFrom":[makeQuery(id+"F1.opExtrude","CAP_FACE",FACE,{"disambiguationData":[OSD([sQuery(id+"F0.wireOp",EDGE,"E0.bottom"),sQuery(id+"F0.wireOp",EDGE,"E0.top"),sQuery(id+"F0.wireOp",EDGE,"E0.left"),sQuery(id+"F0.wireOp",EDGE,"E0.right")])],"isStart":false}),makeQuery(id+"F36.opExtrude","SWEPT_FACE",FACE,{"disambiguationData":[OSD([sQuery(id+"F26.wireOp",EDGE,"E60.top"),sQuery(id+"F35.wireOp",EDGE,"E78")])]})]}),makeQuery(id+"F37.opExtrude","SWEPT_FACE",FACE,{"disambiguationData":[OSD([sQuery(id+"F21.wireOp",EDGE,"E56.top"),sQuery(id+"F34.wireOp",EDGE,"E70")])]})]});
            var sketch = newSketch(context, id + "F61", { "sketchPlane" : qUnion([Q0])});
            skCircle(sketch, "E117", {"center": v(-57.47, -40.58) * mm, "radius": 3.18 * mm});
            skCircle(sketch, "E118", {"center": v(23.9, -43.74) * mm, "radius": 1.59 * mm});
            skCircle(sketch, "E119", {"center": v(39.23, -43.74) * mm, "radius": 1.59 * mm});
            skCircle(sketch, "E120", {"center": v(86.86, -43.74) * mm, "radius": 1.59 * mm});
            skCircle(sketch, "E121", {"center": v(147.88, -38.74) * mm, "radius": 1.59 * mm});
            skCircle(sketch, "E122", {"center": v(-10.07, 43.74) * mm, "radius": 1.59 * mm});
            skCircle(sketch, "E123", {"center": v(5.5, 43.74) * mm, "radius": 1.59 * mm});
            skCircle(sketch, "E124", {"center": v(63.08, 43.74) * mm, "radius": 1.59 * mm});
            skCircle(sketch, "E125", {"center": v(-109, 43.74) * mm, "radius": 1.59 * mm});
            skPoint(sketch, "E125.centerSnap0", {"position": v(-109, 38.98) * mm});
            skSolve(sketch);
        }
        {
            var Q0;
            Q0=makeQuery(id+"F61.imprint","IMPRINT",FACE,{"disambiguationData":[TD([[makeQuery(id+"F61.imprint","IMPRINT",EDGE,{"derivedFrom":sQuery(id+"F61.wireOp",EDGE,"E125")}),1.0]])]});
            var Q1;
            Q1=makeQuery(id+"F61.imprint","IMPRINT",FACE,{"disambiguationData":[TD([[makeQuery(id+"F61.imprint","IMPRINT",EDGE,{"derivedFrom":sQuery(id+"F61.wireOp",EDGE,"E122")}),1.0]])]});
            var Q2;
            Q2=makeQuery(id+"F61.imprint","IMPRINT",FACE,{"disambiguationData":[TD([[makeQuery(id+"F61.imprint","IMPRINT",EDGE,{"derivedFrom":sQuery(id+"F61.wireOp",EDGE,"E123")}),1.0]])]});
            var Q3;
            Q3=makeQuery(id+"F61.imprint","IMPRINT",FACE,{"disambiguationData":[TD([[makeQuery(id+"F61.imprint","IMPRINT",EDGE,{"derivedFrom":sQuery(id+"F61.wireOp",EDGE,"E117")}),1.0]])]});
            var Q4;
            Q4=makeQuery(id+"F61.imprint","IMPRINT",FACE,{"disambiguationData":[TD([[makeQuery(id+"F61.imprint","IMPRINT",EDGE,{"derivedFrom":sQuery(id+"F61.wireOp",EDGE,"E118")}),1.0]])]});
            var Q5;
            Q5=makeQuery(id+"F61.imprint","IMPRINT",FACE,{"disambiguationData":[TD([[makeQuery(id+"F61.imprint","IMPRINT",EDGE,{"derivedFrom":sQuery(id+"F61.wireOp",EDGE,"E119")}),1.0]])]});
            var Q6;
            Q6=makeQuery(id+"F61.imprint","IMPRINT",FACE,{"disambiguationData":[TD([[makeQuery(id+"F61.imprint","IMPRINT",EDGE,{"derivedFrom":sQuery(id+"F61.wireOp",EDGE,"E120")}),1.0]])]});
            var Q7;
            Q7=makeQuery(id+"F61.imprint","IMPRINT",FACE,{"disambiguationData":[TD([[makeQuery(id+"F61.imprint","IMPRINT",EDGE,{"derivedFrom":sQuery(id+"F61.wireOp",EDGE,"E124")}),1.0]])]});
            var Q8;
            Q8=makeQuery(id+"F61.imprint","IMPRINT",FACE,{"disambiguationData":[TD([[makeQuery(id+"F61.imprint","IMPRINT",EDGE,{"derivedFrom":sQuery(id+"F61.wireOp",EDGE,"E121")}),1.0]])]});
            extrude(context, id + "F62", {"entities" : qUnion([Q0, Q1, Q2, Q3, Q4, Q5, Q6, Q7, Q8]), "operationType" : NewBodyOperationType.REMOVE, "oppositeDirection" : true, "depth" : 0.4 * mm, "offsetDistance" : 25.4 * mm});
        }
        {
            var Q0;
            {var subQ0=sQuery(id+"F0.wireOp",EDGE,"E0.bottom");Q0=makeQuery(id+"F5.boolean.opBoolean","MERGE",FACE,{"derivedFrom":[makeQuery(id+"F1.opExtrude","SWEPT_FACE",FACE,{"disambiguationData":[OSD([subQ0])]}),makeQuery(id+"F5.opExtrude","SWEPT_FACE",FACE,{"disambiguationData":[OSD([subQ0])]})]});}
            var sketch = newSketch(context, id + "F63", { "sketchPlane" : qUnion([Q0])});
            skLineSegment(sketch, "E126.bottom", {"start": v(-8.04, 12.7) * mm, "end": v(-1.7, 12.7) * mm});
            skLineSegment(sketch, "E126.top", {"start": v(-8.04, 9.53) * mm, "end": v(-1.7, 9.53) * mm});
            skLineSegment(sketch, "E126.left", {"start": v(-8.04, 12.7) * mm, "end": v(-8.04, 9.53) * mm});
            skLineSegment(sketch, "E126.right", {"start": v(-1.7, 12.7) * mm, "end": v(-1.7, 9.53) * mm});
            skSolve(sketch);
        }
        {
            var Q0;
            Q0=makeQuery(id+"F63.imprint","IMPRINT",FACE,{"disambiguationData":[TD([[makeQuery(id+"F63.imprint","IMPRINT",EDGE,{"derivedFrom":sQuery(id+"F63.wireOp",EDGE,"E126.bottom")}),1.0]])]});
            extrude(context, id + "F64", {"entities" : qUnion([Q0]), "operationType" : NewBodyOperationType.REMOVE, "oppositeDirection" : true, "depth" : 2.54 * mm, "offsetDistance" : 25.4 * mm});
        }
        {
            var Q0;
            {var subQ0=sQuery(id+"F0.wireOp",EDGE,"E0.top");Q0=makeQuery(id+"F5.boolean.opBoolean","MERGE",FACE,{"derivedFrom":[makeQuery(id+"F1.opExtrude","SWEPT_FACE",FACE,{"disambiguationData":[OSD([subQ0])]}),makeQuery(id+"F5.opExtrude","SWEPT_FACE",FACE,{"disambiguationData":[OSD([subQ0])]})]});}
            var sketch = newSketch(context, id + "F65", { "sketchPlane" : qUnion([Q0])});
            skLineSegment(sketch, "E127.bottom", {"start": v(4.01, 12.7) * mm, "end": v(0.84, 12.7) * mm});
            skLineSegment(sketch, "E127.top", {"start": v(4.01, 0) * mm, "end": v(0.84, 0) * mm});
            skLineSegment(sketch, "E127.left", {"start": v(4.01, 12.7) * mm, "end": v(4.01, 0) * mm});
            skLineSegment(sketch, "E127.right", {"start": v(0.84, 12.7) * mm, "end": v(0.84, 0) * mm});
            skSolve(sketch);
        }
        {
            var Q0;
            Q0=makeQuery(id+"F65.imprint","IMPRINT",FACE,{"disambiguationData":[TD([[makeQuery(id+"F65.imprint","IMPRINT",EDGE,{"derivedFrom":sQuery(id+"F65.wireOp",EDGE,"E127.bottom")}),-1.0]])]});
            extrude(context, id + "F66", {"entities" : qUnion([Q0]), "operationType" : NewBodyOperationType.REMOVE, "oppositeDirection" : true, "depth" : 1.27 * mm, "offsetDistance" : 25.4 * mm});
        }
        {
            var Q0;
            {var subQ0=sQuery(id+"F0.wireOp",EDGE,"E0.left");Q0=makeQuery(id+"F5.boolean.opBoolean","MERGE",FACE,{"derivedFrom":[makeQuery(id+"F1.opExtrude","SWEPT_FACE",FACE,{"disambiguationData":[OSD([subQ0])]}),makeQuery(id+"F5.opExtrude","SWEPT_FACE",FACE,{"disambiguationData":[OSD([subQ0])]})]});}
            var sketch = newSketch(context, id + "F67", { "sketchPlane" : qUnion([Q0])});
            skLineSegment(sketch, "E128.top", {"start": v(3.18, 9.53) * mm, "end": v(-3.17, 9.53) * mm});
            skLineSegment(sketch, "E128.left", {"start": v(3.18, 15.88) * mm, "end": v(3.18, 9.53) * mm});
            skLineSegment(sketch, "E128.right", {"start": v(-3.17, 15.88) * mm, "end": v(-3.17, 9.53) * mm});
            skPoint(sketch, "E128.middle", {"position": v(0, 12.7) * mm});
            skSolve(sketch);
        }
        {
            var Q0;
            {var subQ0=sQuery(id+"F67.wireOp",EDGE,"E128.bottom");Q0=makeQuery(id+"F67.imprint","IMPRINT",FACE,{"disambiguationData":[TD([[makeQuery(id+"F67.imprint","IMPRINT",EDGE,{"derivedFrom":subQ0}),1.0]])]});}
            var Q1;
            {var subQ0=sQuery(id+"F67.wireOp",EDGE,"E128.top");Q1=makeQuery(id+"F67.imprint","IMPRINT",FACE,{"disambiguationData":[TD([[makeQuery(id+"F67.imprint","IMPRINT",EDGE,{"derivedFrom":subQ0}),-1.0]])]});}
            extrude(context, id + "F68", {"entities" : qUnion([Q0, Q1]), "operationType" : NewBodyOperationType.REMOVE, "endBound" : BoundingType.THROUGH_ALL, "oppositeDirection" : true, "depth" : 25.4 * mm, "offsetDistance" : 25.4 * mm});
        }
        {
            var Q0;
            {var subQ7=sQuery(id+"F0.wireOp",EDGE,"E0.top");Q0=makeQuery(id+"F66.boolean.opBoolean","SPLIT",FACE,{"disambiguationData":[TD([makeQuery(id+"F66.opExtrude","SWEPT_FACE",FACE,{"disambiguationData":[OSD([sQuery(id+"F65.wireOp",EDGE,"E127.left")])]})])],"derivedFrom":makeQuery(id+"F5.boolean.opBoolean","MERGE",FACE,{"derivedFrom":[makeQuery(id+"F1.opExtrude","SWEPT_FACE",FACE,{"disambiguationData":[OSD([subQ7])]}),makeQuery(id+"F5.opExtrude","SWEPT_FACE",FACE,{"disambiguationData":[OSD([subQ7])]})]})});}
            var sketch = newSketch(context, id + "F69", { "sketchPlane" : qUnion([Q0])});
            skLineSegment(sketch, "E129.bottom", {"start": v(132.57, 11.1) * mm, "end": v(140.5, 11.1) * mm});
            skLineSegment(sketch, "E129.top", {"start": v(132.57, 0) * mm, "end": v(140.5, 0) * mm});
            skLineSegment(sketch, "E129.left", {"start": v(132.57, 11.1) * mm, "end": v(132.57, 0) * mm});
            skLineSegment(sketch, "E129.right", {"start": v(140.5, 11.1) * mm, "end": v(140.5, 0) * mm});
            skLineSegment(sketch, "E130.bottom", {"start": v(55.43, 11.1) * mm, "end": v(63.37, 11.1) * mm});
            skLineSegment(sketch, "E130.top", {"start": v(55.43, 0) * mm, "end": v(63.37, 0) * mm});
            skLineSegment(sketch, "E130.left", {"start": v(55.43, 11.1) * mm, "end": v(55.43, 0) * mm});
            skLineSegment(sketch, "E130.right", {"start": v(63.37, 11.1) * mm, "end": v(63.37, 0) * mm});
            skLineSegment(sketch, "E131.bottom", {"start": v(-91.79, 11.1) * mm, "end": v(-83.85, 11.1) * mm});
            skLineSegment(sketch, "E131.top", {"start": v(-91.79, 0) * mm, "end": v(-83.85, 0) * mm});
            skLineSegment(sketch, "E131.left", {"start": v(-91.79, 11.1) * mm, "end": v(-91.79, 0) * mm});
            skLineSegment(sketch, "E131.right", {"start": v(-83.85, 11.1) * mm, "end": v(-83.85, 0) * mm});
            skLineSegment(sketch, "E132.bottom", {"start": v(-114.17, 11.1) * mm, "end": v(-106.23, 11.1) * mm});
            skLineSegment(sketch, "E132.top", {"start": v(-114.17, 0) * mm, "end": v(-106.23, 0) * mm});
            skLineSegment(sketch, "E132.left", {"start": v(-114.17, 11.1) * mm, "end": v(-114.17, 0) * mm});
            skLineSegment(sketch, "E132.right", {"start": v(-106.23, 11.1) * mm, "end": v(-106.23, 0) * mm});
            skSolve(sketch);
        }
        {
            var Q0;
            Q0=makeQuery(id+"F69.imprint","IMPRINT",FACE,{"disambiguationData":[TD([[makeQuery(id+"F69.imprint","IMPRINT",EDGE,{"derivedFrom":sQuery(id+"F69.wireOp",EDGE,"E132.bottom")}),-1.0]])]});
            var Q1;
            Q1=makeQuery(id+"F69.imprint","IMPRINT",FACE,{"disambiguationData":[TD([[makeQuery(id+"F69.imprint","IMPRINT",EDGE,{"derivedFrom":sQuery(id+"F69.wireOp",EDGE,"E131.bottom")}),-1.0]])]});
            var Q2;
            Q2=makeQuery(id+"F69.imprint","IMPRINT",FACE,{"disambiguationData":[TD([[makeQuery(id+"F69.imprint","IMPRINT",EDGE,{"derivedFrom":sQuery(id+"F69.wireOp",EDGE,"E130.bottom")}),-1.0]])]});
            var Q3;
            Q3=makeQuery(id+"F69.imprint","IMPRINT",FACE,{"disambiguationData":[TD([[makeQuery(id+"F69.imprint","IMPRINT",EDGE,{"derivedFrom":sQuery(id+"F69.wireOp",EDGE,"E129.bottom")}),-1.0]])]});
            extrude(context, id + "F70", {"entities" : qUnion([Q0, Q1, Q2, Q3]), "operationType" : NewBodyOperationType.REMOVE, "oppositeDirection" : true, "depth" : 1.6 * mm, "offsetDistance" : 25.4 * mm});
        }
        {
            var Q0;
            Q0=makeQuery(id+"F70.boolean.opBoolean","COPY",EDGE,{"derivedFrom":makeQuery(id+"F70.opExtrude","CAP_EDGE",EDGE,{"disambiguationData":[OSD([sQuery(id+"F69.wireOp",EDGE,"E132.left")])],"isStart":false})});
            var Q1;
            Q1=makeQuery(id+"F70.boolean.opBoolean","COPY",EDGE,{"derivedFrom":makeQuery(id+"F70.opExtrude","CAP_EDGE",EDGE,{"disambiguationData":[OSD([sQuery(id+"F69.wireOp",EDGE,"E131.left")])],"isStart":false})});
            var Q2;
            Q2=makeQuery(id+"F70.boolean.opBoolean","COPY",EDGE,{"derivedFrom":makeQuery(id+"F70.opExtrude","CAP_EDGE",EDGE,{"disambiguationData":[OSD([sQuery(id+"F69.wireOp",EDGE,"E130.left")])],"isStart":false})});
            var Q3;
            Q3=makeQuery(id+"F70.boolean.opBoolean","COPY",EDGE,{"derivedFrom":makeQuery(id+"F70.opExtrude","CAP_EDGE",EDGE,{"disambiguationData":[OSD([sQuery(id+"F69.wireOp",EDGE,"E129.left")])],"isStart":false})});
            var Q4;
            Q4=makeQuery(id+"F70.boolean.opBoolean","COPY",EDGE,{"derivedFrom":makeQuery(id+"F70.opExtrude","CAP_EDGE",EDGE,{"disambiguationData":[OSD([sQuery(id+"F69.wireOp",EDGE,"E129.right")])],"isStart":false})});
            var Q5;
            Q5=makeQuery(id+"F70.boolean.opBoolean","COPY",EDGE,{"derivedFrom":makeQuery(id+"F70.opExtrude","CAP_EDGE",EDGE,{"disambiguationData":[OSD([sQuery(id+"F69.wireOp",EDGE,"E130.right")])],"isStart":false})});
            var Q6;
            Q6=makeQuery(id+"F70.boolean.opBoolean","COPY",EDGE,{"derivedFrom":makeQuery(id+"F70.opExtrude","CAP_EDGE",EDGE,{"disambiguationData":[OSD([sQuery(id+"F69.wireOp",EDGE,"E131.right")])],"isStart":false})});
            var Q7;
            Q7=makeQuery(id+"F70.boolean.opBoolean","COPY",EDGE,{"derivedFrom":makeQuery(id+"F70.opExtrude","CAP_EDGE",EDGE,{"disambiguationData":[OSD([sQuery(id+"F69.wireOp",EDGE,"E132.right")])],"isStart":false})});
            chamfer(context, id + "F71", {"entities" : qUnion([Q0, Q1, Q2, Q3, Q4, Q5, Q6, Q7]), "width" : 1.6 * mm, "tangentPropagation" : true});
        }
        {
            var Q0;
            {var subQ7=sQuery(id+"F0.wireOp",EDGE,"E0.top");Q0=makeQuery(id+"F66.boolean.opBoolean","SPLIT",FACE,{"disambiguationData":[TD([makeQuery(id+"F66.opExtrude","SWEPT_FACE",FACE,{"disambiguationData":[OSD([sQuery(id+"F65.wireOp",EDGE,"E127.left")])]})])],"derivedFrom":makeQuery(id+"F5.boolean.opBoolean","MERGE",FACE,{"derivedFrom":[makeQuery(id+"F1.opExtrude","SWEPT_FACE",FACE,{"disambiguationData":[OSD([subQ7])]}),makeQuery(id+"F5.opExtrude","SWEPT_FACE",FACE,{"disambiguationData":[OSD([subQ7])]})]})});}
            var sketch = newSketch(context, id + "F72", { "sketchPlane" : qUnion([Q0])});
            skCircle(sketch, "E133", {"center": v(148.63, 3.96) * mm, "radius": 3.3 * mm});
            skCircle(sketch, "E134", {"center": v(47.74, 3.96) * mm, "radius": 3.3 * mm});
            skCircle(sketch, "E135", {"center": v(-99.24, 3.96) * mm, "radius": 3.3 * mm});
            skSolve(sketch);
        }
        {
            var Q0;
            Q0=makeQuery(id+"F72.imprint","IMPRINT",FACE,{"disambiguationData":[TD([[makeQuery(id+"F72.imprint","IMPRINT",EDGE,{"derivedFrom":sQuery(id+"F72.wireOp",EDGE,"E135")}),1.0]])]});
            var Q1;
            Q1=makeQuery(id+"F72.imprint","IMPRINT",FACE,{"disambiguationData":[TD([[makeQuery(id+"F72.imprint","IMPRINT",EDGE,{"derivedFrom":sQuery(id+"F72.wireOp",EDGE,"E134")}),1.0]])]});
            var Q2;
            Q2=makeQuery(id+"F72.imprint","IMPRINT",FACE,{"disambiguationData":[TD([[makeQuery(id+"F72.imprint","IMPRINT",EDGE,{"derivedFrom":sQuery(id+"F72.wireOp",EDGE,"E133")}),1.0]])]});
            extrude(context, id + "F73", {"entities" : qUnion([Q0, Q1, Q2]), "operationType" : NewBodyOperationType.REMOVE, "oppositeDirection" : true, "depth" : 2.03 * mm, "offsetDistance" : 25.4 * mm});
        }
        {
            var Q0;
            Q0=qCreatedBy(makeId("Top.planeOp"),FACE);
            var sketch = newSketch(context, id + "F74", { "sketchPlane" : qUnion([Q0])});
            skLineSegment(sketch, "E136.bottom", {"start": v(166.69, -66.76) * mm, "end": v(-166.69, -66.76) * mm});
            skLineSegment(sketch, "E136.top", {"start": v(166.69, -193.76) * mm, "end": v(-166.69, -193.76) * mm});
            skLineSegment(sketch, "E136.left", {"start": v(166.69, -66.76) * mm, "end": v(166.69, -193.76) * mm});
            skLineSegment(sketch, "E136.right", {"start": v(-166.69, -66.76) * mm, "end": v(-166.69, -193.76) * mm});
            skPoint(sketch, "E136.middle", {"position": v(0, -130.26) * mm});
            skLineSegment(sketch, "E137.bottom", {"start": v(-106.36, -66.76) * mm, "end": v(-90.49, -66.76) * mm});
            skLineSegment(sketch, "E137.top", {"start": v(-106.36, -57.23) * mm, "end": v(-90.49, -57.23) * mm});
            skLineSegment(sketch, "E137.left", {"start": v(-106.36, -66.76) * mm, "end": v(-106.36, -57.23) * mm});
            skLineSegment(sketch, "E137.right", {"start": v(-90.49, -66.76) * mm, "end": v(-90.49, -57.23) * mm});
            skLineSegment(sketch, "E138.bottom", {"start": v(90.49, -66.76) * mm, "end": v(106.36, -66.76) * mm});
            skLineSegment(sketch, "E138.top", {"start": v(90.49, -57.23) * mm, "end": v(106.36, -57.23) * mm});
            skLineSegment(sketch, "E138.left", {"start": v(90.49, -66.76) * mm, "end": v(90.49, -57.23) * mm});
            skLineSegment(sketch, "E138.right", {"start": v(106.36, -66.76) * mm, "end": v(106.36, -57.23) * mm});
            skSolve(sketch);
        }
        {
            var Q0;
            Q0=makeQuery(id+"F74.imprint","IMPRINT",FACE,{"disambiguationData":[TD([[makeQuery(id+"F74.imprint","IMPRINT",EDGE,{"derivedFrom":sQuery(id+"F74.wireOp",EDGE,"E137.top")}),-1.0]])]});
            var Q1;
            Q1=makeQuery(id+"F74.imprint","IMPRINT",FACE,{"disambiguationData":[TD([[makeQuery(id+"F74.imprint","IMPRINT",EDGE,{"derivedFrom":sQuery(id+"F74.wireOp",EDGE,"E138.top")}),-1.0]])]});
            var Q2;
            Q2=makeQuery(id+"F74.imprint","IMPRINT",FACE,{"disambiguationData":[TD([[makeQuery(id+"F74.imprint","IMPRINT",EDGE,{"derivedFrom":sQuery(id+"F74.wireOp",EDGE,"E136.top")}),-1.0]])]});
            extrude(context, id + "F75", {"entities" : qUnion([Q0, Q1, Q2]), "depth" : 2.38 * mm, "offsetDistance" : 25.4 * mm});
        }
        {
            var Q0;
            Q0=makeQuery(id+"F75.opExtrude","CAP_FACE",FACE,{"disambiguationData":[OSD([sQuery(id+"F74.wireOp",EDGE,"E136.bottom"),sQuery(id+"F74.wireOp",EDGE,"E136.top"),sQuery(id+"F74.wireOp",EDGE,"E136.left"),sQuery(id+"F74.wireOp",EDGE,"E136.right"),sQuery(id+"F74.wireOp",EDGE,"E137.top"),sQuery(id+"F74.wireOp",EDGE,"E137.left"),sQuery(id+"F74.wireOp",EDGE,"E137.right"),sQuery(id+"F74.wireOp",EDGE,"E138.top"),sQuery(id+"F74.wireOp",EDGE,"E138.left"),sQuery(id+"F74.wireOp",EDGE,"E138.right")])],"isStart":false});
            var sketch = newSketch(context, id + "F76", { "sketchPlane" : qUnion([Q0])});
            skPoint(sketch, "E139.oppositeSnap0", {"position": v(-90.49, -62) * mm});
            skLineSegment(sketch, "E139.bottom", {"start": v(-106.36, -57.23) * mm, "end": v(-90.49, -57.23) * mm});
            skLineSegment(sketch, "E139.top", {"start": v(-106.36, -73.1) * mm, "end": v(-90.49, -73.1) * mm});
            skLineSegment(sketch, "E139.left", {"start": v(-106.36, -57.23) * mm, "end": v(-106.36, -73.1) * mm});
            skLineSegment(sketch, "E139.right", {"start": v(-90.49, -57.23) * mm, "end": v(-90.49, -73.1) * mm});
            skLineSegment(sketch, "E140.bottom", {"start": v(106.36, -57.23) * mm, "end": v(90.49, -57.23) * mm});
            skLineSegment(sketch, "E140.top", {"start": v(106.36, -73.1) * mm, "end": v(90.49, -73.1) * mm});
            skLineSegment(sketch, "E140.left", {"start": v(106.36, -57.23) * mm, "end": v(106.36, -73.1) * mm});
            skLineSegment(sketch, "E140.right", {"start": v(90.49, -57.23) * mm, "end": v(90.49, -73.1) * mm});
            skLineSegment(sketch, "E141", {"start": v(92.07, -73.1) * mm, "end": v(92.07, -62) * mm});
            skLineSegment(sketch, "E142", {"start": v(92.07, -62) * mm, "end": v(93.66, -62) * mm});
            skLineSegment(sketch, "E143", {"start": v(93.66, -62) * mm, "end": v(93.66, -70.72) * mm});
            skLineSegment(sketch, "E144", {"start": v(93.66, -70.72) * mm, "end": v(103.19, -70.72) * mm});
            skLineSegment(sketch, "E145", {"start": v(103.19, -70.72) * mm, "end": v(103.19, -62) * mm});
            skLineSegment(sketch, "E146", {"start": v(103.19, -62) * mm, "end": v(104.77, -62) * mm});
            skLineSegment(sketch, "E147", {"start": v(104.77, -62) * mm, "end": v(104.77, -73.1) * mm});
            skLineSegment(sketch, "E148", {"start": v(-104.76, -73.1) * mm, "end": v(-104.76, -62) * mm});
            skLineSegment(sketch, "E149", {"start": v(-104.76, -62) * mm, "end": v(-103.16, -62) * mm});
            skLineSegment(sketch, "E150", {"start": v(-103.16, -62) * mm, "end": v(-103.16, -70.72) * mm});
            skLineSegment(sketch, "E151", {"start": v(-103.16, -70.72) * mm, "end": v(-93.69, -70.72) * mm});
            skLineSegment(sketch, "E152", {"start": v(-93.69, -70.72) * mm, "end": v(-93.69, -62) * mm});
            skLineSegment(sketch, "E153", {"start": v(-93.69, -62) * mm, "end": v(-92.09, -62) * mm});
            skLineSegment(sketch, "E154", {"start": v(-92.09, -62) * mm, "end": v(-92.09, -73.1) * mm});
            skSolve(sketch);
        }
        {
            var Q0;
            {var subQ9=sQuery(id+"F76.wireOp",EDGE,"E139.bottom");Q0=makeQuery(id+"F76.imprint","IMPRINT",FACE,{"disambiguationData":[TD([[makeQuery(id+"F76.imprint","IMPRINT",EDGE,{"derivedFrom":subQ9}),-1.0]])]});}
            var Q1;
            {var subQ7=sQuery(id+"F76.wireOp",EDGE,"E140.bottom");Q1=makeQuery(id+"F76.imprint","IMPRINT",FACE,{"disambiguationData":[TD([[makeQuery(id+"F76.imprint","IMPRINT",EDGE,{"derivedFrom":subQ7}),-1.0]])]});}
            extrude(context, id + "F77", {"entities" : qUnion([Q0, Q1]), "operationType" : NewBodyOperationType.ADD, "depth" : 1.59 * mm, "offsetDistance" : 25.4 * mm});
        }
        {
            var Q0;
            Q0=makeQuery(id+"F77.opExtrude","CAP_EDGE",EDGE,{"disambiguationData":[OSD([sQuery(id+"F76.wireOp",EDGE,"E151")])],"isStart":false});
            var Q1;
            Q1=makeQuery(id+"F77.opExtrude","CAP_EDGE",EDGE,{"disambiguationData":[OSD([sQuery(id+"F76.wireOp",EDGE,"E144")])],"isStart":false});
            var Q2;
            Q2=makeQuery(id+"F77.opExtrude","CAP_EDGE",EDGE,{"disambiguationData":[OSD([sQuery(id+"F76.wireOp",EDGE,"E142")])],"isStart":true});
            var Q3;
            Q3=makeQuery(id+"F77.opExtrude","CAP_EDGE",EDGE,{"disambiguationData":[OSD([sQuery(id+"F76.wireOp",EDGE,"E146")])],"isStart":true});
            var Q4;
            Q4=makeQuery(id+"F77.opExtrude","CAP_EDGE",EDGE,{"disambiguationData":[OSD([sQuery(id+"F76.wireOp",EDGE,"E153")])],"isStart":true});
            var Q5;
            Q5=makeQuery(id+"F77.opExtrude","CAP_EDGE",EDGE,{"disambiguationData":[OSD([sQuery(id+"F76.wireOp",EDGE,"E149")])],"isStart":true});
            chamfer(context, id + "F78", {"entities" : qUnion([Q0, Q1, Q2, Q3, Q4, Q5]), "width" : 1.65 * mm, "tangentPropagation" : true});
        }
        {
            var Q0;
            Q0=makeQuery(id+"F77.boolean.opBoolean","MERGE",EDGE,{"derivedFrom":[makeQuery(id+"F75.opExtrude","SWEPT_EDGE",EDGE,{"disambiguationData":[OSD([sQuery(id+"F74.wireOp",EDGE,"E137.top"),sQuery(id+"F74.wireOp",EDGE,"E137.left")])]}),makeQuery(id+"F77.opExtrude","SWEPT_EDGE",EDGE,{"disambiguationData":[OSD([sQuery(id+"F76.wireOp",EDGE,"E139.bottom"),sQuery(id+"F76.wireOp",EDGE,"E139.left")])]})]});
            var Q1;
            Q1=makeQuery(id+"F77.boolean.opBoolean","MERGE",EDGE,{"derivedFrom":[makeQuery(id+"F75.opExtrude","SWEPT_EDGE",EDGE,{"disambiguationData":[OSD([sQuery(id+"F74.wireOp",EDGE,"E137.top"),sQuery(id+"F74.wireOp",EDGE,"E137.right")])]}),makeQuery(id+"F77.opExtrude","SWEPT_EDGE",EDGE,{"disambiguationData":[OSD([sQuery(id+"F76.wireOp",EDGE,"E139.bottom"),sQuery(id+"F76.wireOp",EDGE,"E139.right")])]})]});
            var Q2;
            Q2=makeQuery(id+"F77.boolean.opBoolean","MERGE",EDGE,{"derivedFrom":[makeQuery(id+"F75.opExtrude","SWEPT_EDGE",EDGE,{"disambiguationData":[OSD([sQuery(id+"F74.wireOp",EDGE,"E138.top"),sQuery(id+"F74.wireOp",EDGE,"E138.right")])]}),makeQuery(id+"F77.opExtrude","SWEPT_EDGE",EDGE,{"disambiguationData":[OSD([sQuery(id+"F76.wireOp",EDGE,"E140.bottom"),sQuery(id+"F76.wireOp",EDGE,"E140.left")])]})]});
            var Q3;
            Q3=makeQuery(id+"F77.boolean.opBoolean","MERGE",EDGE,{"derivedFrom":[makeQuery(id+"F75.opExtrude","SWEPT_EDGE",EDGE,{"disambiguationData":[OSD([sQuery(id+"F74.wireOp",EDGE,"E138.top"),sQuery(id+"F74.wireOp",EDGE,"E138.left")])]}),makeQuery(id+"F77.opExtrude","SWEPT_EDGE",EDGE,{"disambiguationData":[OSD([sQuery(id+"F76.wireOp",EDGE,"E140.bottom"),sQuery(id+"F76.wireOp",EDGE,"E140.right")])]})]});
            chamfer(context, id + "F79", {"entities" : qUnion([Q0, Q1, Q2, Q3]), "width" : 1.9 * mm, "tangentPropagation" : true});
        }
        {
            var Q0;
            Q0=makeQuery(id+"F77.opExtrude","CAP_FACE",FACE,{"disambiguationData":[OSD([sQuery(id+"F76.wireOp",EDGE,"E139.bottom"),sQuery(id+"F76.wireOp",EDGE,"E139.top"),sQuery(id+"F76.wireOp",EDGE,"E139.left"),sQuery(id+"F76.wireOp",EDGE,"E139.right"),sQuery(id+"F76.wireOp",EDGE,"E148"),sQuery(id+"F76.wireOp",EDGE,"E149"),sQuery(id+"F76.wireOp",EDGE,"E150"),sQuery(id+"F76.wireOp",EDGE,"E151"),sQuery(id+"F76.wireOp",EDGE,"E152"),sQuery(id+"F76.wireOp",EDGE,"E153"),sQuery(id+"F76.wireOp",EDGE,"E154")])],"isStart":false});
            var sketch = newSketch(context, id + "F80", { "sketchPlane" : qUnion([Q0])});
            skCircle(sketch, "E155", {"center": v(-98.43, -62.8) * mm, "radius": 2.39 * mm});
            skSolve(sketch);
        }
        {
            var Q0;
            Q0=makeQuery(id+"F80.imprint","IMPRINT",FACE,{"disambiguationData":[TD([[makeQuery(id+"F80.imprint","IMPRINT",EDGE,{"derivedFrom":sQuery(id+"F80.wireOp",EDGE,"E155")}),1.0]])]});
            extrude(context, id + "F81", {"entities" : qUnion([Q0]), "operationType" : NewBodyOperationType.REMOVE, "endBound" : BoundingType.THROUGH_ALL, "oppositeDirection" : true, "depth" : 25.4 * mm, "offsetDistance" : 25.4 * mm});
        }
        {
            var Q0;
            Q0=makeQuery(id+"F77.opExtrude","CAP_FACE",FACE,{"disambiguationData":[OSD([sQuery(id+"F76.wireOp",EDGE,"E140.bottom"),sQuery(id+"F76.wireOp",EDGE,"E140.top"),sQuery(id+"F76.wireOp",EDGE,"E140.left"),sQuery(id+"F76.wireOp",EDGE,"E140.right"),sQuery(id+"F76.wireOp",EDGE,"E141"),sQuery(id+"F76.wireOp",EDGE,"E142"),sQuery(id+"F76.wireOp",EDGE,"E143"),sQuery(id+"F76.wireOp",EDGE,"E144"),sQuery(id+"F76.wireOp",EDGE,"E145"),sQuery(id+"F76.wireOp",EDGE,"E146"),sQuery(id+"F76.wireOp",EDGE,"E147")])],"isStart":false});
            var sketch = newSketch(context, id + "F82", { "sketchPlane" : qUnion([Q0])});
            skCircle(sketch, "E156", {"center": v(98.42, -62.8) * mm, "radius": 2.39 * mm});
            skPoint(sketch, "E156.centerSnap0", {"position": v(98.42, -57.23) * mm});
            skSolve(sketch);
        }
        {
            var Q0;
            Q0=makeQuery(id+"F82.imprint","IMPRINT",FACE,{"disambiguationData":[TD([[makeQuery(id+"F82.imprint","IMPRINT",EDGE,{"derivedFrom":sQuery(id+"F82.wireOp",EDGE,"E156")}),1.0]])]});
            extrude(context, id + "F83", {"entities" : qUnion([Q0]), "operationType" : NewBodyOperationType.REMOVE, "endBound" : BoundingType.THROUGH_ALL, "oppositeDirection" : true, "depth" : 25.4 * mm, "offsetDistance" : 25.4 * mm});
        }
        {
            var Q0;
            Q0=makeQuery(id+"F75.opExtrude","SWEPT_EDGE",EDGE,{"disambiguationData":[OSD([sQuery(id+"F74.wireOp",EDGE,"E136.top"),sQuery(id+"F74.wireOp",EDGE,"E136.right")])]});
            var Q1;
            Q1=makeQuery(id+"F75.opExtrude","SWEPT_EDGE",EDGE,{"disambiguationData":[OSD([sQuery(id+"F74.wireOp",EDGE,"E136.top"),sQuery(id+"F74.wireOp",EDGE,"E136.left")])]});
            fillet(context, id + "F84", {"entities" : qUnion([Q0, Q1]), "radius" : 15.88 * mm, "tangentPropagation" : true, "allowEdgeOverflow" : false});
        }
        {
            var Q0;
            Q0=makeQuery(id+"F75.opExtrude","SWEPT_EDGE",EDGE,{"disambiguationData":[OSD([sQuery(id+"F74.wireOp",EDGE,"E136.bottom"),sQuery(id+"F74.wireOp",EDGE,"E136.right")])]});
            var Q1;
            Q1=makeQuery(id+"F75.opExtrude","SWEPT_EDGE",EDGE,{"disambiguationData":[OSD([sQuery(id+"F74.wireOp",EDGE,"E136.bottom"),sQuery(id+"F74.wireOp",EDGE,"E136.left")])]});
            fillet(context, id + "F85", {"entities" : qUnion([Q0, Q1]), "radius" : 9.52 * mm, "tangentPropagation" : true, "allowEdgeOverflow" : false});
        }
        {
            var Q0;
            Q0=qCreatedBy(makeId("Right.planeOp"),FACE);
            var sketch = newSketch(context, id + "F86", { "sketchPlane" : qUnion([Q0])});
            skLineSegment(sketch, "E157", {"start": v(128.21, 0) * mm, "end": v(242.51, 0) * mm});
            skLineSegment(sketch, "E158", {"start": v(242.51, 0) * mm, "end": v(218.47, 39.26) * mm});
            skLineSegment(sketch, "E159", {"start": v(218.47, 39.26) * mm, "end": v(242.51, 0) * mm, "construction": true});
            skLineSegment(sketch, "E160", {"start": v(218.47, 39.26) * mm, "end": v(128.21, 0) * mm});
            skSolve(sketch);
        }
        {
            var Q0;
            Q0=makeQuery(id+"F86.imprint","IMPRINT",FACE,{"disambiguationData":[TD([[makeQuery(id+"F86.imprint","IMPRINT",EDGE,{"derivedFrom":sQuery(id+"F86.wireOp",EDGE,"E157")}),1.0]])]});
            extrude(context, id + "F87", {"entities" : qUnion([Q0]), "oppositeDirection" : true, "depth" : 323.85 * mm, "offsetDistance" : 25.4 * mm});
        }
        {
            var Q0;
            Q0=makeQuery(id+"F87.opExtrude","CAP_EDGE",EDGE,{"disambiguationData":[OSD([sQuery(id+"F86.wireOp",EDGE,"E158")])],"isStart":true});
            var Q1;
            Q1=makeQuery(id+"F87.opExtrude","CAP_EDGE",EDGE,{"disambiguationData":[OSD([sQuery(id+"F86.wireOp",EDGE,"E158")])],"isStart":false});
            fillet(context, id + "F88", {"entities" : qUnion([Q0, Q1]), "radius" : 9.52 * mm, "tangentPropagation" : true, "allowEdgeOverflow" : false});
        }
        {
            var Q0;
            Q0=makeQuery(id+"F87.opExtrude","SWEPT_FACE",FACE,{"disambiguationData":[OSD([sQuery(id+"F86.wireOp",EDGE,"E158")])]});
            var sketch = newSketch(context, id + "F89", { "sketchPlane" : qUnion([Q0])});
            skLineSegment(sketch, "E161", {"start": v(55.56, -80.62) * mm, "end": v(50.8, -117.13) * mm});
            skLineSegment(sketch, "E162", {"start": v(50.8, -117.13) * mm, "end": v(101.6, -117.13) * mm});
            skLineSegment(sketch, "E163", {"start": v(101.6, -117.13) * mm, "end": v(96.84, -80.62) * mm});
            skLineSegment(sketch, "E164", {"start": v(96.84, -80.62) * mm, "end": v(55.56, -80.62) * mm});
            skLineSegment(sketch, "E165", {"start": v(76.2, -117.13) * mm, "end": v(76.2, -80.62) * mm, "construction": true});
            skLineSegment(sketch, "E166", {"start": v(50.8, -117.13) * mm, "end": v(50.8, -84.8) * mm, "construction": true});
            skLineSegment(sketch, "E167", {"start": v(101.6, -117.13) * mm, "end": v(101.6, -56.53) * mm, "construction": true});
            skLineSegment(sketch, "E168", {"start": v(198.45, -80.62) * mm, "end": v(193.67, -117.13) * mm});
            skLineSegment(sketch, "E169", {"start": v(193.67, -117.13) * mm, "end": v(244.47, -117.13) * mm});
            skLineSegment(sketch, "E170", {"start": v(244.48, -117.13) * mm, "end": v(239.7, -80.62) * mm});
            skLineSegment(sketch, "E171", {"start": v(239.7, -80.62) * mm, "end": v(198.45, -80.62) * mm});
            skLineSegment(sketch, "E172", {"start": v(193.67, -117.13) * mm, "end": v(193.67, -89.33) * mm, "construction": true});
            skLineSegment(sketch, "E173", {"start": v(244.48, -117.13) * mm, "end": v(244.48, -53.54) * mm, "construction": true});
            skLineSegment(sketch, "E174", {"start": v(311.15, -80.62) * mm, "end": v(311.15, -117.13) * mm});
            skLineSegment(sketch, "E175", {"start": v(311.15, -117.13) * mm, "end": v(273.05, -117.13) * mm});
            skLineSegment(sketch, "E176", {"start": v(273.05, -117.13) * mm, "end": v(277.83, -80.62) * mm});
            skLineSegment(sketch, "E177", {"start": v(277.83, -80.62) * mm, "end": v(311.15, -80.62) * mm});
            skLineSegment(sketch, "E178", {"start": v(273.05, -117.13) * mm, "end": v(273.05, -50.37) * mm, "construction": true});
            skSolve(sketch);
        }
        {
            var Q0;
            Q0=makeQuery(id+"F89.imprint","IMPRINT",FACE,{"disambiguationData":[TD([[makeQuery(id+"F89.imprint","IMPRINT",EDGE,{"derivedFrom":sQuery(id+"F89.wireOp",EDGE,"E161")}),1.0]])]});
            var Q1;
            Q1=makeQuery(id+"F89.imprint","IMPRINT",FACE,{"disambiguationData":[TD([[makeQuery(id+"F89.imprint","IMPRINT",EDGE,{"derivedFrom":sQuery(id+"F89.wireOp",EDGE,"E168")}),1.0]])]});
            var Q2;
            Q2=makeQuery(id+"F89.imprint","IMPRINT",FACE,{"disambiguationData":[TD([[makeQuery(id+"F89.imprint","IMPRINT",EDGE,{"derivedFrom":sQuery(id+"F89.wireOp",EDGE,"E174")}),-1.0]])]});
            extrude(context, id + "F90", {"entities" : qUnion([Q0, Q1, Q2]), "operationType" : NewBodyOperationType.REMOVE, "oppositeDirection" : true, "depth" : 5.5 * mm, "offsetDistance" : 25.4 * mm});
        }
        {
            var Q0;
            Q0=makeQuery(id+"F90.boolean.opBoolean","COPY",EDGE,{"derivedFrom":makeQuery(id+"F90.opExtrude","CAP_EDGE",EDGE,{"disambiguationData":[OSD([sQuery(id+"F89.wireOp",EDGE,"E161")])],"isStart":false})});
            var Q1;
            Q1=makeQuery(id+"F90.boolean.opBoolean","COPY",EDGE,{"derivedFrom":makeQuery(id+"F90.opExtrude","CAP_EDGE",EDGE,{"disambiguationData":[OSD([sQuery(id+"F89.wireOp",EDGE,"E163")])],"isStart":false})});
            var Q2;
            Q2=makeQuery(id+"F90.boolean.opBoolean","COPY",EDGE,{"derivedFrom":makeQuery(id+"F90.opExtrude","CAP_EDGE",EDGE,{"disambiguationData":[OSD([sQuery(id+"F89.wireOp",EDGE,"E170")])],"isStart":false})});
            var Q3;
            Q3=makeQuery(id+"F90.boolean.opBoolean","COPY",EDGE,{"derivedFrom":makeQuery(id+"F90.opExtrude","CAP_EDGE",EDGE,{"disambiguationData":[OSD([sQuery(id+"F89.wireOp",EDGE,"E168")])],"isStart":false})});
            var Q4;
            Q4=makeQuery(id+"F90.boolean.opBoolean","COPY",EDGE,{"derivedFrom":makeQuery(id+"F90.opExtrude","CAP_EDGE",EDGE,{"disambiguationData":[OSD([sQuery(id+"F89.wireOp",EDGE,"E176")])],"isStart":false})});
            fillet(context, id + "F91", {"entities" : qUnion([Q0, Q1, Q2, Q3, Q4]), "radius" : 22.86 * mm, "tangentPropagation" : true, "allowEdgeOverflow" : false});
        }
        {
            var Q0;
            Q0=makeQuery(id+"F90.boolean.opBoolean","COPY",EDGE,{"derivedFrom":makeQuery(id+"F90.opExtrude","CAP_EDGE",EDGE,{"disambiguationData":[OSD([sQuery(id+"F89.wireOp",EDGE,"E174")])],"isStart":false})});
            fillet(context, id + "F92", {"entities" : qUnion([Q0]), "radius" : 5.08 * mm, "tangentPropagation" : true, "allowEdgeOverflow" : false});
        }
        {
            var Q0;
            Q0=makeQuery(id+"F90.boolean.opBoolean","COPY",EDGE,{"derivedFrom":makeQuery(id+"F90.opExtrude","CAP_EDGE",EDGE,{"disambiguationData":[OSD([sQuery(id+"F89.wireOp",EDGE,"E169")])],"isStart":false})});
            var Q1;
            Q1=makeQuery(id+"F90.boolean.opBoolean","COPY",EDGE,{"derivedFrom":makeQuery(id+"F90.opExtrude","CAP_EDGE",EDGE,{"disambiguationData":[OSD([sQuery(id+"F89.wireOp",EDGE,"E175")])],"isStart":false})});
            var Q2;
            Q2=makeQuery(id+"F90.boolean.opBoolean","COPY",EDGE,{"derivedFrom":makeQuery(id+"F90.opExtrude","CAP_EDGE",EDGE,{"disambiguationData":[OSD([sQuery(id+"F89.wireOp",EDGE,"E162")])],"isStart":false})});
            fillet(context, id + "F93", {"entities" : qUnion([Q0, Q1, Q2]), "radius" : 5.08 * mm, "tangentPropagation" : true, "allowEdgeOverflow" : false});
        }
        {
            var Q0;
            Q0=makeQuery(id+"F90.boolean.opBoolean","COPY",FACE,{"derivedFrom":makeQuery(id+"F90.opExtrude","SWEPT_FACE",FACE,{"disambiguationData":[OSD([sQuery(id+"F89.wireOp",EDGE,"E164")])]})});
            var Q1;
            Q1=makeQuery(id+"F90.boolean.opBoolean","COPY",FACE,{"derivedFrom":makeQuery(id+"F90.opExtrude","SWEPT_FACE",FACE,{"disambiguationData":[OSD([sQuery(id+"F89.wireOp",EDGE,"E171")])]})});
            var Q2;
            Q2=makeQuery(id+"F90.boolean.opBoolean","COPY",FACE,{"derivedFrom":makeQuery(id+"F90.opExtrude","SWEPT_FACE",FACE,{"disambiguationData":[OSD([sQuery(id+"F89.wireOp",EDGE,"E177")])]})});
            extrude(context, id + "F94", {"entities" : qUnion([Q0, Q1, Q2]), "operationType" : NewBodyOperationType.REMOVE, "endBound" : BoundingType.THROUGH_ALL, "oppositeDirection" : true, "depth" : 25.4 * mm, "offsetDistance" : 25.4 * mm});
        }
        {
            var Q0;
            Q0=makeQuery(id+"F87.opExtrude","SWEPT_FACE",FACE,{"disambiguationData":[OSD([sQuery(id+"F86.wireOp",EDGE,"E158")])]});
            var sketch = newSketch(context, id + "F95", { "sketchPlane" : qUnion([Q0])});
            skLineSegment(sketch, "E179.bottom", {"start": v(46.8, -126.66) * mm, "end": v(44.42, -126.66) * mm});
            skLineSegment(sketch, "E179.top", {"start": v(46.8, -104.43) * mm, "end": v(44.42, -104.43) * mm});
            skLineSegment(sketch, "E179.left", {"start": v(46.8, -126.66) * mm, "end": v(46.8, -104.43) * mm});
            skLineSegment(sketch, "E179.right", {"start": v(44.42, -126.66) * mm, "end": v(44.42, -104.43) * mm});
            skLineSegment(sketch, "E180.bottom", {"start": v(106.05, -126.66) * mm, "end": v(108.44, -126.66) * mm});
            skLineSegment(sketch, "E180.top", {"start": v(106.05, -104.43) * mm, "end": v(108.44, -104.43) * mm});
            skLineSegment(sketch, "E180.left", {"start": v(106.05, -126.66) * mm, "end": v(106.05, -104.43) * mm});
            skLineSegment(sketch, "E180.right", {"start": v(108.44, -126.66) * mm, "end": v(108.44, -104.43) * mm});
            skLineSegment(sketch, "E181.bottom", {"start": v(190.06, -126.66) * mm, "end": v(187.68, -126.66) * mm});
            skLineSegment(sketch, "E181.top", {"start": v(190.06, -104.43) * mm, "end": v(187.68, -104.43) * mm});
            skLineSegment(sketch, "E181.left", {"start": v(190.06, -126.66) * mm, "end": v(190.06, -104.43) * mm});
            skLineSegment(sketch, "E181.right", {"start": v(187.68, -126.66) * mm, "end": v(187.68, -104.43) * mm});
            skLineSegment(sketch, "E182.bottom", {"start": v(247.48, -126.66) * mm, "end": v(249.87, -126.66) * mm});
            skLineSegment(sketch, "E182.top", {"start": v(247.48, -104.43) * mm, "end": v(249.87, -104.43) * mm});
            skLineSegment(sketch, "E182.left", {"start": v(247.48, -126.66) * mm, "end": v(247.48, -104.43) * mm});
            skLineSegment(sketch, "E182.right", {"start": v(249.87, -126.66) * mm, "end": v(249.87, -104.43) * mm});
            skLineSegment(sketch, "E183.bottom", {"start": v(270.26, -126.66) * mm, "end": v(267.87, -126.66) * mm});
            skLineSegment(sketch, "E183.top", {"start": v(270.26, -104.43) * mm, "end": v(267.87, -104.43) * mm});
            skLineSegment(sketch, "E183.left", {"start": v(270.26, -126.66) * mm, "end": v(270.26, -104.43) * mm});
            skLineSegment(sketch, "E183.right", {"start": v(267.87, -126.66) * mm, "end": v(267.87, -104.43) * mm});
            skLineSegment(sketch, "E184.bottom", {"start": v(314.33, -126.66) * mm, "end": v(311.94, -126.66) * mm});
            skLineSegment(sketch, "E184.top", {"start": v(314.33, -104.43) * mm, "end": v(311.94, -104.43) * mm});
            skLineSegment(sketch, "E184.left", {"start": v(314.33, -126.66) * mm, "end": v(314.33, -104.43) * mm});
            skLineSegment(sketch, "E184.right", {"start": v(311.94, -126.66) * mm, "end": v(311.94, -104.43) * mm});
            skSolve(sketch);
        }
        {
            var Q0;
            Q0=makeQuery(id+"F95.imprint","IMPRINT",FACE,{"disambiguationData":[TD([[makeQuery(id+"F95.imprint","IMPRINT",EDGE,{"derivedFrom":sQuery(id+"F95.wireOp",EDGE,"E179.bottom")}),-1.0]])]});
            var Q1;
            Q1=makeQuery(id+"F95.imprint","IMPRINT",FACE,{"disambiguationData":[TD([[makeQuery(id+"F95.imprint","IMPRINT",EDGE,{"derivedFrom":sQuery(id+"F95.wireOp",EDGE,"E180.bottom")}),-1.0]])]});
            var Q2;
            Q2=makeQuery(id+"F95.imprint","IMPRINT",FACE,{"disambiguationData":[TD([[makeQuery(id+"F95.imprint","IMPRINT",EDGE,{"derivedFrom":sQuery(id+"F95.wireOp",EDGE,"E181.bottom")}),-1.0]])]});
            var Q3;
            Q3=makeQuery(id+"F95.imprint","IMPRINT",FACE,{"disambiguationData":[TD([[makeQuery(id+"F95.imprint","IMPRINT",EDGE,{"derivedFrom":sQuery(id+"F95.wireOp",EDGE,"E182.bottom")}),-1.0]])]});
            var Q4;
            Q4=makeQuery(id+"F95.imprint","IMPRINT",FACE,{"disambiguationData":[TD([[makeQuery(id+"F95.imprint","IMPRINT",EDGE,{"derivedFrom":sQuery(id+"F95.wireOp",EDGE,"E183.bottom")}),-1.0]])]});
            var Q5;
            Q5=makeQuery(id+"F95.imprint","IMPRINT",FACE,{"disambiguationData":[TD([[makeQuery(id+"F95.imprint","IMPRINT",EDGE,{"derivedFrom":sQuery(id+"F95.wireOp",EDGE,"E184.bottom")}),-1.0]])]});
            extrude(context, id + "F96", {"entities" : qUnion([Q0, Q1, Q2, Q3, Q4, Q5]), "operationType" : NewBodyOperationType.ADD, "depth" : 1.59 * mm, "offsetDistance" : 25.4 * mm});
        }
        {
            var Q0;
            Q0=makeQuery(id+"F87.opExtrude","SWEPT_FACE",FACE,{"disambiguationData":[OSD([sQuery(id+"F86.wireOp",EDGE,"E158")])]});
            var sketch = newSketch(context, id + "F97", { "sketchPlane" : qUnion([Q0])});
            skLineSegment(sketch, "E185.bottom", {"start": v(108.44, -126.66) * mm, "end": v(187.68, -126.66) * mm});
            skLineSegment(sketch, "E185.top", {"start": v(108.44, -80.62) * mm, "end": v(187.68, -80.62) * mm});
            skLineSegment(sketch, "E185.left", {"start": v(108.44, -126.66) * mm, "end": v(108.44, -80.62) * mm});
            skLineSegment(sketch, "E185.right", {"start": v(187.68, -126.66) * mm, "end": v(187.68, -80.62) * mm});
            skLineSegment(sketch, "E186.bottom", {"start": v(249.87, -126.66) * mm, "end": v(267.87, -126.66) * mm});
            skLineSegment(sketch, "E186.top", {"start": v(249.87, -80.62) * mm, "end": v(267.87, -80.62) * mm});
            skLineSegment(sketch, "E186.left", {"start": v(249.87, -126.66) * mm, "end": v(249.87, -80.62) * mm});
            skLineSegment(sketch, "E186.right", {"start": v(267.87, -126.66) * mm, "end": v(267.87, -80.62) * mm});
            skLineSegment(sketch, "E187.bottom", {"start": v(44.42, -126.66) * mm, "end": v(9.53, -126.66) * mm});
            skLineSegment(sketch, "E187.top", {"start": v(44.42, -80.62) * mm, "end": v(9.53, -80.62) * mm});
            skLineSegment(sketch, "E187.left", {"start": v(44.42, -126.66) * mm, "end": v(44.42, -80.62) * mm});
            skLineSegment(sketch, "E187.right", {"start": v(9.53, -126.66) * mm, "end": v(9.53, -80.62) * mm});
            skSolve(sketch);
        }
        {
            var Q0;
            {var subQ5=sQuery(id+"F97.wireOp",EDGE,"E187.bottom");Q0=makeQuery(id+"F97.imprint","IMPRINT",FACE,{"disambiguationData":[TD([[makeQuery(id+"F97.imprint","IMPRINT",EDGE,{"derivedFrom":subQ5}),-1.0]])]});}
            var Q1;
            {var subQ6=sQuery(id+"F97.wireOp",EDGE,"E185.bottom");Q1=makeQuery(id+"F97.imprint","IMPRINT",FACE,{"disambiguationData":[TD([[makeQuery(id+"F97.imprint","IMPRINT",EDGE,{"derivedFrom":subQ6}),-1.0]])]});}
            var Q2;
            {var subQ6=sQuery(id+"F97.wireOp",EDGE,"E186.bottom");Q2=makeQuery(id+"F97.imprint","IMPRINT",FACE,{"disambiguationData":[TD([[makeQuery(id+"F97.imprint","IMPRINT",EDGE,{"derivedFrom":subQ6}),-1.0]])]});}
            extrude(context, id + "F98", {"entities" : qUnion([Q0, Q1, Q2]), "operationType" : NewBodyOperationType.ADD, "depth" : 0.8 * mm, "offsetDistance" : 25.4 * mm});
        }
        {
            var Q0;
            Q0=makeQuery(id+"F96.opExtrude","CAP_EDGE",EDGE,{"disambiguationData":[OSD([sQuery(id+"F95.wireOp",EDGE,"E179.left")])],"isStart":false});
            var Q1;
            Q1=makeQuery(id+"F96.opExtrude","CAP_EDGE",EDGE,{"disambiguationData":[OSD([sQuery(id+"F95.wireOp",EDGE,"E179.left")])],"isStart":true});
            var Q2;
            Q2=makeQuery(id+"F96.opExtrude","CAP_EDGE",EDGE,{"disambiguationData":[OSD([sQuery(id+"F95.wireOp",EDGE,"E179.right")])],"isStart":false});
            var Q3;
            Q3=makeQuery(id+"F98.opExtrude","CAP_EDGE",EDGE,{"disambiguationData":[OSD([sQuery(id+"F97.wireOp",EDGE,"E187.top")])],"isStart":false});
            var Q4;
            Q4=makeQuery(id+"F98.opExtrude","CAP_EDGE",EDGE,{"disambiguationData":[OSD([sQuery(id+"F97.wireOp",EDGE,"E187.right")])],"isStart":false});
            var Q5;
            {var subQ0=sQuery(id+"F86.wireOp",EDGE,"E158");Q5=makeQuery(id+"F98.boolean.opBoolean","MERGE",EDGE,{"derivedFrom":[makeQuery(id+"F88.opFillet","BLEND_EDGE",EDGE,{"blendedFrom":[makeQuery(id+"F87.opExtrude","CAP_EDGE",EDGE,{"disambiguationData":[OSD([subQ0])],"isStart":true}),makeQuery(id+"F87.opExtrude","SWEPT_FACE",FACE,{"disambiguationData":[OSD([subQ0])]})],"blendedInto":[makeQuery(id+"F87.opExtrude","SWEPT_FACE",FACE,{"disambiguationData":[OSD([subQ0])]})]}),makeQuery(id+"F98.opExtrude","CAP_EDGE",EDGE,{"disambiguationData":[OSD([sQuery(id+"F97.wireOp",EDGE,"E187.right")])],"isStart":true})]});}
            var Q6;
            Q6=makeQuery(id+"F98.opExtrude","CAP_EDGE",EDGE,{"disambiguationData":[OSD([sQuery(id+"F97.wireOp",EDGE,"E187.bottom")])],"isStart":false});
            var Q7;
            Q7=makeQuery(id+"F96.opExtrude","CAP_EDGE",EDGE,{"disambiguationData":[OSD([sQuery(id+"F95.wireOp",EDGE,"E180.left")])],"isStart":true});
            var Q8;
            Q8=makeQuery(id+"F96.opExtrude","CAP_EDGE",EDGE,{"disambiguationData":[OSD([sQuery(id+"F95.wireOp",EDGE,"E180.left")])],"isStart":false});
            var Q9;
            Q9=makeQuery(id+"F96.opExtrude","CAP_EDGE",EDGE,{"disambiguationData":[OSD([sQuery(id+"F95.wireOp",EDGE,"E180.right")])],"isStart":false});
            var Q10;
            Q10=makeQuery(id+"F96.opExtrude","CAP_EDGE",EDGE,{"disambiguationData":[OSD([sQuery(id+"F95.wireOp",EDGE,"E181.right")])],"isStart":false});
            var Q11;
            Q11=makeQuery(id+"F96.opExtrude","CAP_EDGE",EDGE,{"disambiguationData":[OSD([sQuery(id+"F95.wireOp",EDGE,"E181.left")])],"isStart":false});
            var Q12;
            Q12=makeQuery(id+"F96.opExtrude","CAP_EDGE",EDGE,{"disambiguationData":[OSD([sQuery(id+"F95.wireOp",EDGE,"E181.left")])],"isStart":true});
            var Q13;
            Q13=makeQuery(id+"F96.opExtrude","CAP_EDGE",EDGE,{"disambiguationData":[OSD([sQuery(id+"F95.wireOp",EDGE,"E183.left")])],"isStart":true});
            var Q14;
            Q14=makeQuery(id+"F96.opExtrude","CAP_EDGE",EDGE,{"disambiguationData":[OSD([sQuery(id+"F95.wireOp",EDGE,"E183.left")])],"isStart":false});
            var Q15;
            {var subQ0=sQuery(id+"F97.wireOp",EDGE,"E186.left");Q15=makeQuery(id+"F98.boolean.opBoolean","SPLIT",EDGE,{"disambiguationData":[topologyDisambiguationEdgeConnected([makeQuery(id+"F96.opExtrude","SWEPT_FACE",FACE,{"disambiguationData":[OSD([sQuery(id+"F95.wireOp",EDGE,"E182.right")])]})])],"derivedFrom":makeQuery(id+"F98.opExtrude","CAP_EDGE",EDGE,{"disambiguationData":[OSD([subQ0])],"isStart":false})});}
            var Q16;
            Q16=makeQuery(id+"F96.opExtrude","CAP_EDGE",EDGE,{"disambiguationData":[OSD([sQuery(id+"F95.wireOp",EDGE,"E182.right")])],"isStart":false});
            var Q17;
            Q17=makeQuery(id+"F96.opExtrude","CAP_EDGE",EDGE,{"disambiguationData":[OSD([sQuery(id+"F95.wireOp",EDGE,"E183.right")])],"isStart":false});
            var Q18;
            Q18=makeQuery(id+"F96.opExtrude","CAP_EDGE",EDGE,{"disambiguationData":[OSD([sQuery(id+"F95.wireOp",EDGE,"E182.left")])],"isStart":true});
            var Q19;
            Q19=makeQuery(id+"F96.opExtrude","CAP_EDGE",EDGE,{"disambiguationData":[OSD([sQuery(id+"F95.wireOp",EDGE,"E182.left")])],"isStart":false});
            var Q20;
            {var subQ0=sQuery(id+"F97.wireOp",EDGE,"E186.right");Q20=makeQuery(id+"F98.boolean.opBoolean","SPLIT",EDGE,{"disambiguationData":[topologyDisambiguationEdgeConnected([makeQuery(id+"F96.opExtrude","SWEPT_FACE",FACE,{"disambiguationData":[OSD([sQuery(id+"F95.wireOp",EDGE,"E183.right")])]})])],"derivedFrom":makeQuery(id+"F98.opExtrude","CAP_EDGE",EDGE,{"disambiguationData":[OSD([subQ0])],"isStart":false})});}
            var Q21;
            Q21=makeQuery(id+"F96.opExtrude","CAP_EDGE",EDGE,{"disambiguationData":[OSD([sQuery(id+"F95.wireOp",EDGE,"E184.right")])],"isStart":true});
            var Q22;
            Q22=makeQuery(id+"F96.opExtrude","CAP_EDGE",EDGE,{"disambiguationData":[OSD([sQuery(id+"F95.wireOp",EDGE,"E184.right")])],"isStart":false});
            var Q23;
            Q23=makeQuery(id+"F96.opExtrude","CAP_EDGE",EDGE,{"disambiguationData":[OSD([sQuery(id+"F95.wireOp",EDGE,"E184.left")])],"isStart":false});
            var Q24;
            {var subQ0=sQuery(id+"F86.wireOp",EDGE,"E158");Q24=makeQuery(id+"F96.boolean.opBoolean","MERGE",EDGE,{"derivedFrom":[makeQuery(id+"F88.opFillet","BLEND_EDGE",EDGE,{"blendedFrom":[makeQuery(id+"F87.opExtrude","CAP_EDGE",EDGE,{"disambiguationData":[OSD([subQ0])],"isStart":false}),makeQuery(id+"F87.opExtrude","SWEPT_FACE",FACE,{"disambiguationData":[OSD([subQ0])]})],"blendedInto":[makeQuery(id+"F87.opExtrude","SWEPT_FACE",FACE,{"disambiguationData":[OSD([subQ0])]})]}),makeQuery(id+"F96.opExtrude","CAP_EDGE",EDGE,{"disambiguationData":[OSD([sQuery(id+"F95.wireOp",EDGE,"E184.left")])],"isStart":true})]});}
            var Q25;
            {var subQ0=sQuery(id+"F97.wireOp",EDGE,"E185.left");Q25=makeQuery(id+"F98.boolean.opBoolean","SPLIT",EDGE,{"disambiguationData":[topologyDisambiguationEdgeConnected([makeQuery(id+"F96.opExtrude","SWEPT_FACE",FACE,{"disambiguationData":[OSD([sQuery(id+"F95.wireOp",EDGE,"E180.right")])]})])],"derivedFrom":makeQuery(id+"F98.opExtrude","CAP_EDGE",EDGE,{"disambiguationData":[OSD([subQ0])],"isStart":false})});}
            var Q26;
            {var subQ0=sQuery(id+"F97.wireOp",EDGE,"E187.left");Q26=makeQuery(id+"F98.boolean.opBoolean","SPLIT",EDGE,{"disambiguationData":[topologyDisambiguationEdgeConnected([makeQuery(id+"F96.opExtrude","SWEPT_FACE",FACE,{"disambiguationData":[OSD([sQuery(id+"F95.wireOp",EDGE,"E179.right")])]})])],"derivedFrom":makeQuery(id+"F98.opExtrude","CAP_EDGE",EDGE,{"disambiguationData":[OSD([subQ0])],"isStart":false})});}
            fillet(context, id + "F99", {"entities" : qUnion([Q0, Q1, Q2, Q3, Q4, Q5, Q6, Q7, Q8, Q9, Q10, Q11, Q12, Q13, Q14, Q15, Q16, Q17, Q18, Q19, Q20, Q21, Q22, Q23, Q24, Q25, Q26]), "radius" : 0.25 * mm, "tangentPropagation" : true, "allowEdgeOverflow" : false});
        }
        {
            var Q0;
            {var subQ0=sQuery(id+"F6.wireOp",EDGE,"E9");var subQ1=sQuery(id+"F0.wireOp",EDGE,"E0.right");var subQ2=sQuery(id+"F0.wireOp",EDGE,"E0.bottom");var subQ3=sQuery(id+"F0.wireOp",EDGE,"E0.left");var subQ4=sQuery(id+"F0.wireOp",EDGE,"E0.top");var subQ5=sQuery(id+"F6.wireOp",EDGE,"E17");var subQ6=sQuery(id+"F4.wireOp",EDGE,"E8.0");var subQ7=sQuery(id+"F4.wireOp",EDGE,"E3.0");var subQ8=sQuery(id+"F4.wireOp",EDGE,"E2.0");var subQ9=sQuery(id+"F4.wireOp",EDGE,"E7.0");var subQ10=sQuery(id+"F4.wireOp",EDGE,"E6.0");var subQ11=sQuery(id+"F4.wireOp",EDGE,"E4.0");var subQ12=sQuery(id+"F4.wireOp",EDGE,"E5.0");var subQ13=sQuery(id+"F4.wireOp",EDGE,"E1.0");Q0=makeQuery(id+"F68.boolean.opBoolean","SPLIT",FACE,{"disambiguationData":[TD([makeQuery(id+"F5.opExtrude","SWEPT_FACE",FACE,{"disambiguationData":[OSD([subQ8])]})])],"derivedFrom":makeQuery(id+"F11.boolean.opBoolean","MERGE",FACE,{"derivedFrom":[makeQuery(id+"F7.boolean.opBoolean","MERGE",FACE,{"derivedFrom":[makeQuery(id+"F5.opExtrude","CAP_FACE",FACE,{"disambiguationData":[OSD([subQ2,subQ4,subQ3,subQ1,subQ13,subQ8,subQ7,subQ11,subQ12,subQ10,subQ9,subQ6])],"isStart":false}),makeQuery(id+"F7.opExtrude","CAP_FACE",FACE,{"disambiguationData":[OSD([subQ8,subQ7,subQ0])],"isStart":false}),makeQuery(id+"F7.opExtrude","CAP_FACE",FACE,{"disambiguationData":[OSD([subQ13,subQ7,sQuery(id+"F6.wireOp",EDGE,"E11")])],"isStart":false}),makeQuery(id+"F7.opExtrude","CAP_FACE",FACE,{"disambiguationData":[OSD([subQ12,subQ10,sQuery(id+"F6.wireOp",EDGE,"E12")])],"isStart":false}),makeQuery(id+"F7.opExtrude","CAP_FACE",FACE,{"disambiguationData":[OSD([subQ11,subQ10,sQuery(id+"F6.wireOp",EDGE,"E13")])],"isStart":false}),makeQuery(id+"F7.opExtrude","CAP_FACE",FACE,{"disambiguationData":[OSD([subQ9,sQuery(id+"F6.wireOp",EDGE,"E14")])],"isStart":false}),makeQuery(id+"F7.opExtrude","CAP_FACE",FACE,{"disambiguationData":[OSD([subQ9,sQuery(id+"F6.wireOp",EDGE,"E15")])],"isStart":false}),makeQuery(id+"F7.opExtrude","CAP_FACE",FACE,{"disambiguationData":[OSD([subQ6,sQuery(id+"F6.wireOp",EDGE,"E16")])],"isStart":false}),makeQuery(id+"F7.opExtrude","CAP_FACE",FACE,{"disambiguationData":[OSD([subQ6,subQ5])],"isStart":false})]}),makeQuery(id+"F11.opExtrude","CAP_FACE",FACE,{"disambiguationData":[OSD([sQuery(id+"F10.wireOp",EDGE,"E26"),sQuery(id+"F10.wireOp",EDGE,"E27"),sQuery(id+"F10.wireOp",EDGE,"E28"),sQuery(id+"F10.wireOp",EDGE,"E29")])],"isStart":false}),makeQuery(id+"F11.opExtrude","CAP_FACE",FACE,{"disambiguationData":[OSD([sQuery(id+"F10.wireOp",EDGE,"E34"),sQuery(id+"F10.wireOp",EDGE,"E35"),sQuery(id+"F10.wireOp",EDGE,"E36"),sQuery(id+"F10.wireOp",EDGE,"E37")])],"isStart":false}),makeQuery(id+"F11.opExtrude","CAP_FACE",FACE,{"disambiguationData":[OSD([sQuery(id+"F10.wireOp",EDGE,"E42"),sQuery(id+"F10.wireOp",EDGE,"E43"),sQuery(id+"F10.wireOp",EDGE,"E44"),sQuery(id+"F10.wireOp",EDGE,"E45")])],"isStart":false}),makeQuery(id+"F11.opExtrude","CAP_FACE",FACE,{"disambiguationData":[OSD([sQuery(id+"F10.wireOp",EDGE,"E47"),sQuery(id+"F10.wireOp",EDGE,"E48"),sQuery(id+"F10.wireOp",EDGE,"E49"),sQuery(id+"F10.wireOp",EDGE,"E50")])],"isStart":false})]})});}
            var Q1;
            Q1=makeQuery(id+"F44.opExtrude","CAP_FACE",FACE,{"disambiguationData":[OSD([sQuery(id+"F43.wireOp",EDGE,"E84.bottom"),sQuery(id+"F43.wireOp",EDGE,"E84.top"),sQuery(id+"F43.wireOp",EDGE,"E84.left"),sQuery(id+"F43.wireOp",EDGE,"E84.right"),sQuery(id+"F43.wireOp",EDGE,"E85.top"),sQuery(id+"F43.wireOp",EDGE,"E85.left"),sQuery(id+"F43.wireOp",EDGE,"E85.right"),sQuery(id+"F43.wireOp",EDGE,"E86.trimOffspring")])],"isStart":false});
            var Q2;
            Q2=makeQuery(id+"F39.opExtrude","CAP_FACE",FACE,{"disambiguationData":[OSD([sQuery(id+"F38.wireOp",EDGE,"E82.bottom"),sQuery(id+"F38.wireOp",EDGE,"E82.top"),sQuery(id+"F38.wireOp",EDGE,"E82.left"),sQuery(id+"F38.wireOp",EDGE,"E82.right")])],"isStart":false});
            var Q3;
            Q3=makeQuery(id+"F56.opExtrude","CAP_FACE",FACE,{"disambiguationData":[OSD([sQuery(id+"F55.wireOp",EDGE,"E102.bottom"),sQuery(id+"F55.wireOp",EDGE,"E102.top"),sQuery(id+"F55.wireOp",EDGE,"E103"),sQuery(id+"F55.wireOp",EDGE,"E104"),sQuery(id+"F55.wireOp",EDGE,"E105"),sQuery(id+"F55.wireOp",EDGE,"E106")])],"isStart":false});
            var Q4;
            Q4=makeQuery(id+"F27.opExtrude","CAP_FACE",FACE,{"disambiguationData":[OSD([sQuery(id+"F26.wireOp",EDGE,"E60.bottom"),sQuery(id+"F26.wireOp",EDGE,"E60.top"),sQuery(id+"F26.wireOp",EDGE,"E60.left"),sQuery(id+"F26.wireOp",EDGE,"E60.right")])],"isStart":false});
            var Q5;
            Q5=makeQuery(id+"F22.opExtrude","CAP_FACE",FACE,{"disambiguationData":[OSD([sQuery(id+"F21.wireOp",EDGE,"E56.bottom"),sQuery(id+"F21.wireOp",EDGE,"E56.top"),sQuery(id+"F21.wireOp",EDGE,"E56.left"),sQuery(id+"F21.wireOp",EDGE,"E56.right")])],"isStart":false});
            var Q6;
            {var subQ0=sQuery(id+"F6.wireOp",EDGE,"E13");var subQ1=sQuery(id+"F0.wireOp",EDGE,"E0.bottom");var subQ2=sQuery(id+"F0.wireOp",EDGE,"E0.right");var subQ3=sQuery(id+"F0.wireOp",EDGE,"E0.left");var subQ4=sQuery(id+"F0.wireOp",EDGE,"E0.top");var subQ5=sQuery(id+"F4.wireOp",EDGE,"E8.0");var subQ6=sQuery(id+"F4.wireOp",EDGE,"E6.0");var subQ7=sQuery(id+"F4.wireOp",EDGE,"E4.0");var subQ8=sQuery(id+"F6.wireOp",EDGE,"E16");var subQ9=sQuery(id+"F4.wireOp",EDGE,"E7.0");var subQ10=sQuery(id+"F4.wireOp",EDGE,"E5.0");var subQ11=sQuery(id+"F4.wireOp",EDGE,"E3.0");var subQ12=sQuery(id+"F4.wireOp",EDGE,"E1.0");var subQ13=sQuery(id+"F4.wireOp",EDGE,"E2.0");Q6=makeQuery(id+"F68.boolean.opBoolean","SPLIT",FACE,{"disambiguationData":[TD([makeQuery(id+"F5.opExtrude","SWEPT_FACE",FACE,{"disambiguationData":[OSD([subQ7])]})])],"derivedFrom":makeQuery(id+"F11.boolean.opBoolean","MERGE",FACE,{"derivedFrom":[makeQuery(id+"F7.boolean.opBoolean","MERGE",FACE,{"derivedFrom":[makeQuery(id+"F5.opExtrude","CAP_FACE",FACE,{"disambiguationData":[OSD([subQ1,subQ4,subQ3,subQ2,subQ12,subQ13,subQ11,subQ7,subQ10,subQ6,subQ9,subQ5])],"isStart":false}),makeQuery(id+"F7.opExtrude","CAP_FACE",FACE,{"disambiguationData":[OSD([subQ13,subQ11,sQuery(id+"F6.wireOp",EDGE,"E9")])],"isStart":false}),makeQuery(id+"F7.opExtrude","CAP_FACE",FACE,{"disambiguationData":[OSD([subQ12,subQ11,sQuery(id+"F6.wireOp",EDGE,"E11")])],"isStart":false}),makeQuery(id+"F7.opExtrude","CAP_FACE",FACE,{"disambiguationData":[OSD([subQ10,subQ6,sQuery(id+"F6.wireOp",EDGE,"E12")])],"isStart":false}),makeQuery(id+"F7.opExtrude","CAP_FACE",FACE,{"disambiguationData":[OSD([subQ7,subQ6,subQ0])],"isStart":false}),makeQuery(id+"F7.opExtrude","CAP_FACE",FACE,{"disambiguationData":[OSD([subQ9,sQuery(id+"F6.wireOp",EDGE,"E14")])],"isStart":false}),makeQuery(id+"F7.opExtrude","CAP_FACE",FACE,{"disambiguationData":[OSD([subQ9,sQuery(id+"F6.wireOp",EDGE,"E15")])],"isStart":false}),makeQuery(id+"F7.opExtrude","CAP_FACE",FACE,{"disambiguationData":[OSD([subQ5,subQ8])],"isStart":false}),makeQuery(id+"F7.opExtrude","CAP_FACE",FACE,{"disambiguationData":[OSD([subQ5,sQuery(id+"F6.wireOp",EDGE,"E17")])],"isStart":false})]}),makeQuery(id+"F11.opExtrude","CAP_FACE",FACE,{"disambiguationData":[OSD([sQuery(id+"F10.wireOp",EDGE,"E26"),sQuery(id+"F10.wireOp",EDGE,"E27"),sQuery(id+"F10.wireOp",EDGE,"E28"),sQuery(id+"F10.wireOp",EDGE,"E29")])],"isStart":false}),makeQuery(id+"F11.opExtrude","CAP_FACE",FACE,{"disambiguationData":[OSD([sQuery(id+"F10.wireOp",EDGE,"E34"),sQuery(id+"F10.wireOp",EDGE,"E35"),sQuery(id+"F10.wireOp",EDGE,"E36"),sQuery(id+"F10.wireOp",EDGE,"E37")])],"isStart":false}),makeQuery(id+"F11.opExtrude","CAP_FACE",FACE,{"disambiguationData":[OSD([sQuery(id+"F10.wireOp",EDGE,"E42"),sQuery(id+"F10.wireOp",EDGE,"E43"),sQuery(id+"F10.wireOp",EDGE,"E44"),sQuery(id+"F10.wireOp",EDGE,"E45")])],"isStart":false}),makeQuery(id+"F11.opExtrude","CAP_FACE",FACE,{"disambiguationData":[OSD([sQuery(id+"F10.wireOp",EDGE,"E47"),sQuery(id+"F10.wireOp",EDGE,"E48"),sQuery(id+"F10.wireOp",EDGE,"E49"),sQuery(id+"F10.wireOp",EDGE,"E50")])],"isStart":false})]})});}
            var Q7;
            {var subQ0=sQuery(id+"F6.wireOp",EDGE,"E14");var subQ1=sQuery(id+"F10.wireOp",EDGE,"E26");var subQ2=sQuery(id+"F6.wireOp",EDGE,"E12");var subQ3=sQuery(id+"F0.wireOp",EDGE,"E0.right");var subQ4=sQuery(id+"F6.wireOp",EDGE,"E11");var subQ5=sQuery(id+"F0.wireOp",EDGE,"E0.left");var subQ6=sQuery(id+"F0.wireOp",EDGE,"E0.top");var subQ7=sQuery(id+"F0.wireOp",EDGE,"E0.bottom");var subQ9=sQuery(id+"F4.wireOp",EDGE,"E6.0");var subQ10=sQuery(id+"F6.wireOp",EDGE,"E15");var subQ11=sQuery(id+"F10.wireOp",EDGE,"E27");var subQ12=sQuery(id+"F4.wireOp",EDGE,"E5.0");var subQ13=sQuery(id+"F4.wireOp",EDGE,"E1.0");var subQ14=sQuery(id+"F4.wireOp",EDGE,"E3.0");var subQ15=sQuery(id+"F4.wireOp",EDGE,"E7.0");var subQ16=sQuery(id+"F10.wireOp",EDGE,"E43");var subQ17=sQuery(id+"F10.wireOp",EDGE,"E28");var subQ18=sQuery(id+"F10.wireOp",EDGE,"E34");var subQ19=sQuery(id+"F10.wireOp",EDGE,"E35");var subQ20=sQuery(id+"F10.wireOp",EDGE,"E36");var subQ21=sQuery(id+"F10.wireOp",EDGE,"E42");var subQ22=sQuery(id+"F10.wireOp",EDGE,"E44");var subQ23=sQuery(id+"F10.wireOp",EDGE,"E47");var subQ26=sQuery(id+"F10.wireOp",EDGE,"E48");var subQ27=sQuery(id+"F10.wireOp",EDGE,"E49");var subQ28=sQuery(id+"F4.wireOp",EDGE,"E8.0");var subQ29=sQuery(id+"F4.wireOp",EDGE,"E4.0");var subQ30=sQuery(id+"F4.wireOp",EDGE,"E2.0");Q7=makeQuery(id+"F68.boolean.opBoolean","SPLIT",FACE,{"disambiguationData":[TD([makeQuery(id+"F1.opExtrude","SWEPT_FACE",FACE,{"disambiguationData":[OSD([subQ6])]})])],"derivedFrom":makeQuery(id+"F11.boolean.opBoolean","MERGE",FACE,{"derivedFrom":[makeQuery(id+"F7.boolean.opBoolean","MERGE",FACE,{"derivedFrom":[makeQuery(id+"F5.opExtrude","CAP_FACE",FACE,{"disambiguationData":[OSD([subQ7,subQ6,subQ5,subQ3,subQ13,subQ30,subQ14,subQ29,subQ12,subQ9,subQ15,subQ28])],"isStart":false}),makeQuery(id+"F7.opExtrude","CAP_FACE",FACE,{"disambiguationData":[OSD([subQ30,subQ14,sQuery(id+"F6.wireOp",EDGE,"E9")])],"isStart":false}),makeQuery(id+"F7.opExtrude","CAP_FACE",FACE,{"disambiguationData":[OSD([subQ13,subQ14,subQ4])],"isStart":false}),makeQuery(id+"F7.opExtrude","CAP_FACE",FACE,{"disambiguationData":[OSD([subQ12,subQ9,subQ2])],"isStart":false}),makeQuery(id+"F7.opExtrude","CAP_FACE",FACE,{"disambiguationData":[OSD([subQ29,subQ9,sQuery(id+"F6.wireOp",EDGE,"E13")])],"isStart":false}),makeQuery(id+"F7.opExtrude","CAP_FACE",FACE,{"disambiguationData":[OSD([subQ15,subQ0])],"isStart":false}),makeQuery(id+"F7.opExtrude","CAP_FACE",FACE,{"disambiguationData":[OSD([subQ15,subQ10])],"isStart":false}),makeQuery(id+"F7.opExtrude","CAP_FACE",FACE,{"disambiguationData":[OSD([subQ28,sQuery(id+"F6.wireOp",EDGE,"E16")])],"isStart":false}),makeQuery(id+"F7.opExtrude","CAP_FACE",FACE,{"disambiguationData":[OSD([subQ28,sQuery(id+"F6.wireOp",EDGE,"E17")])],"isStart":false})]}),makeQuery(id+"F11.opExtrude","CAP_FACE",FACE,{"disambiguationData":[OSD([subQ1,subQ11,subQ17,sQuery(id+"F10.wireOp",EDGE,"E29")])],"isStart":false}),makeQuery(id+"F11.opExtrude","CAP_FACE",FACE,{"disambiguationData":[OSD([subQ18,subQ19,subQ20,sQuery(id+"F10.wireOp",EDGE,"E37")])],"isStart":false}),makeQuery(id+"F11.opExtrude","CAP_FACE",FACE,{"disambiguationData":[OSD([subQ21,subQ16,subQ22,sQuery(id+"F10.wireOp",EDGE,"E45")])],"isStart":false}),makeQuery(id+"F11.opExtrude","CAP_FACE",FACE,{"disambiguationData":[OSD([subQ23,subQ26,subQ27,sQuery(id+"F10.wireOp",EDGE,"E50")])],"isStart":false})]})});}
            fillet(context, id + "F100", {"entities" : qUnion([Q0, Q1, Q2, Q3, Q4, Q5, Q6, Q7]), "radius" : 0.25 * mm, "tangentPropagation" : true, "allowEdgeOverflow" : false});
        }
        {
            var Q0;
            Q0=makeQuery(id+"F75.opExtrude","CAP_FACE",FACE,{"disambiguationData":[OSD([sQuery(id+"F74.wireOp",EDGE,"E136.bottom"),sQuery(id+"F74.wireOp",EDGE,"E136.top"),sQuery(id+"F74.wireOp",EDGE,"E136.left"),sQuery(id+"F74.wireOp",EDGE,"E136.right"),sQuery(id+"F74.wireOp",EDGE,"E137.top"),sQuery(id+"F74.wireOp",EDGE,"E137.left"),sQuery(id+"F74.wireOp",EDGE,"E137.right"),sQuery(id+"F74.wireOp",EDGE,"E138.top"),sQuery(id+"F74.wireOp",EDGE,"E138.left"),sQuery(id+"F74.wireOp",EDGE,"E138.right")])],"isStart":false});
            var sketch = newSketch(context, id + "F101", { "sketchPlane" : qUnion([Q0])});
            skLineSegment(sketch, "E188.bottom", {"start": v(147.62, -82.66) * mm, "end": v(-147.62, -82.66) * mm});
            skLineSegment(sketch, "E188.top", {"start": v(147.62, -171.5) * mm, "end": v(-147.62, -171.5) * mm});
            skLineSegment(sketch, "E188.left", {"start": v(147.62, -82.66) * mm, "end": v(147.62, -171.5) * mm});
            skLineSegment(sketch, "E188.right", {"start": v(-147.62, -82.66) * mm, "end": v(-147.62, -171.5) * mm});
            skPoint(sketch, "E188.middle", {"position": v(0, -127.08) * mm});
            skPoint(sketch, "E188.middle.positionSnap0", {"position": v(-166.69, -127.08) * mm});
            skPoint(sketch, "E188.centerSnap0", {"position": v(-166.69, -127.08) * mm});
            skSolve(sketch);
        }
        {
            var Q0;
            Q0=makeQuery(id+"F101.imprint","IMPRINT",FACE,{"disambiguationData":[TD([[makeQuery(id+"F101.imprint","IMPRINT",EDGE,{"derivedFrom":sQuery(id+"F101.wireOp",EDGE,"E188.bottom")}),1.0]])]});
            extrude(context, id + "F102", {"entities" : qUnion([Q0]), "operationType" : NewBodyOperationType.REMOVE, "endBound" : BoundingType.THROUGH_ALL, "oppositeDirection" : true, "depth" : 25.4 * mm, "offsetDistance" : 25.4 * mm});
        }
        {
            var Q0;
            Q0=qCreatedBy(makeId("Top.planeOp"),FACE);
            var sketch = newSketch(context, id + "F103", { "sketchPlane" : qUnion([Q0])});
            skLineSegment(sketch, "E189.bottom", {"start": v(-161.92, -269.1) * mm, "end": v(161.93, -269.1) * mm});
            skLineSegment(sketch, "E189.top", {"start": v(-161.92, -367.52) * mm, "end": v(161.93, -367.52) * mm});
            skLineSegment(sketch, "E189.left", {"start": v(-161.92, -269.1) * mm, "end": v(-161.92, -367.52) * mm});
            skLineSegment(sketch, "E189.right", {"start": v(161.93, -269.1) * mm, "end": v(161.93, -367.52) * mm});
            skSolve(sketch);
        }
        {
            var Q0;
            Q0=qSketchRegion(id+"F103",true);
            extrude(context, id + "F104", {"entities" : qUnion([Q0]), "depth" : 50.8 * mm, "offsetDistance" : 25.4 * mm});
        }
        {
            var Q0;
            Q0=makeQuery(id+"F104.opExtrude","SWEPT_EDGE",EDGE,{"disambiguationData":[OSD([sQuery(id+"F103.wireOp",EDGE,"E189.bottom"),sQuery(id+"F103.wireOp",EDGE,"E189.right")])]});
            var Q1;
            Q1=makeQuery(id+"F104.opExtrude","SWEPT_EDGE",EDGE,{"disambiguationData":[OSD([sQuery(id+"F103.wireOp",EDGE,"E189.bottom"),sQuery(id+"F103.wireOp",EDGE,"E189.left")])]});
            fillet(context, id + "F105", {"entities" : qUnion([Q0, Q1]), "radius" : 9.52 * mm, "tangentPropagation" : true, "allowEdgeOverflow" : false});
        }
        {
            var Q0;
            Q0=makeQuery(id+"F104.opExtrude","SWEPT_EDGE",EDGE,{"disambiguationData":[OSD([sQuery(id+"F103.wireOp",EDGE,"E189.top"),sQuery(id+"F103.wireOp",EDGE,"E189.right")])]});
            var Q1;
            Q1=makeQuery(id+"F104.opExtrude","SWEPT_EDGE",EDGE,{"disambiguationData":[OSD([sQuery(id+"F103.wireOp",EDGE,"E189.top"),sQuery(id+"F103.wireOp",EDGE,"E189.left")])]});
            fillet(context, id + "F106", {"entities" : qUnion([Q0, Q1]), "radius" : 15.88 * mm, "tangentPropagation" : true, "allowEdgeOverflow" : false});
        }
        {
            var Q0;
            Q0=makeQuery(id+"F104.opExtrude","SWEPT_FACE",FACE,{"disambiguationData":[OSD([sQuery(id+"F103.wireOp",EDGE,"E189.right")])]});
            var sketch = newSketch(context, id + "F107", { "sketchPlane" : qUnion([Q0])});
            skLineSegment(sketch, "E190", {"start": v(-269.1, 4.75) * mm, "end": v(-367.52, 50.8) * mm});
            skLineSegment(sketch, "E191", {"start": v(-269.1, 4.75) * mm, "end": v(-269.1, -4.61) * mm});
            skLineSegment(sketch, "E192", {"start": v(-269.1, -4.61) * mm, "end": v(-367.52, -4.61) * mm});
            skLineSegment(sketch, "E193", {"start": v(-367.52, -4.61) * mm, "end": v(-367.52, 50.8) * mm});
            skSolve(sketch);
        }
        {
            var Q0;
            Q0=qSketchRegion(id+"F107",true);
            extrude(context, id + "F108", {"entities" : qUnion([Q0]), "operationType" : NewBodyOperationType.REMOVE, "endBound" : BoundingType.THROUGH_ALL, "oppositeDirection" : true, "depth" : 25.4 * mm, "offsetDistance" : 25.4 * mm});
        }
        {
            var Q0;
            Q0=makeQuery(id+"F104.opExtrude","SWEPT_FACE",FACE,{"disambiguationData":[OSD([sQuery(id+"F103.wireOp",EDGE,"E189.bottom")])]});
            var sketch = newSketch(context, id + "F109", { "sketchPlane" : qUnion([Q0])});
            skLineSegment(sketch, "E194", {"start": v(-106.36, 50.8) * mm, "end": v(-111.13, 14.29) * mm});
            skLineSegment(sketch, "E195", {"start": v(-111.13, 14.29) * mm, "end": v(-60.33, 14.29) * mm});
            skLineSegment(sketch, "E196", {"start": v(-60.33, 14.29) * mm, "end": v(-65.09, 50.8) * mm});
            skLineSegment(sketch, "E197", {"start": v(-65.09, 50.8) * mm, "end": v(-106.36, 50.8) * mm});
            skLineSegment(sketch, "E198", {"start": v(-85.73, 14.29) * mm, "end": v(-85.73, 50.8) * mm, "construction": true});
            skLineSegment(sketch, "E199", {"start": v(-111.13, 14.29) * mm, "end": v(-111.13, 46.62) * mm, "construction": true});
            skLineSegment(sketch, "E200", {"start": v(-60.33, 14.29) * mm, "end": v(-60.33, 82.26) * mm, "construction": true});
            skLineSegment(sketch, "E201", {"start": v(36.53, 50.8) * mm, "end": v(31.75, 14.29) * mm});
            skLineSegment(sketch, "E202", {"start": v(31.75, 14.29) * mm, "end": v(82.55, 14.29) * mm});
            skLineSegment(sketch, "E203", {"start": v(82.55, 14.29) * mm, "end": v(77.77, 50.8) * mm});
            skLineSegment(sketch, "E204", {"start": v(77.77, 50.8) * mm, "end": v(36.53, 50.8) * mm});
            skLineSegment(sketch, "E205", {"start": v(31.75, 14.29) * mm, "end": v(31.75, 42.1) * mm, "construction": true});
            skLineSegment(sketch, "E206", {"start": v(82.55, 14.29) * mm, "end": v(82.55, 85.26) * mm, "construction": true});
            skLineSegment(sketch, "E207", {"start": v(149.22, 50.8) * mm, "end": v(149.22, 14.29) * mm});
            skLineSegment(sketch, "E208", {"start": v(149.22, 14.29) * mm, "end": v(111.12, 14.29) * mm});
            skLineSegment(sketch, "E209", {"start": v(111.12, 14.29) * mm, "end": v(115.9, 50.8) * mm});
            skLineSegment(sketch, "E210", {"start": v(115.9, 50.8) * mm, "end": v(149.22, 50.8) * mm});
            skLineSegment(sketch, "E211", {"start": v(111.12, 14.29) * mm, "end": v(111.12, 60.3) * mm, "construction": true});
            skSolve(sketch);
        }
        {
            var Q0;
            Q0=qSketchRegion(id+"F109",true);
            extrude(context, id + "F110", {"entities" : qUnion([Q0]), "operationType" : NewBodyOperationType.REMOVE, "oppositeDirection" : true, "depth" : 5.5 * mm, "offsetDistance" : 25.4 * mm});
        }
        {
            var Q0;
            Q0=makeQuery(id+"F110.boolean.opBoolean","COPY",EDGE,{"derivedFrom":makeQuery(id+"F110.opExtrude","CAP_EDGE",EDGE,{"disambiguationData":[OSD([sQuery(id+"F109.wireOp",EDGE,"E203")])],"isStart":false})});
            var Q1;
            Q1=makeQuery(id+"F110.boolean.opBoolean","COPY",EDGE,{"derivedFrom":makeQuery(id+"F110.opExtrude","CAP_EDGE",EDGE,{"disambiguationData":[OSD([sQuery(id+"F109.wireOp",EDGE,"E201")])],"isStart":false})});
            var Q2;
            Q2=makeQuery(id+"F110.boolean.opBoolean","COPY",EDGE,{"derivedFrom":makeQuery(id+"F110.opExtrude","CAP_EDGE",EDGE,{"disambiguationData":[OSD([sQuery(id+"F109.wireOp",EDGE,"E209")])],"isStart":false})});
            var Q3;
            Q3=makeQuery(id+"F110.boolean.opBoolean","COPY",EDGE,{"derivedFrom":makeQuery(id+"F110.opExtrude","CAP_EDGE",EDGE,{"disambiguationData":[OSD([sQuery(id+"F109.wireOp",EDGE,"E194")])],"isStart":false})});
            var Q4;
            Q4=makeQuery(id+"F110.boolean.opBoolean","COPY",EDGE,{"derivedFrom":makeQuery(id+"F110.opExtrude","CAP_EDGE",EDGE,{"disambiguationData":[OSD([sQuery(id+"F109.wireOp",EDGE,"E196")])],"isStart":false})});
            fillet(context, id + "F111", {"entities" : qUnion([Q0, Q1, Q2, Q3, Q4]), "radius" : 22.86 * mm, "tangentPropagation" : true, "allowEdgeOverflow" : false});
        }
        {
            var Q0;
            Q0=makeQuery(id+"F110.boolean.opBoolean","COPY",EDGE,{"derivedFrom":makeQuery(id+"F110.opExtrude","CAP_EDGE",EDGE,{"disambiguationData":[OSD([sQuery(id+"F109.wireOp",EDGE,"E207")])],"isStart":false})});
            var Q1;
            Q1=makeQuery(id+"F110.boolean.opBoolean","COPY",EDGE,{"derivedFrom":makeQuery(id+"F110.opExtrude","CAP_EDGE",EDGE,{"disambiguationData":[OSD([sQuery(id+"F109.wireOp",EDGE,"E208")])],"isStart":false})});
            var Q2;
            Q2=makeQuery(id+"F110.boolean.opBoolean","COPY",EDGE,{"derivedFrom":makeQuery(id+"F110.opExtrude","CAP_EDGE",EDGE,{"disambiguationData":[OSD([sQuery(id+"F109.wireOp",EDGE,"E202")])],"isStart":false})});
            var Q3;
            Q3=makeQuery(id+"F110.boolean.opBoolean","COPY",EDGE,{"derivedFrom":makeQuery(id+"F110.opExtrude","CAP_EDGE",EDGE,{"disambiguationData":[OSD([sQuery(id+"F109.wireOp",EDGE,"E195")])],"isStart":false})});
            fillet(context, id + "F112", {"entities" : qUnion([Q0, Q1, Q2, Q3]), "radius" : 5.08 * mm, "tangentPropagation" : true, "allowEdgeOverflow" : false});
        }
        {
            var Q0;
            Q0=makeQuery(id+"F104.opExtrude","SWEPT_FACE",FACE,{"disambiguationData":[OSD([sQuery(id+"F103.wireOp",EDGE,"E189.bottom")])]});
            var sketch = newSketch(context, id + "F113", { "sketchPlane" : qUnion([Q0])});
            skLineSegment(sketch, "E212.bottom", {"start": v(-115.12, 4.75) * mm, "end": v(-117.5, 4.75) * mm});
            skLineSegment(sketch, "E212.top", {"start": v(-115.12, 26.97) * mm, "end": v(-117.5, 26.97) * mm});
            skLineSegment(sketch, "E212.left", {"start": v(-115.12, 4.75) * mm, "end": v(-115.12, 26.97) * mm});
            skLineSegment(sketch, "E212.right", {"start": v(-117.5, 4.75) * mm, "end": v(-117.5, 26.97) * mm});
            skLineSegment(sketch, "E213.bottom", {"start": v(-55.86, 4.75) * mm, "end": v(-53.48, 4.75) * mm});
            skLineSegment(sketch, "E213.top", {"start": v(-55.86, 26.97) * mm, "end": v(-53.48, 26.97) * mm});
            skLineSegment(sketch, "E213.left", {"start": v(-55.86, 4.75) * mm, "end": v(-55.86, 26.97) * mm});
            skLineSegment(sketch, "E213.right", {"start": v(-53.48, 4.75) * mm, "end": v(-53.48, 26.97) * mm});
            skLineSegment(sketch, "E214.bottom", {"start": v(28.15, 4.75) * mm, "end": v(25.76, 4.75) * mm});
            skLineSegment(sketch, "E214.top", {"start": v(28.15, 26.97) * mm, "end": v(25.76, 26.97) * mm});
            skLineSegment(sketch, "E214.left", {"start": v(28.15, 4.75) * mm, "end": v(28.15, 26.97) * mm});
            skLineSegment(sketch, "E214.right", {"start": v(25.76, 4.75) * mm, "end": v(25.76, 26.97) * mm});
            skLineSegment(sketch, "E215.bottom", {"start": v(85.56, 4.75) * mm, "end": v(87.95, 4.75) * mm});
            skLineSegment(sketch, "E215.top", {"start": v(85.56, 26.97) * mm, "end": v(87.95, 26.97) * mm});
            skLineSegment(sketch, "E215.left", {"start": v(85.56, 4.75) * mm, "end": v(85.56, 26.97) * mm});
            skLineSegment(sketch, "E215.right", {"start": v(87.95, 4.75) * mm, "end": v(87.95, 26.97) * mm});
            skLineSegment(sketch, "E216.bottom", {"start": v(108.34, 4.75) * mm, "end": v(105.96, 4.75) * mm});
            skLineSegment(sketch, "E216.top", {"start": v(108.34, 26.97) * mm, "end": v(105.96, 26.97) * mm});
            skLineSegment(sketch, "E216.left", {"start": v(108.34, 4.75) * mm, "end": v(108.34, 26.97) * mm});
            skLineSegment(sketch, "E216.right", {"start": v(105.96, 4.75) * mm, "end": v(105.96, 26.97) * mm});
            skLineSegment(sketch, "E217.bottom", {"start": v(152.4, 4.75) * mm, "end": v(150.02, 4.75) * mm});
            skLineSegment(sketch, "E217.top", {"start": v(152.4, 26.97) * mm, "end": v(150.02, 26.97) * mm});
            skLineSegment(sketch, "E217.left", {"start": v(152.4, 4.75) * mm, "end": v(152.4, 26.97) * mm});
            skLineSegment(sketch, "E217.right", {"start": v(150.02, 4.75) * mm, "end": v(150.02, 26.97) * mm});
            skSolve(sketch);
        }
        {
            var Q0;
            Q0=qSketchRegion(id+"F113",true);
            extrude(context, id + "F114", {"entities" : qUnion([Q0]), "operationType" : NewBodyOperationType.ADD, "depth" : 1.6 * mm, "offsetDistance" : 25.4 * mm});
        }
        {
            var Q0;
            Q0=makeQuery(id+"F104.opExtrude","SWEPT_FACE",FACE,{"disambiguationData":[OSD([sQuery(id+"F103.wireOp",EDGE,"E189.bottom")])]});
            var sketch = newSketch(context, id + "F115", { "sketchPlane" : qUnion([Q0])});
            skLineSegment(sketch, "E218.bottom", {"start": v(-53.48, 4.75) * mm, "end": v(25.75, 4.75) * mm});
            skLineSegment(sketch, "E218.top", {"start": v(-53.48, 50.79) * mm, "end": v(25.75, 50.79) * mm});
            skLineSegment(sketch, "E218.left", {"start": v(-53.48, 4.75) * mm, "end": v(-53.48, 50.79) * mm});
            skLineSegment(sketch, "E218.right", {"start": v(25.75, 4.75) * mm, "end": v(25.75, 50.79) * mm});
            skLineSegment(sketch, "E219.bottom", {"start": v(87.94, 4.75) * mm, "end": v(105.95, 4.75) * mm});
            skLineSegment(sketch, "E219.top", {"start": v(87.94, 50.79) * mm, "end": v(105.95, 50.79) * mm});
            skLineSegment(sketch, "E219.left", {"start": v(87.94, 4.75) * mm, "end": v(87.94, 50.79) * mm});
            skLineSegment(sketch, "E219.right", {"start": v(105.95, 4.75) * mm, "end": v(105.95, 50.79) * mm});
            skLineSegment(sketch, "E220.bottom", {"start": v(-117.5, 4.75) * mm, "end": v(-152.4, 4.75) * mm});
            skLineSegment(sketch, "E220.top", {"start": v(-117.5, 50.79) * mm, "end": v(-152.4, 50.79) * mm});
            skLineSegment(sketch, "E220.left", {"start": v(-117.5, 4.75) * mm, "end": v(-117.5, 50.79) * mm});
            skLineSegment(sketch, "E220.right", {"start": v(-152.4, 4.75) * mm, "end": v(-152.4, 50.79) * mm});
            skSolve(sketch);
        }
        {
            var Q0;
            Q0=qSketchRegion(id+"F115",true);
            extrude(context, id + "F116", {"entities" : qUnion([Q0]), "operationType" : NewBodyOperationType.ADD, "depth" : 0.79 * mm, "offsetDistance" : 25.4 * mm});
        }
        {
            var Q0;
            Q0=makeQuery(id+"F1.opExtrude","CAP_FACE",FACE,{"disambiguationData":[OSD([sQuery(id+"F0.wireOp",EDGE,"E0.bottom"),sQuery(id+"F0.wireOp",EDGE,"E0.top"),sQuery(id+"F0.wireOp",EDGE,"E0.left"),sQuery(id+"F0.wireOp",EDGE,"E0.right")])],"isStart":true});
            extrude(context, id + "F117", {"entities" : qUnion([Q0]), "operationType" : NewBodyOperationType.ADD, "depth" : 1.59 * mm, "offsetDistance" : 25.4 * mm});
        }
        {
            var Q0;
            Q0=makeQuery(id+"F117.opExtrude","CAP_FACE",FACE,{"disambiguationData":[OSD([sQuery(id+"F0.wireOp",EDGE,"E0.bottom"),sQuery(id+"F0.wireOp",EDGE,"E0.top"),sQuery(id+"F0.wireOp",EDGE,"E0.left"),sQuery(id+"F0.wireOp",EDGE,"E0.right")])],"isStart":false});
            chamfer(context, id + "F118", {"entities" : qUnion([Q0]), "width" : 0.76 * mm, "tangentPropagation" : true});
        }
        {
            var Q0;
            Q0=makeQuery(id+"F37.boolean.opBoolean","MERGE",FACE,{"derivedFrom":[makeQuery(id+"F36.boolean.opBoolean","MERGE",FACE,{"derivedFrom":[makeQuery(id+"F1.opExtrude","CAP_FACE",FACE,{"disambiguationData":[OSD([sQuery(id+"F0.wireOp",EDGE,"E0.bottom"),sQuery(id+"F0.wireOp",EDGE,"E0.top"),sQuery(id+"F0.wireOp",EDGE,"E0.left"),sQuery(id+"F0.wireOp",EDGE,"E0.right")])],"isStart":false})],"fromTools":[makeQuery(id+"F36.opExtrude","SWEPT_FACE",FACE,{"disambiguationData":[OSD([sQuery(id+"F26.wireOp",EDGE,"E60.top"),sQuery(id+"F35.wireOp",EDGE,"E78")])]})]})],"fromTools":[makeQuery(id+"F37.opExtrude","SWEPT_FACE",FACE,{"disambiguationData":[OSD([sQuery(id+"F21.wireOp",EDGE,"E56.top"),sQuery(id+"F34.wireOp",EDGE,"E70")])]})]});
            var sketch = newSketch(context, id + "F119", { "sketchPlane" : qUnion([Q0])});
            skLineSegment(sketch, "E221", {"start": v(8.62, 55.6) * mm, "end": v(8.62, -24.7) * mm});
            skPoint(sketch, "E221.endSnap0", {"position": v(8.62, -15.64) * mm});
            skLineSegment(sketch, "E222", {"start": v(8.62, -24.7) * mm, "end": v(42.1, -24.7) * mm});
            skLineSegment(sketch, "E223", {"start": v(42.1, -24.7) * mm, "end": v(42.1, -61.97) * mm});
            skLineSegment(sketch, "E224", {"start": v(8.62, 55.6) * mm, "end": v(165.68, 55.6) * mm});
            skLineSegment(sketch, "E225", {"start": v(165.68, 55.6) * mm, "end": v(165.68, -61.97) * mm});
            skLineSegment(sketch, "E226", {"start": v(165.68, -61.97) * mm, "end": v(42.1, -61.97) * mm});
            skSolve(sketch);
        }
        {
            var Q0;
            Q0=qSketchRegion(id+"F119",true);
            extrude(context, id + "F120", {"entities" : qUnion([Q0]), "operationType" : NewBodyOperationType.REMOVE, "endBound" : BoundingType.SYMMETRIC, "oppositeDirection" : true, "depth" : 50.8 * mm, "offsetDistance" : 25.4 * mm});
        }
        {
            var Q0;
            Q0=makeQuery(id+"F120.boolean.opBoolean","MERGE",FACE,{"derivedFrom":[makeQuery(id+"F59.boolean.opBoolean","COPY",FACE,{"derivedFrom":makeQuery(id+"F59.opExtrude","SWEPT_FACE",FACE,{"disambiguationData":[OSD([sQuery(id+"F58.wireOp",EDGE,"E108.right")])]})})],"fromTools":[makeQuery(id+"F120.opExtrude","SWEPT_FACE",FACE,{"disambiguationData":[OSD([sQuery(id+"F119.wireOp",EDGE,"E223")])]})]});
            var sketch = newSketch(context, id + "F121", { "sketchPlane" : qUnion([Q0])});
            skCircle(sketch, "E227", {"center": v(-43.62, 0.7) * mm, "radius": 0.95 * mm});
            skSolve(sketch);
        }
        {
            var Q0;
            Q0=qSketchRegion(id+"F121",true);
            extrude(context, id + "F122", {"entities" : qUnion([Q0]), "operationType" : NewBodyOperationType.REMOVE, "oppositeDirection" : true, "depth" : 3.17 * mm, "offsetDistance" : 25.4 * mm});
        }
        {
            var Q0;
            Q0=makeQuery(id+"F120.boolean.opBoolean","MERGE",FACE,{"derivedFrom":[makeQuery(id+"F39.opExtrude","SWEPT_FACE",FACE,{"disambiguationData":[OSD([sQuery(id+"F38.wireOp",EDGE,"E82.left")])]})],"fromTools":[makeQuery(id+"F120.opExtrude","SWEPT_FACE",FACE,{"disambiguationData":[OSD([sQuery(id+"F119.wireOp",EDGE,"E221")])]})]});
            var sketch = newSketch(context, id + "F123", { "sketchPlane" : qUnion([Q0])});
            skCircle(sketch, "E228", {"center": v(-19.62, 0.7) * mm, "radius": 0.95 * mm});
            skCircle(sketch, "E229", {"center": v(43.62, 0.7) * mm, "radius": 0.95 * mm});
            skSolve(sketch);
        }
        {
            var Q0;
            Q0=qSketchRegion(id+"F123",true);
            extrude(context, id + "F124", {"entities" : qUnion([Q0]), "operationType" : NewBodyOperationType.REMOVE, "oppositeDirection" : true, "depth" : 3.17 * mm, "offsetDistance" : 25.4 * mm});
        }
        {
            var Q0;
            Q0=makeQuery(id+"F120.boolean.opBoolean","INTERSECT",EDGE,{"derivedFrom":[makeQuery(id+"F117.opExtrude","CAP_FACE",FACE,{"disambiguationData":[OSD([sQuery(id+"F0.wireOp",EDGE,"E0.bottom"),sQuery(id+"F0.wireOp",EDGE,"E0.top"),sQuery(id+"F0.wireOp",EDGE,"E0.left"),sQuery(id+"F0.wireOp",EDGE,"E0.right")])],"isStart":false}),makeQuery(id+"F120.opExtrude","SWEPT_FACE",FACE,{"disambiguationData":[OSD([sQuery(id+"F119.wireOp",EDGE,"E223")])]})]});
            var Q1;
            Q1=makeQuery(id+"F120.boolean.opBoolean","INTERSECT",EDGE,{"derivedFrom":[makeQuery(id+"F117.opExtrude","CAP_FACE",FACE,{"disambiguationData":[OSD([sQuery(id+"F0.wireOp",EDGE,"E0.bottom"),sQuery(id+"F0.wireOp",EDGE,"E0.top"),sQuery(id+"F0.wireOp",EDGE,"E0.left"),sQuery(id+"F0.wireOp",EDGE,"E0.right")])],"isStart":false}),makeQuery(id+"F120.opExtrude","SWEPT_FACE",FACE,{"disambiguationData":[OSD([sQuery(id+"F119.wireOp",EDGE,"E222")])]})]});
            var Q2;
            Q2=makeQuery(id+"F120.boolean.opBoolean","INTERSECT",EDGE,{"derivedFrom":[makeQuery(id+"F117.opExtrude","CAP_FACE",FACE,{"disambiguationData":[OSD([sQuery(id+"F0.wireOp",EDGE,"E0.bottom"),sQuery(id+"F0.wireOp",EDGE,"E0.top"),sQuery(id+"F0.wireOp",EDGE,"E0.left"),sQuery(id+"F0.wireOp",EDGE,"E0.right")])],"isStart":false}),makeQuery(id+"F120.opExtrude","SWEPT_FACE",FACE,{"disambiguationData":[OSD([sQuery(id+"F119.wireOp",EDGE,"E221")])]})]});
            chamfer(context, id + "F125", {"entities" : qUnion([Q0, Q1, Q2]), "width" : 0.76 * mm, "tangentPropagation" : true});
        }
    });
